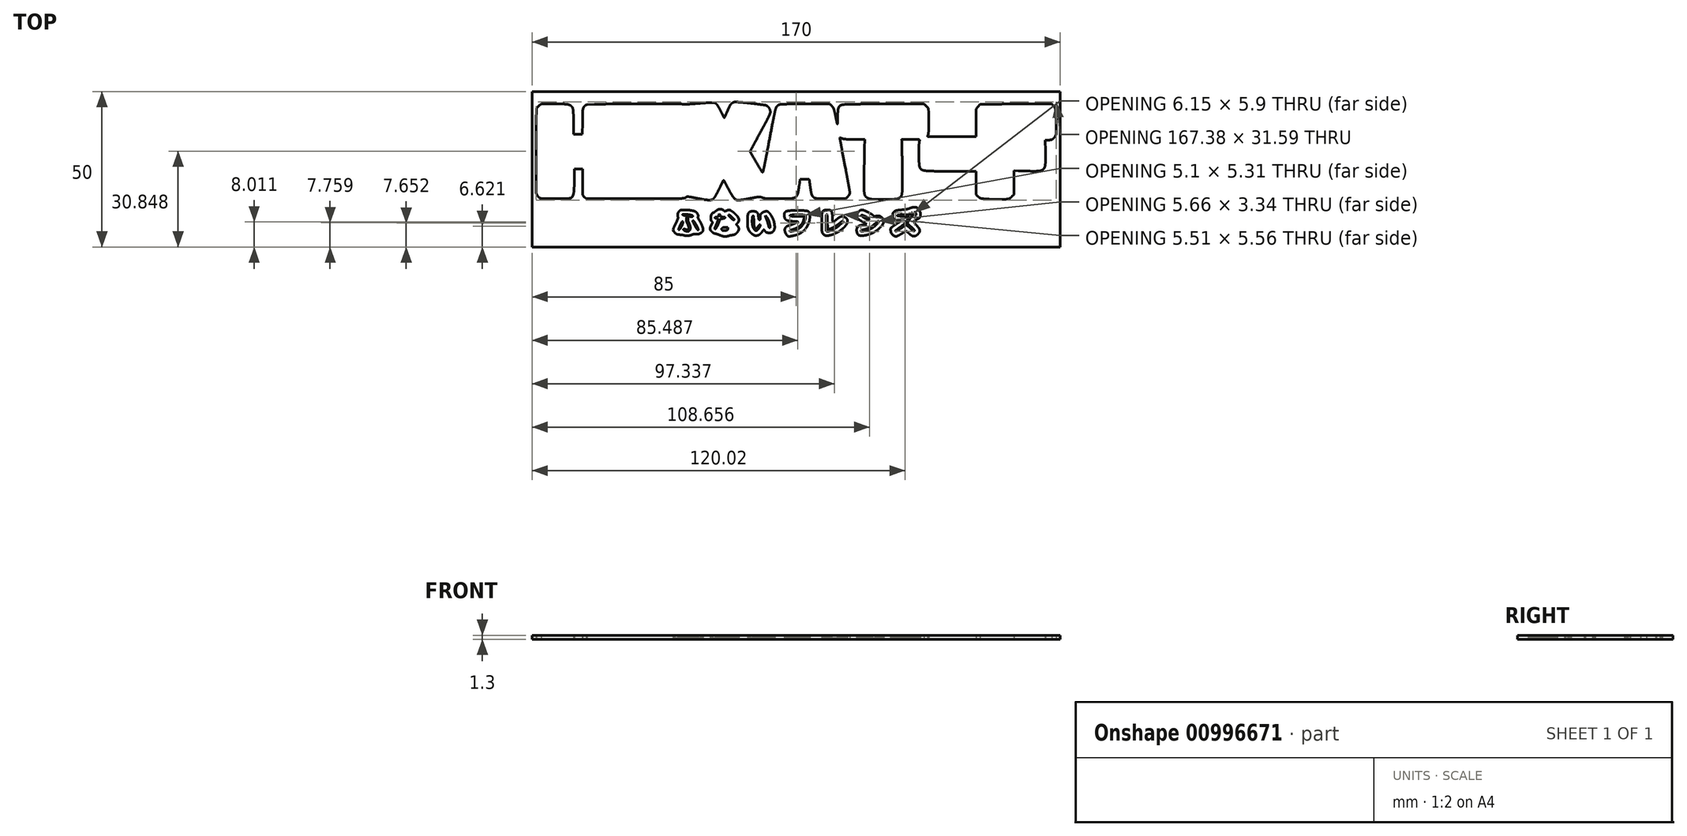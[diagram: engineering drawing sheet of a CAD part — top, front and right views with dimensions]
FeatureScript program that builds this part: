
annotation { "Feature Type Name" : "Feature", "Feature Type Description" : "" }
export const myFeature = defineFeature(function(context is Context, id is Id, definition is map)
    precondition{}
    {
        {
            var Q0;
            Q0=qCreatedBy(makeId("Top.planeOp"),FACE);
            var sketch = newSketch(context, id + "F0", { "sketchPlane" : qUnion([Q0])});
            skArc(sketch, "E0", {"start": v(-16.39, 21.41) * mm, "mid": v(-15.05, 21.27) * mm, "end": v(-13.72, 21.12) * mm});
            skArc(sketch, "E1", {"start": v(-13.72, 21.12) * mm, "mid": v(-12.67, 21) * mm, "end": v(-11.61, 20.86) * mm});
            skArc(sketch, "E2", {"start": v(-11.61, 20.86) * mm, "mid": v(-10.8, 20.74) * mm, "end": v(-9.97, 20.62) * mm});
            skArc(sketch, "E3", {"start": v(-9.97, 20.62) * mm, "mid": v(-9.73, 20.56) * mm, "end": v(-9.5, 20.47) * mm});
            skArc(sketch, "E4", {"start": v(-9.5, 20.47) * mm, "mid": v(-9.28, 20.34) * mm, "end": v(-9.1, 20.17) * mm});
            skArc(sketch, "E5", {"start": v(-9.1, 20.17) * mm, "mid": v(-8.9, 19.95) * mm, "end": v(-8.73, 19.7) * mm});
            skArc(sketch, "E6", {"start": v(-8.73, 19.7) * mm, "mid": v(-8.58, 19.45) * mm, "end": v(-8.45, 19.17) * mm});
            skArc(sketch, "E7", {"start": v(-8.45, 19.17) * mm, "mid": v(-8.37, 18.9) * mm, "end": v(-8.33, 18.63) * mm});
            skArc(sketch, "E8", {"start": v(-8.33, 18.63) * mm, "mid": v(-8.32, 18.52) * mm, "end": v(-8.32, 18.42) * mm});
            skArc(sketch, "E9", {"start": v(-8.32, 18.42) * mm, "mid": v(-8.32, 18.33) * mm, "end": v(-8.33, 18.24) * mm});
            skArc(sketch, "E10", {"start": v(-8.33, 18.24) * mm, "mid": v(-8.36, 18.14) * mm, "end": v(-8.38, 18.04) * mm});
            skArc(sketch, "E11", {"start": v(-8.38, 18.04) * mm, "mid": v(-8.43, 17.9) * mm, "end": v(-8.48, 17.77) * mm});
            skArc(sketch, "E12", {"start": v(-8.48, 17.77) * mm, "mid": v(-8.64, 17.4) * mm, "end": v(-8.8, 17.04) * mm});
            skArc(sketch, "E13", {"start": v(-8.8, 17.04) * mm, "mid": v(-9.11, 16.42) * mm, "end": v(-9.43, 15.8) * mm});
            skArc(sketch, "E14", {"start": v(-9.43, 15.8) * mm, "mid": v(-9.8, 15.06) * mm, "end": v(-10.2, 14.33) * mm});
            skArc(sketch, "E15", {"start": v(-10.2, 14.33) * mm, "mid": v(-10.61, 13.55) * mm, "end": v(-11.04, 12.77) * mm});
            skArc(sketch, "E16", {"start": v(-11.04, 12.77) * mm, "mid": v(-11.9, 11.22) * mm, "end": v(-12.74, 9.67) * mm});
            skArc(sketch, "E17", {"start": v(-12.74, 9.67) * mm, "mid": v(-13.3, 8.62) * mm, "end": v(-13.86, 7.57) * mm});
            skArc(sketch, "E18", {"start": v(-13.86, 7.57) * mm, "mid": v(-14.27, 6.8) * mm, "end": v(-14.67, 6.02) * mm});
            skArc(sketch, "E19", {"start": v(-14.67, 6.02) * mm, "mid": v(-14.73, 5.88) * mm, "end": v(-14.74, 5.72) * mm});
            skArc(sketch, "E20", {"start": v(-14.74, 5.72) * mm, "mid": v(-14.7, 5.46) * mm, "end": v(-14.6, 5.22) * mm});
            skArc(sketch, "E21", {"start": v(-14.6, 5.22) * mm, "mid": v(-13.73, 3.73) * mm, "end": v(-12.84, 2.24) * mm});
            skArc(sketch, "E22", {"start": v(-12.84, 2.24) * mm, "mid": v(-11.93, 0.71) * mm, "end": v(-11.02, -0.8) * mm});
            skArc(sketch, "E23", {"start": v(-11.02, -0.8) * mm, "mid": v(-10.9, -0.91) * mm, "end": v(-10.76, -0.95) * mm});
            skArc(sketch, "E24", {"start": v(-10.76, -0.95) * mm, "mid": v(-10.7, -0.93) * mm, "end": v(-10.66, -0.87) * mm});
            skArc(sketch, "E25", {"start": v(-10.66, -0.87) * mm, "mid": v(-10.44, 0.14) * mm, "end": v(-10.24, 1.15) * mm});
            skArc(sketch, "E26", {"start": v(-10.24, 1.15) * mm, "mid": v(-9.95, 2.55) * mm, "end": v(-9.68, 3.94) * mm});
            skArc(sketch, "E27", {"start": v(-9.68, 3.94) * mm, "mid": v(-9.23, 6.26) * mm, "end": v(-8.8, 8.58) * mm});
            skArc(sketch, "E28", {"start": v(-8.8, 8.58) * mm, "mid": v(-8.22, 11.62) * mm, "end": v(-7.63, 14.66) * mm});
            skArc(sketch, "E29", {"start": v(-7.63, 14.66) * mm, "mid": v(-7.35, 16.1) * mm, "end": v(-7.05, 17.54) * mm});
            skArc(sketch, "E30", {"start": v(-7.05, 17.54) * mm, "mid": v(-6.87, 18.38) * mm, "end": v(-6.66, 19.23) * mm});
            skArc(sketch, "E31", {"start": v(-6.66, 19.23) * mm, "mid": v(-6.54, 19.62) * mm, "end": v(-6.37, 20) * mm});
            skArc(sketch, "E32", {"start": v(-6.37, 20) * mm, "mid": v(-6.26, 20.16) * mm, "end": v(-6.14, 20.31) * mm});
            skArc(sketch, "E33", {"start": v(-6.14, 20.31) * mm, "mid": v(-6, 20.45) * mm, "end": v(-5.85, 20.57) * mm});
            skArc(sketch, "E34", {"start": v(-5.85, 20.57) * mm, "mid": v(-5.67, 20.68) * mm, "end": v(-5.49, 20.77) * mm});
            skArc(sketch, "E35", {"start": v(-5.49, 20.77) * mm, "mid": v(-5.28, 20.84) * mm, "end": v(-5.07, 20.9) * mm});
            skArc(sketch, "E36", {"start": v(-5.07, 20.9) * mm, "mid": v(-4.86, 20.93) * mm, "end": v(-4.64, 20.94) * mm});
            skArc(sketch, "E37", {"start": v(-4.64, 20.94) * mm, "mid": v(-3.87, 20.96) * mm, "end": v(-3.1, 20.97) * mm});
            skArc(sketch, "E38", {"start": v(-3.1, 20.97) * mm, "mid": v(-1.96, 20.98) * mm, "end": v(-0.81, 21) * mm});
            skArc(sketch, "E39", {"start": v(-0.81, 21) * mm, "mid": v(1.12, 21) * mm, "end": v(3.05, 21.01) * mm});
            skLineSegment(sketch, "E40", {"start": v(3.05, 21.01) * mm, "end": v(10.73, 21.04) * mm});
            skLineSegment(sketch, "E41", {"start": v(10.73, 21.04) * mm, "end": v(11.19, 20.64) * mm});
            skArc(sketch, "E42", {"start": v(11.19, 20.64) * mm, "mid": v(11.47, 20.36) * mm, "end": v(11.73, 20.06) * mm});
            skArc(sketch, "E43", {"start": v(11.73, 20.06) * mm, "mid": v(11.92, 19.77) * mm, "end": v(12.07, 19.45) * mm});
            skArc(sketch, "E44", {"start": v(12.07, 19.45) * mm, "mid": v(12.23, 19) * mm, "end": v(12.36, 18.52) * mm});
            skArc(sketch, "E45", {"start": v(12.36, 18.52) * mm, "mid": v(12.58, 17.5) * mm, "end": v(12.8, 16.48) * mm});
            skArc(sketch, "E46", {"start": v(12.8, 16.48) * mm, "mid": v(12.89, 16.08) * mm, "end": v(12.97, 15.67) * mm});
            skArc(sketch, "E47", {"start": v(12.97, 15.67) * mm, "mid": v(13.04, 15.35) * mm, "end": v(13.12, 15.03) * mm});
            skArc(sketch, "E48", {"start": v(13.12, 15.03) * mm, "mid": v(13.17, 14.8) * mm, "end": v(13.23, 14.55) * mm});
            skArc(sketch, "E49", {"start": v(13.23, 14.55) * mm, "mid": v(13.24, 14.54) * mm, "end": v(13.25, 14.55) * mm});
            skArc(sketch, "E50", {"start": v(13.25, 14.55) * mm, "mid": v(13.26, 14.63) * mm, "end": v(13.26, 14.7) * mm});
            skArc(sketch, "E51", {"start": v(13.26, 14.7) * mm, "mid": v(13.27, 15) * mm, "end": v(13.28, 15.29) * mm});
            skArc(sketch, "E52", {"start": v(13.28, 15.29) * mm, "mid": v(13.29, 15.63) * mm, "end": v(13.3, 15.98) * mm});
            skArc(sketch, "E53", {"start": v(13.3, 15.98) * mm, "mid": v(13.31, 16.37) * mm, "end": v(13.32, 16.76) * mm});
            skArc(sketch, "E54", {"start": v(13.32, 16.76) * mm, "mid": v(13.35, 17.49) * mm, "end": v(13.38, 18.21) * mm});
            skArc(sketch, "E55", {"start": v(13.38, 18.21) * mm, "mid": v(13.4, 18.6) * mm, "end": v(13.45, 19) * mm});
            skArc(sketch, "E56", {"start": v(13.45, 19) * mm, "mid": v(13.5, 19.26) * mm, "end": v(13.55, 19.52) * mm});
            skArc(sketch, "E57", {"start": v(13.55, 19.52) * mm, "mid": v(13.63, 19.75) * mm, "end": v(13.73, 19.98) * mm});
            skArc(sketch, "E58", {"start": v(13.73, 19.98) * mm, "mid": v(13.85, 20.18) * mm, "end": v(14, 20.35) * mm});
            skArc(sketch, "E59", {"start": v(14, 20.35) * mm, "mid": v(14.17, 20.5) * mm, "end": v(14.36, 20.6) * mm});
            skArc(sketch, "E60", {"start": v(14.36, 20.6) * mm, "mid": v(14.64, 20.7) * mm, "end": v(14.94, 20.76) * mm});
            skArc(sketch, "E61", {"start": v(14.94, 20.76) * mm, "mid": v(15.46, 20.83) * mm, "end": v(15.99, 20.9) * mm});
            skArc(sketch, "E62", {"start": v(15.99, 20.9) * mm, "mid": v(16.28, 20.93) * mm, "end": v(16.58, 20.94) * mm});
            skArc(sketch, "E63", {"start": v(16.58, 20.94) * mm, "mid": v(18.06, 20.95) * mm, "end": v(19.55, 20.96) * mm});
            skArc(sketch, "E64", {"start": v(19.55, 20.96) * mm, "mid": v(21.5, 20.98) * mm, "end": v(23.44, 20.99) * mm});
            skArc(sketch, "E65", {"start": v(23.44, 20.99) * mm, "mid": v(26.15, 21) * mm, "end": v(28.87, 21) * mm});
            skLineSegment(sketch, "E66", {"start": v(28.87, 21) * mm, "end": v(41.08, 21.04) * mm});
            skLineSegment(sketch, "E67", {"start": v(41.08, 21.04) * mm, "end": v(41.82, 20.37) * mm});
            skLineSegment(sketch, "E68", {"start": v(41.82, 20.37) * mm, "end": v(42.57, 19.7) * mm});
            skLineSegment(sketch, "E69", {"start": v(42.57, 19.7) * mm, "end": v(42.62, 18.14) * mm});
            skArc(sketch, "E70", {"start": v(42.62, 18.14) * mm, "mid": v(42.63, 17.76) * mm, "end": v(42.64, 17.37) * mm});
            skArc(sketch, "E71", {"start": v(42.64, 17.37) * mm, "mid": v(42.64, 16.84) * mm, "end": v(42.65, 16.3) * mm});
            skArc(sketch, "E72", {"start": v(42.65, 16.3) * mm, "mid": v(42.65, 15.72) * mm, "end": v(42.65, 15.14) * mm});
            skArc(sketch, "E73", {"start": v(42.65, 15.14) * mm, "mid": v(42.64, 14.6) * mm, "end": v(42.64, 14.06) * mm});
            skArc(sketch, "E74", {"start": v(42.64, 14.06) * mm, "mid": v(42.63, 13.3) * mm, "end": v(42.62, 12.54) * mm});
            skArc(sketch, "E75", {"start": v(42.62, 12.54) * mm, "mid": v(42.6, 12.2) * mm, "end": v(42.59, 11.86) * mm});
            skArc(sketch, "E76", {"start": v(42.59, 11.86) * mm, "mid": v(42.57, 11.65) * mm, "end": v(42.54, 11.44) * mm});
            skArc(sketch, "E77", {"start": v(42.54, 11.44) * mm, "mid": v(42.5, 11.26) * mm, "end": v(42.46, 11.09) * mm});
            skArc(sketch, "E78", {"start": v(42.46, 11.09) * mm, "mid": v(42.43, 11) * mm, "end": v(42.4, 10.91) * mm});
            skArc(sketch, "E79", {"start": v(42.4, 10.91) * mm, "mid": v(42.37, 10.83) * mm, "end": v(42.35, 10.75) * mm});
            skArc(sketch, "E80", {"start": v(42.35, 10.75) * mm, "mid": v(42.33, 10.69) * mm, "end": v(42.31, 10.62) * mm});
            skArc(sketch, "E81", {"start": v(42.31, 10.62) * mm, "mid": v(42.3, 10.6) * mm, "end": v(42.3, 10.58) * mm});
            skArc(sketch, "E82", {"start": v(42.3, 10.58) * mm, "mid": v(42.31, 10.57) * mm, "end": v(42.33, 10.56) * mm});
            skArc(sketch, "E83", {"start": v(42.33, 10.56) * mm, "mid": v(43.46, 10.55) * mm, "end": v(44.6, 10.54) * mm});
            skArc(sketch, "E84", {"start": v(44.6, 10.54) * mm, "mid": v(45.86, 10.54) * mm, "end": v(47.12, 10.53) * mm});
            skArc(sketch, "E85", {"start": v(47.12, 10.53) * mm, "mid": v(48.61, 10.53) * mm, "end": v(50.11, 10.53) * mm});
            skLineSegment(sketch, "E86", {"start": v(50.11, 10.53) * mm, "end": v(57.92, 10.53) * mm});
            skLineSegment(sketch, "E87", {"start": v(57.92, 10.53) * mm, "end": v(57.92, 14.98) * mm});
            skLineSegment(sketch, "E88", {"start": v(57.92, 14.98) * mm, "end": v(57.92, 19.43) * mm});
            skLineSegment(sketch, "E89", {"start": v(57.92, 19.43) * mm, "end": v(58.56, 20.15) * mm});
            skLineSegment(sketch, "E90", {"start": v(58.56, 20.15) * mm, "end": v(59.2, 20.88) * mm});
            skLineSegment(sketch, "E91", {"start": v(59.2, 20.88) * mm, "end": v(60.08, 20.92) * mm});
            skArc(sketch, "E92", {"start": v(60.08, 20.92) * mm, "mid": v(60.4, 20.93) * mm, "end": v(60.73, 20.93) * mm});
            skArc(sketch, "E93", {"start": v(60.73, 20.93) * mm, "mid": v(62.28, 20.95) * mm, "end": v(63.83, 20.96) * mm});
            skArc(sketch, "E94", {"start": v(63.83, 20.96) * mm, "mid": v(65.65, 20.97) * mm, "end": v(67.46, 20.98) * mm});
            skArc(sketch, "E95", {"start": v(67.46, 20.98) * mm, "mid": v(69.53, 21) * mm, "end": v(71.6, 21) * mm});
            skLineSegment(sketch, "E96", {"start": v(71.6, 21) * mm, "end": v(82.25, 21.05) * mm});
            skLineSegment(sketch, "E97", {"start": v(82.25, 21.05) * mm, "end": v(82.7, 20.57) * mm});
            skArc(sketch, "E98", {"start": v(82.7, 20.57) * mm, "mid": v(82.87, 20.36) * mm, "end": v(83.04, 20.15) * mm});
            skArc(sketch, "E99", {"start": v(83.04, 20.15) * mm, "mid": v(83.15, 19.98) * mm, "end": v(83.25, 19.8) * mm});
            skArc(sketch, "E100", {"start": v(83.25, 19.8) * mm, "mid": v(83.32, 19.62) * mm, "end": v(83.37, 19.42) * mm});
            skArc(sketch, "E101", {"start": v(83.37, 19.42) * mm, "mid": v(83.42, 19.16) * mm, "end": v(83.46, 18.9) * mm});
            skArc(sketch, "E102", {"start": v(83.46, 18.9) * mm, "mid": v(83.5, 18.42) * mm, "end": v(83.54, 17.94) * mm});
            skArc(sketch, "E103", {"start": v(83.54, 17.94) * mm, "mid": v(83.58, 17.18) * mm, "end": v(83.61, 16.43) * mm});
            skArc(sketch, "E104", {"start": v(83.61, 16.43) * mm, "mid": v(83.64, 15.59) * mm, "end": v(83.67, 14.75) * mm});
            skArc(sketch, "E105", {"start": v(83.67, 14.75) * mm, "mid": v(83.68, 13.95) * mm, "end": v(83.69, 13.14) * mm});
            skArc(sketch, "E106", {"start": v(83.69, 13.14) * mm, "mid": v(83.69, 12.54) * mm, "end": v(83.69, 11.93) * mm});
            skArc(sketch, "E107", {"start": v(83.69, 11.93) * mm, "mid": v(83.68, 11.7) * mm, "end": v(83.67, 11.46) * mm});
            skArc(sketch, "E108", {"start": v(83.67, 11.46) * mm, "mid": v(83.65, 11.32) * mm, "end": v(83.63, 11.18) * mm});
            skArc(sketch, "E109", {"start": v(83.63, 11.18) * mm, "mid": v(83.59, 11.05) * mm, "end": v(83.53, 10.93) * mm});
            skArc(sketch, "E110", {"start": v(83.53, 10.93) * mm, "mid": v(83.42, 10.72) * mm, "end": v(83.3, 10.52) * mm});
            skArc(sketch, "E111", {"start": v(83.3, 10.52) * mm, "mid": v(83.14, 10.32) * mm, "end": v(82.98, 10.13) * mm});
            skArc(sketch, "E112", {"start": v(82.98, 10.13) * mm, "mid": v(82.82, 9.96) * mm, "end": v(82.65, 9.8) * mm});
            skArc(sketch, "E113", {"start": v(82.65, 9.8) * mm, "mid": v(82.5, 9.69) * mm, "end": v(82.33, 9.6) * mm});
            skArc(sketch, "E114", {"start": v(82.33, 9.6) * mm, "mid": v(82.22, 9.54) * mm, "end": v(82.1, 9.49) * mm});
            skArc(sketch, "E115", {"start": v(82.1, 9.49) * mm, "mid": v(82, 9.46) * mm, "end": v(81.89, 9.44) * mm});
            skArc(sketch, "E116", {"start": v(81.89, 9.44) * mm, "mid": v(81.75, 9.42) * mm, "end": v(81.6, 9.41) * mm});
            skArc(sketch, "E117", {"start": v(81.6, 9.41) * mm, "mid": v(81.34, 9.41) * mm, "end": v(81.07, 9.4) * mm});
            skLineSegment(sketch, "E118", {"start": v(81.07, 9.4) * mm, "end": v(80.17, 9.4) * mm});
            skLineSegment(sketch, "E119", {"start": v(80.17, 9.4) * mm, "end": v(80.22, 5.86) * mm});
            skArc(sketch, "E120", {"start": v(80.22, 5.86) * mm, "mid": v(80.23, 4.63) * mm, "end": v(80.24, 3.4) * mm});
            skArc(sketch, "E121", {"start": v(80.24, 3.4) * mm, "mid": v(80.23, 2.75) * mm, "end": v(80.2, 2.1) * mm});
            skArc(sketch, "E122", {"start": v(80.2, 2.1) * mm, "mid": v(80.18, 1.68) * mm, "end": v(80.12, 1.26) * mm});
            skArc(sketch, "E123", {"start": v(80.12, 1.26) * mm, "mid": v(80.06, 0.94) * mm, "end": v(79.96, 0.62) * mm});
            skArc(sketch, "E124", {"start": v(79.96, 0.62) * mm, "mid": v(79.88, 0.45) * mm, "end": v(79.78, 0.29) * mm});
            skArc(sketch, "E125", {"start": v(79.78, 0.29) * mm, "mid": v(79.66, 0.13) * mm, "end": v(79.52, -0.02) * mm});
            skArc(sketch, "E126", {"start": v(79.52, -0.02) * mm, "mid": v(79.36, -0.14) * mm, "end": v(79.2, -0.26) * mm});
            skArc(sketch, "E127", {"start": v(79.2, -0.26) * mm, "mid": v(79.01, -0.35) * mm, "end": v(78.82, -0.42) * mm});
            skArc(sketch, "E128", {"start": v(78.82, -0.42) * mm, "mid": v(78.53, -0.5) * mm, "end": v(78.24, -0.54) * mm});
            skArc(sketch, "E129", {"start": v(78.24, -0.54) * mm, "mid": v(77.82, -0.59) * mm, "end": v(77.4, -0.61) * mm});
            skArc(sketch, "E130", {"start": v(77.4, -0.61) * mm, "mid": v(76.86, -0.63) * mm, "end": v(76.3, -0.63) * mm});
            skArc(sketch, "E131", {"start": v(76.3, -0.63) * mm, "mid": v(75.58, -0.62) * mm, "end": v(74.86, -0.6) * mm});
            skArc(sketch, "E132", {"start": v(74.86, -0.6) * mm, "mid": v(74.42, -0.59) * mm, "end": v(73.99, -0.57) * mm});
            skArc(sketch, "E133", {"start": v(73.99, -0.57) * mm, "mid": v(73.5, -0.56) * mm, "end": v(73.03, -0.54) * mm});
            skArc(sketch, "E134", {"start": v(73.03, -0.54) * mm, "mid": v(72.58, -0.53) * mm, "end": v(72.13, -0.51) * mm});
            skArc(sketch, "E135", {"start": v(72.13, -0.51) * mm, "mid": v(71.78, -0.5) * mm, "end": v(71.44, -0.49) * mm});
            skLineSegment(sketch, "E136", {"start": v(71.44, -0.49) * mm, "end": v(70.03, -0.44) * mm});
            skLineSegment(sketch, "E137", {"start": v(70.03, -0.44) * mm, "end": v(70.03, -4.29) * mm});
            skLineSegment(sketch, "E138", {"start": v(70.03, -4.29) * mm, "end": v(70.03, -8.13) * mm});
            skLineSegment(sketch, "E139", {"start": v(70.03, -8.13) * mm, "end": v(69.45, -8.74) * mm});
            skArc(sketch, "E140", {"start": v(69.45, -8.74) * mm, "mid": v(69.33, -8.86) * mm, "end": v(69.2, -8.98) * mm});
            skArc(sketch, "E141", {"start": v(69.2, -8.98) * mm, "mid": v(69.09, -9.1) * mm, "end": v(68.96, -9.2) * mm});
            skArc(sketch, "E142", {"start": v(68.96, -9.2) * mm, "mid": v(68.86, -9.29) * mm, "end": v(68.75, -9.37) * mm});
            skArc(sketch, "E143", {"start": v(68.75, -9.37) * mm, "mid": v(68.69, -9.42) * mm, "end": v(68.62, -9.45) * mm});
            skArc(sketch, "E144", {"start": v(68.62, -9.45) * mm, "mid": v(68.4, -9.52) * mm, "end": v(68.19, -9.57) * mm});
            skArc(sketch, "E145", {"start": v(68.19, -9.57) * mm, "mid": v(67.85, -9.61) * mm, "end": v(67.52, -9.64) * mm});
            skArc(sketch, "E146", {"start": v(67.52, -9.64) * mm, "mid": v(67.05, -9.67) * mm, "end": v(66.58, -9.69) * mm});
            skArc(sketch, "E147", {"start": v(66.58, -9.69) * mm, "mid": v(65.92, -9.7) * mm, "end": v(65.26, -9.7) * mm});
            skArc(sketch, "E148", {"start": v(65.26, -9.7) * mm, "mid": v(64.18, -9.7) * mm, "end": v(63.1, -9.67) * mm});
            skArc(sketch, "E149", {"start": v(63.1, -9.67) * mm, "mid": v(62.18, -9.64) * mm, "end": v(61.28, -9.58) * mm});
            skArc(sketch, "E150", {"start": v(61.28, -9.58) * mm, "mid": v(60.56, -9.53) * mm, "end": v(59.86, -9.45) * mm});
            skArc(sketch, "E151", {"start": v(59.86, -9.45) * mm, "mid": v(59.5, -9.39) * mm, "end": v(59.18, -9.27) * mm});
            skArc(sketch, "E152", {"start": v(59.18, -9.27) * mm, "mid": v(59.1, -9.23) * mm, "end": v(59.02, -9.19) * mm});
            skArc(sketch, "E153", {"start": v(59.02, -9.19) * mm, "mid": v(58.92, -9.11) * mm, "end": v(58.81, -9.04) * mm});
            skArc(sketch, "E154", {"start": v(58.81, -9.04) * mm, "mid": v(58.7, -8.95) * mm, "end": v(58.6, -8.86) * mm});
            skArc(sketch, "E155", {"start": v(58.6, -8.86) * mm, "mid": v(58.49, -8.76) * mm, "end": v(58.39, -8.67) * mm});
            skLineSegment(sketch, "E156", {"start": v(58.39, -8.67) * mm, "end": v(57.92, -8.2) * mm});
            skLineSegment(sketch, "E157", {"start": v(57.92, -8.2) * mm, "end": v(57.92, -4.44) * mm});
            skLineSegment(sketch, "E158", {"start": v(57.92, -4.44) * mm, "end": v(57.92, -0.67) * mm});
            skLineSegment(sketch, "E159", {"start": v(57.92, -0.67) * mm, "end": v(51.95, -0.67) * mm});
            skArc(sketch, "E160", {"start": v(51.95, -0.67) * mm, "mid": v(50.73, -0.67) * mm, "end": v(49.51, -0.66) * mm});
            skArc(sketch, "E161", {"start": v(49.51, -0.66) * mm, "mid": v(48.32, -0.66) * mm, "end": v(47.13, -0.65) * mm});
            skArc(sketch, "E162", {"start": v(47.13, -0.65) * mm, "mid": v(46.1, -0.64) * mm, "end": v(45.07, -0.63) * mm});
            skArc(sketch, "E163", {"start": v(45.07, -0.63) * mm, "mid": v(44.5, -0.62) * mm, "end": v(43.92, -0.6) * mm});
            skArc(sketch, "E164", {"start": v(43.92, -0.6) * mm, "mid": v(42.95, -0.57) * mm, "end": v(42, -0.51) * mm});
            skArc(sketch, "E165", {"start": v(42, -0.51) * mm, "mid": v(41.47, -0.46) * mm, "end": v(40.96, -0.37) * mm});
            skArc(sketch, "E166", {"start": v(40.96, -0.37) * mm, "mid": v(40.64, -0.26) * mm, "end": v(40.33, -0.11) * mm});
            skArc(sketch, "E167", {"start": v(40.33, -0.11) * mm, "mid": v(40.1, 0.07) * mm, "end": v(39.91, 0.3) * mm});
            skArc(sketch, "E168", {"start": v(39.91, 0.3) * mm, "mid": v(39.81, 0.5) * mm, "end": v(39.74, 0.7) * mm});
            skArc(sketch, "E169", {"start": v(39.74, 0.7) * mm, "mid": v(39.68, 0.92) * mm, "end": v(39.63, 1.16) * mm});
            skArc(sketch, "E170", {"start": v(39.63, 1.16) * mm, "mid": v(39.59, 1.52) * mm, "end": v(39.56, 1.89) * mm});
            skArc(sketch, "E171", {"start": v(39.56, 1.89) * mm, "mid": v(39.53, 2.57) * mm, "end": v(39.5, 3.25) * mm});
            skArc(sketch, "E172", {"start": v(39.5, 3.25) * mm, "mid": v(39.47, 4.22) * mm, "end": v(39.46, 5.19) * mm});
            skArc(sketch, "E173", {"start": v(39.46, 5.19) * mm, "mid": v(39.47, 6.13) * mm, "end": v(39.5, 7.07) * mm});
            skArc(sketch, "E174", {"start": v(39.5, 7.07) * mm, "mid": v(39.53, 7.89) * mm, "end": v(39.58, 8.7) * mm});
            skArc(sketch, "E175", {"start": v(39.58, 8.7) * mm, "mid": v(39.62, 8.97) * mm, "end": v(39.72, 9.21) * mm});
            skArc(sketch, "E176", {"start": v(39.72, 9.21) * mm, "mid": v(39.74, 9.25) * mm, "end": v(39.75, 9.29) * mm});
            skArc(sketch, "E177", {"start": v(39.75, 9.29) * mm, "mid": v(39.76, 9.32) * mm, "end": v(39.76, 9.35) * mm});
            skArc(sketch, "E178", {"start": v(39.76, 9.35) * mm, "mid": v(39.75, 9.38) * mm, "end": v(39.74, 9.4) * mm});
            skArc(sketch, "E179", {"start": v(39.74, 9.4) * mm, "mid": v(39.71, 9.44) * mm, "end": v(39.68, 9.47) * mm});
            skArc(sketch, "E180", {"start": v(39.68, 9.47) * mm, "mid": v(39.62, 9.52) * mm, "end": v(39.54, 9.54) * mm});
            skArc(sketch, "E181", {"start": v(39.54, 9.54) * mm, "mid": v(39.33, 9.56) * mm, "end": v(39.11, 9.57) * mm});
            skArc(sketch, "E182", {"start": v(39.11, 9.57) * mm, "mid": v(38.74, 9.58) * mm, "end": v(38.37, 9.6) * mm});
            skArc(sketch, "E183", {"start": v(38.37, 9.6) * mm, "mid": v(37.55, 9.6) * mm, "end": v(36.73, 9.6) * mm});
            skArc(sketch, "E184", {"start": v(36.73, 9.6) * mm, "mid": v(35.83, 9.61) * mm, "end": v(34.93, 9.62) * mm});
            skArc(sketch, "E185", {"start": v(34.93, 9.62) * mm, "mid": v(34.61, 9.62) * mm, "end": v(34.3, 9.6) * mm});
            skArc(sketch, "E186", {"start": v(34.3, 9.6) * mm, "mid": v(34.14, 9.6) * mm, "end": v(33.98, 9.58) * mm});
            skArc(sketch, "E187", {"start": v(33.98, 9.58) * mm, "mid": v(33.94, 9.55) * mm, "end": v(33.93, 9.5) * mm});
            skArc(sketch, "E188", {"start": v(33.93, 9.5) * mm, "mid": v(33.97, 9.35) * mm, "end": v(33.98, 9.2) * mm});
            skArc(sketch, "E189", {"start": v(33.98, 9.2) * mm, "mid": v(34.02, 7.57) * mm, "end": v(34.05, 5.93) * mm});
            skArc(sketch, "E190", {"start": v(34.05, 5.93) * mm, "mid": v(34.09, 4.16) * mm, "end": v(34.12, 2.39) * mm});
            skArc(sketch, "E191", {"start": v(34.12, 2.39) * mm, "mid": v(34.14, 0.5) * mm, "end": v(34.16, -1.4) * mm});
            skArc(sketch, "E192", {"start": v(34.16, -1.4) * mm, "mid": v(34.17, -3.38) * mm, "end": v(34.18, -5.36) * mm});
            skArc(sketch, "E193", {"start": v(34.18, -5.36) * mm, "mid": v(34.16, -6.27) * mm, "end": v(34.11, -7.2) * mm});
            skArc(sketch, "E194", {"start": v(34.11, -7.2) * mm, "mid": v(34.05, -7.73) * mm, "end": v(33.95, -8.25) * mm});
            skArc(sketch, "E195", {"start": v(33.95, -8.25) * mm, "mid": v(33.82, -8.6) * mm, "end": v(33.61, -8.9) * mm});
            skArc(sketch, "E196", {"start": v(33.61, -8.9) * mm, "mid": v(33.42, -9.09) * mm, "end": v(33.2, -9.24) * mm});
            skArc(sketch, "E197", {"start": v(33.2, -9.24) * mm, "mid": v(32.92, -9.37) * mm, "end": v(32.64, -9.47) * mm});
            skArc(sketch, "E198", {"start": v(32.64, -9.47) * mm, "mid": v(32.24, -9.55) * mm, "end": v(31.83, -9.6) * mm});
            skArc(sketch, "E199", {"start": v(31.83, -9.6) * mm, "mid": v(31.17, -9.67) * mm, "end": v(30.51, -9.7) * mm});
            skArc(sketch, "E200", {"start": v(30.51, -9.7) * mm, "mid": v(29.72, -9.74) * mm, "end": v(28.93, -9.76) * mm});
            skArc(sketch, "E201", {"start": v(28.93, -9.76) * mm, "mid": v(27.9, -9.76) * mm, "end": v(26.87, -9.75) * mm});
            skArc(sketch, "E202", {"start": v(26.87, -9.75) * mm, "mid": v(25.89, -9.73) * mm, "end": v(24.9, -9.7) * mm});
            skArc(sketch, "E203", {"start": v(24.9, -9.7) * mm, "mid": v(24.46, -9.67) * mm, "end": v(24.03, -9.6) * mm});
            skArc(sketch, "E204", {"start": v(24.03, -9.6) * mm, "mid": v(23.78, -9.55) * mm, "end": v(23.53, -9.48) * mm});
            skArc(sketch, "E205", {"start": v(23.53, -9.48) * mm, "mid": v(23.29, -9.4) * mm, "end": v(23.05, -9.29) * mm});
            skArc(sketch, "E206", {"start": v(23.05, -9.29) * mm, "mid": v(22.84, -9.18) * mm, "end": v(22.64, -9.06) * mm});
            skArc(sketch, "E207", {"start": v(22.64, -9.06) * mm, "mid": v(22.5, -8.95) * mm, "end": v(22.37, -8.83) * mm});
            skArc(sketch, "E208", {"start": v(22.37, -8.83) * mm, "mid": v(22.15, -8.51) * mm, "end": v(22.03, -8.15) * mm});
            skArc(sketch, "E209", {"start": v(22.03, -8.15) * mm, "mid": v(21.92, -7.58) * mm, "end": v(21.86, -7) * mm});
            skArc(sketch, "E210", {"start": v(21.86, -7) * mm, "mid": v(21.82, -6.02) * mm, "end": v(21.8, -5.03) * mm});
            skArc(sketch, "E211", {"start": v(21.8, -5.03) * mm, "mid": v(21.83, -3) * mm, "end": v(21.85, -0.95) * mm});
            skArc(sketch, "E212", {"start": v(21.85, -0.95) * mm, "mid": v(21.87, 0.08) * mm, "end": v(21.89, 1.12) * mm});
            skArc(sketch, "E213", {"start": v(21.89, 1.12) * mm, "mid": v(21.9, 2.22) * mm, "end": v(21.93, 3.32) * mm});
            skArc(sketch, "E214", {"start": v(21.93, 3.32) * mm, "mid": v(21.94, 4.33) * mm, "end": v(21.96, 5.34) * mm});
            skArc(sketch, "E215", {"start": v(21.96, 5.34) * mm, "mid": v(21.97, 6.05) * mm, "end": v(21.98, 6.77) * mm});
            skLineSegment(sketch, "E216", {"start": v(21.98, 6.77) * mm, "end": v(22.03, 9.62) * mm});
            skLineSegment(sketch, "E217", {"start": v(22.03, 9.62) * mm, "end": v(19.23, 9.62) * mm});
            skArc(sketch, "E218", {"start": v(19.23, 9.62) * mm, "mid": v(18.14, 9.62) * mm, "end": v(17.04, 9.63) * mm});
            skArc(sketch, "E219", {"start": v(17.04, 9.63) * mm, "mid": v(16.47, 9.65) * mm, "end": v(15.9, 9.69) * mm});
            skArc(sketch, "E220", {"start": v(15.9, 9.69) * mm, "mid": v(15.52, 9.73) * mm, "end": v(15.15, 9.79) * mm});
            skArc(sketch, "E221", {"start": v(15.15, 9.79) * mm, "mid": v(14.86, 9.87) * mm, "end": v(14.57, 9.98) * mm});
            skArc(sketch, "E222", {"start": v(14.57, 9.98) * mm, "mid": v(14.48, 10.02) * mm, "end": v(14.39, 10.06) * mm});
            skArc(sketch, "E223", {"start": v(14.39, 10.06) * mm, "mid": v(14.3, 10.1) * mm, "end": v(14.22, 10.12) * mm});
            skArc(sketch, "E224", {"start": v(14.22, 10.12) * mm, "mid": v(14.15, 10.14) * mm, "end": v(14.08, 10.16) * mm});
            skArc(sketch, "E225", {"start": v(14.08, 10.16) * mm, "mid": v(14.07, 10.17) * mm, "end": v(14.05, 10.16) * mm});
            skArc(sketch, "E226", {"start": v(14.05, 10.16) * mm, "mid": v(14.04, 10.14) * mm, "end": v(14.03, 10.11) * mm});
            skArc(sketch, "E227", {"start": v(14.03, 10.11) * mm, "mid": v(14.16, 9.43) * mm, "end": v(14.28, 8.74) * mm});
            skArc(sketch, "E228", {"start": v(14.28, 8.74) * mm, "mid": v(14.42, 7.98) * mm, "end": v(14.56, 7.21) * mm});
            skArc(sketch, "E229", {"start": v(14.56, 7.21) * mm, "mid": v(14.73, 6.3) * mm, "end": v(14.9, 5.4) * mm});
            skArc(sketch, "E230", {"start": v(14.9, 5.4) * mm, "mid": v(15.08, 4.43) * mm, "end": v(15.27, 3.45) * mm});
            skArc(sketch, "E231", {"start": v(15.27, 3.45) * mm, "mid": v(15.45, 2.47) * mm, "end": v(15.64, 1.5) * mm});
            skArc(sketch, "E232", {"start": v(15.64, 1.5) * mm, "mid": v(15.8, 0.63) * mm, "end": v(15.97, -0.23) * mm});
            skArc(sketch, "E233", {"start": v(15.97, -0.23) * mm, "mid": v(16.07, -0.77) * mm, "end": v(16.17, -1.3) * mm});
            skArc(sketch, "E234", {"start": v(16.17, -1.3) * mm, "mid": v(16.37, -2.39) * mm, "end": v(16.57, -3.47) * mm});
            skArc(sketch, "E235", {"start": v(16.57, -3.47) * mm, "mid": v(16.75, -4.46) * mm, "end": v(16.92, -5.44) * mm});
            skArc(sketch, "E236", {"start": v(16.92, -5.44) * mm, "mid": v(17.07, -6.3) * mm, "end": v(17.21, -7.15) * mm});
            skArc(sketch, "E237", {"start": v(17.21, -7.15) * mm, "mid": v(17.24, -7.35) * mm, "end": v(17.25, -7.56) * mm});
            skArc(sketch, "E238", {"start": v(17.25, -7.56) * mm, "mid": v(17.23, -7.72) * mm, "end": v(17.2, -7.87) * mm});
            skArc(sketch, "E239", {"start": v(17.2, -7.87) * mm, "mid": v(17.14, -8.04) * mm, "end": v(17.06, -8.2) * mm});
            skArc(sketch, "E240", {"start": v(17.06, -8.2) * mm, "mid": v(16.94, -8.4) * mm, "end": v(16.81, -8.57) * mm});
            skArc(sketch, "E241", {"start": v(16.81, -8.57) * mm, "mid": v(16.63, -8.78) * mm, "end": v(16.45, -8.98) * mm});
            skLineSegment(sketch, "E242", {"start": v(16.45, -8.98) * mm, "end": v(15.96, -9.5) * mm});
            skLineSegment(sketch, "E243", {"start": v(15.96, -9.5) * mm, "end": v(11.3, -9.47) * mm});
            skArc(sketch, "E244", {"start": v(11.3, -9.47) * mm, "mid": v(10.04, -9.46) * mm, "end": v(8.77, -9.45) * mm});
            skArc(sketch, "E245", {"start": v(8.77, -9.45) * mm, "mid": v(8.1, -9.44) * mm, "end": v(7.44, -9.43) * mm});
            skArc(sketch, "E246", {"start": v(7.44, -9.43) * mm, "mid": v(7.03, -9.42) * mm, "end": v(6.62, -9.4) * mm});
            skArc(sketch, "E247", {"start": v(6.62, -9.4) * mm, "mid": v(6.43, -9.38) * mm, "end": v(6.25, -9.34) * mm});
            skArc(sketch, "E248", {"start": v(6.25, -9.34) * mm, "mid": v(5.88, -9.2) * mm, "end": v(5.55, -9) * mm});
            skArc(sketch, "E249", {"start": v(5.55, -9) * mm, "mid": v(5.3, -8.74) * mm, "end": v(5.11, -8.44) * mm});
            skArc(sketch, "E250", {"start": v(5.11, -8.44) * mm, "mid": v(4.93, -7.94) * mm, "end": v(4.8, -7.42) * mm});
            skArc(sketch, "E251", {"start": v(4.8, -7.42) * mm, "mid": v(4.63, -6.34) * mm, "end": v(4.47, -5.26) * mm});
            skArc(sketch, "E252", {"start": v(4.47, -5.26) * mm, "mid": v(4.42, -4.9) * mm, "end": v(4.37, -4.55) * mm});
            skArc(sketch, "E253", {"start": v(4.37, -4.55) * mm, "mid": v(4.33, -4.24) * mm, "end": v(4.28, -3.93) * mm});
            skArc(sketch, "E254", {"start": v(4.28, -3.93) * mm, "mid": v(4.24, -3.67) * mm, "end": v(4.2, -3.4) * mm});
            skArc(sketch, "E255", {"start": v(4.2, -3.4) * mm, "mid": v(4.2, -3.36) * mm, "end": v(4.18, -3.31) * mm});
            skArc(sketch, "E256", {"start": v(4.18, -3.31) * mm, "mid": v(4.16, -3.27) * mm, "end": v(4.11, -3.24) * mm});
            skArc(sketch, "E257", {"start": v(4.11, -3.24) * mm, "mid": v(4.02, -3.22) * mm, "end": v(3.93, -3.21) * mm});
            skArc(sketch, "E258", {"start": v(3.93, -3.21) * mm, "mid": v(3.75, -3.2) * mm, "end": v(3.57, -3.2) * mm});
            skArc(sketch, "E259", {"start": v(3.57, -3.2) * mm, "mid": v(3.13, -3.2) * mm, "end": v(2.7, -3.2) * mm});
            skLineSegment(sketch, "E260", {"start": v(2.7, -3.2) * mm, "end": v(1.25, -3.23) * mm});
            skLineSegment(sketch, "E261", {"start": v(1.25, -3.23) * mm, "end": v(0.96, -5.19) * mm});
            skArc(sketch, "E262", {"start": v(0.96, -5.19) * mm, "mid": v(0.85, -5.94) * mm, "end": v(0.74, -6.7) * mm});
            skArc(sketch, "E263", {"start": v(0.74, -6.7) * mm, "mid": v(0.68, -7.06) * mm, "end": v(0.6, -7.42) * mm});
            skArc(sketch, "E264", {"start": v(0.6, -7.42) * mm, "mid": v(0.56, -7.66) * mm, "end": v(0.5, -7.88) * mm});
            skArc(sketch, "E265", {"start": v(0.5, -7.88) * mm, "mid": v(0.43, -8.08) * mm, "end": v(0.35, -8.27) * mm});
            skArc(sketch, "E266", {"start": v(0.35, -8.27) * mm, "mid": v(0.22, -8.51) * mm, "end": v(0.06, -8.74) * mm});
            skArc(sketch, "E267", {"start": v(0.06, -8.74) * mm, "mid": v(-0.11, -8.91) * mm, "end": v(-0.31, -9.06) * mm});
            skArc(sketch, "E268", {"start": v(-0.31, -9.06) * mm, "mid": v(-0.56, -9.19) * mm, "end": v(-0.82, -9.28) * mm});
            skArc(sketch, "E269", {"start": v(-0.82, -9.28) * mm, "mid": v(-1.16, -9.36) * mm, "end": v(-1.51, -9.42) * mm});
            skArc(sketch, "E270", {"start": v(-1.51, -9.42) * mm, "mid": v(-1.95, -9.46) * mm, "end": v(-2.4, -9.48) * mm});
            skArc(sketch, "E271", {"start": v(-2.4, -9.48) * mm, "mid": v(-3.99, -9.48) * mm, "end": v(-5.58, -9.49) * mm});
            skArc(sketch, "E272", {"start": v(-5.58, -9.49) * mm, "mid": v(-7.15, -9.48) * mm, "end": v(-8.73, -9.48) * mm});
            skArc(sketch, "E273", {"start": v(-8.73, -9.48) * mm, "mid": v(-9.25, -9.46) * mm, "end": v(-9.76, -9.42) * mm});
            skArc(sketch, "E274", {"start": v(-9.76, -9.42) * mm, "mid": v(-9.92, -9.4) * mm, "end": v(-10.08, -9.38) * mm});
            skArc(sketch, "E275", {"start": v(-10.08, -9.38) * mm, "mid": v(-10.23, -9.35) * mm, "end": v(-10.37, -9.32) * mm});
            skArc(sketch, "E276", {"start": v(-10.37, -9.32) * mm, "mid": v(-10.5, -9.28) * mm, "end": v(-10.64, -9.24) * mm});
            skArc(sketch, "E277", {"start": v(-10.64, -9.24) * mm, "mid": v(-10.76, -9.2) * mm, "end": v(-10.88, -9.15) * mm});
            skArc(sketch, "E278", {"start": v(-10.88, -9.15) * mm, "mid": v(-10.98, -9.1) * mm, "end": v(-11.08, -9.07) * mm});
            skArc(sketch, "E279", {"start": v(-11.08, -9.07) * mm, "mid": v(-11.18, -9.03) * mm, "end": v(-11.27, -9) * mm});
            skArc(sketch, "E280", {"start": v(-11.27, -9) * mm, "mid": v(-11.36, -8.96) * mm, "end": v(-11.45, -8.93) * mm});
            skArc(sketch, "E281", {"start": v(-11.45, -8.93) * mm, "mid": v(-11.5, -8.91) * mm, "end": v(-11.56, -8.9) * mm});
            skArc(sketch, "E282", {"start": v(-11.56, -8.9) * mm, "mid": v(-11.72, -8.88) * mm, "end": v(-11.88, -8.89) * mm});
            skArc(sketch, "E283", {"start": v(-11.88, -8.89) * mm, "mid": v(-12.24, -8.93) * mm, "end": v(-12.6, -8.98) * mm});
            skArc(sketch, "E284", {"start": v(-12.6, -8.98) * mm, "mid": v(-13.1, -9.06) * mm, "end": v(-13.6, -9.14) * mm});
            skArc(sketch, "E285", {"start": v(-13.6, -9.14) * mm, "mid": v(-14.31, -9.27) * mm, "end": v(-15.02, -9.41) * mm});
            skArc(sketch, "E286", {"start": v(-15.02, -9.41) * mm, "mid": v(-15.9, -9.58) * mm, "end": v(-16.78, -9.74) * mm});
            skArc(sketch, "E287", {"start": v(-16.78, -9.74) * mm, "mid": v(-17.32, -9.83) * mm, "end": v(-17.86, -9.9) * mm});
            skArc(sketch, "E288", {"start": v(-17.86, -9.9) * mm, "mid": v(-18.23, -9.93) * mm, "end": v(-18.6, -9.95) * mm});
            skArc(sketch, "E289", {"start": v(-18.6, -9.95) * mm, "mid": v(-18.9, -9.93) * mm, "end": v(-19.18, -9.89) * mm});
            skArc(sketch, "E290", {"start": v(-19.18, -9.89) * mm, "mid": v(-19.47, -9.78) * mm, "end": v(-19.72, -9.58) * mm});
            skArc(sketch, "E291", {"start": v(-19.72, -9.58) * mm, "mid": v(-20.05, -9.2) * mm, "end": v(-20.36, -8.79) * mm});
            skArc(sketch, "E292", {"start": v(-20.36, -8.79) * mm, "mid": v(-20.8, -8.12) * mm, "end": v(-21.2, -7.42) * mm});
            skArc(sketch, "E293", {"start": v(-21.2, -7.42) * mm, "mid": v(-21.86, -6.23) * mm, "end": v(-22.5, -5.03) * mm});
            skArc(sketch, "E294", {"start": v(-22.5, -5.03) * mm, "mid": v(-22.66, -4.74) * mm, "end": v(-22.82, -4.46) * mm});
            skArc(sketch, "E295", {"start": v(-22.82, -4.46) * mm, "mid": v(-22.95, -4.21) * mm, "end": v(-23.08, -3.97) * mm});
            skArc(sketch, "E296", {"start": v(-23.08, -3.97) * mm, "mid": v(-23.2, -3.75) * mm, "end": v(-23.32, -3.54) * mm});
            skArc(sketch, "E297", {"start": v(-23.32, -3.54) * mm, "mid": v(-23.33, -3.52) * mm, "end": v(-23.35, -3.5) * mm});
            skArc(sketch, "E298", {"start": v(-23.35, -3.5) * mm, "mid": v(-23.37, -3.5) * mm, "end": v(-23.38, -3.52) * mm});
            skArc(sketch, "E299", {"start": v(-23.38, -3.52) * mm, "mid": v(-23.53, -3.8) * mm, "end": v(-23.67, -4.07) * mm});
            skArc(sketch, "E300", {"start": v(-23.67, -4.07) * mm, "mid": v(-23.83, -4.39) * mm, "end": v(-24, -4.7) * mm});
            skArc(sketch, "E301", {"start": v(-24, -4.7) * mm, "mid": v(-24.18, -5.09) * mm, "end": v(-24.37, -5.47) * mm});
            skArc(sketch, "E302", {"start": v(-24.37, -5.47) * mm, "mid": v(-24.9, -6.56) * mm, "end": v(-25.46, -7.65) * mm});
            skArc(sketch, "E303", {"start": v(-25.46, -7.65) * mm, "mid": v(-25.79, -8.26) * mm, "end": v(-26.14, -8.85) * mm});
            skArc(sketch, "E304", {"start": v(-26.14, -8.85) * mm, "mid": v(-26.4, -9.2) * mm, "end": v(-26.68, -9.53) * mm});
            skArc(sketch, "E305", {"start": v(-26.68, -9.53) * mm, "mid": v(-26.9, -9.72) * mm, "end": v(-27.17, -9.83) * mm});
            skArc(sketch, "E306", {"start": v(-27.17, -9.83) * mm, "mid": v(-27.36, -9.87) * mm, "end": v(-27.55, -9.9) * mm});
            skArc(sketch, "E307", {"start": v(-27.55, -9.9) * mm, "mid": v(-27.83, -9.9) * mm, "end": v(-28.12, -9.9) * mm});
            skArc(sketch, "E308", {"start": v(-28.12, -9.9) * mm, "mid": v(-28.44, -9.9) * mm, "end": v(-28.76, -9.88) * mm});
            skArc(sketch, "E309", {"start": v(-28.76, -9.88) * mm, "mid": v(-29.08, -9.85) * mm, "end": v(-29.4, -9.8) * mm});
            skArc(sketch, "E310", {"start": v(-29.4, -9.8) * mm, "mid": v(-29.6, -9.77) * mm, "end": v(-29.8, -9.74) * mm});
            skArc(sketch, "E311", {"start": v(-29.8, -9.74) * mm, "mid": v(-30.16, -9.67) * mm, "end": v(-30.53, -9.6) * mm});
            skArc(sketch, "E312", {"start": v(-30.53, -9.6) * mm, "mid": v(-30.95, -9.52) * mm, "end": v(-31.37, -9.44) * mm});
            skArc(sketch, "E313", {"start": v(-31.37, -9.44) * mm, "mid": v(-31.8, -9.36) * mm, "end": v(-32.24, -9.27) * mm});
            skArc(sketch, "E314", {"start": v(-32.24, -9.27) * mm, "mid": v(-32.67, -9.19) * mm, "end": v(-33.1, -9.1) * mm});
            skArc(sketch, "E315", {"start": v(-33.1, -9.1) * mm, "mid": v(-33.49, -9.04) * mm, "end": v(-33.88, -8.97) * mm});
            skArc(sketch, "E316", {"start": v(-33.88, -8.97) * mm, "mid": v(-34.2, -8.91) * mm, "end": v(-34.54, -8.86) * mm});
            skArc(sketch, "E317", {"start": v(-34.54, -8.86) * mm, "mid": v(-34.67, -8.84) * mm, "end": v(-34.8, -8.84) * mm});
            skArc(sketch, "E318", {"start": v(-34.8, -8.84) * mm, "mid": v(-34.92, -8.84) * mm, "end": v(-35.04, -8.84) * mm});
            skArc(sketch, "E319", {"start": v(-35.04, -8.84) * mm, "mid": v(-35.12, -8.85) * mm, "end": v(-35.2, -8.86) * mm});
            skArc(sketch, "E320", {"start": v(-35.2, -8.86) * mm, "mid": v(-35.26, -8.88) * mm, "end": v(-35.32, -8.91) * mm});
            skArc(sketch, "E321", {"start": v(-35.32, -8.91) * mm, "mid": v(-35.39, -8.96) * mm, "end": v(-35.45, -9.02) * mm});
            skArc(sketch, "E322", {"start": v(-35.45, -9.02) * mm, "mid": v(-35.58, -9.11) * mm, "end": v(-35.72, -9.19) * mm});
            skArc(sketch, "E323", {"start": v(-35.72, -9.19) * mm, "mid": v(-35.88, -9.25) * mm, "end": v(-36.05, -9.3) * mm});
            skArc(sketch, "E324", {"start": v(-36.05, -9.3) * mm, "mid": v(-36.3, -9.34) * mm, "end": v(-36.54, -9.36) * mm});
            skArc(sketch, "E325", {"start": v(-36.54, -9.36) * mm, "mid": v(-36.96, -9.4) * mm, "end": v(-37.38, -9.42) * mm});
            skArc(sketch, "E326", {"start": v(-37.38, -9.42) * mm, "mid": v(-37.8, -9.44) * mm, "end": v(-38.21, -9.45) * mm});
            skArc(sketch, "E327", {"start": v(-38.21, -9.45) * mm, "mid": v(-40.33, -9.46) * mm, "end": v(-42.45, -9.47) * mm});
            skArc(sketch, "E328", {"start": v(-42.45, -9.47) * mm, "mid": v(-44.93, -9.48) * mm, "end": v(-47.4, -9.48) * mm});
            skArc(sketch, "E329", {"start": v(-47.4, -9.48) * mm, "mid": v(-50.24, -9.49) * mm, "end": v(-53.07, -9.49) * mm});
            skLineSegment(sketch, "E330", {"start": v(-53.07, -9.49) * mm, "end": v(-67.63, -9.5) * mm});
            skLineSegment(sketch, "E331", {"start": v(-67.63, -9.5) * mm, "end": v(-68.2, -8.91) * mm});
            skLineSegment(sketch, "E332", {"start": v(-68.2, -8.91) * mm, "end": v(-68.78, -8.34) * mm});
            skLineSegment(sketch, "E333", {"start": v(-68.78, -8.34) * mm, "end": v(-68.78, -4.15) * mm});
            skLineSegment(sketch, "E334", {"start": v(-68.78, -4.15) * mm, "end": v(-68.78, 0.03) * mm});
            skLineSegment(sketch, "E335", {"start": v(-68.78, 0.03) * mm, "end": v(-70.07, 0.03) * mm});
            skLineSegment(sketch, "E336", {"start": v(-70.07, 0.03) * mm, "end": v(-71.35, 0.03) * mm});
            skLineSegment(sketch, "E337", {"start": v(-71.35, 0.03) * mm, "end": v(-71.4, -3.14) * mm});
            skArc(sketch, "E338", {"start": v(-71.4, -3.14) * mm, "mid": v(-71.42, -4.4) * mm, "end": v(-71.45, -5.67) * mm});
            skArc(sketch, "E339", {"start": v(-71.45, -5.67) * mm, "mid": v(-71.48, -6.35) * mm, "end": v(-71.53, -7.04) * mm});
            skArc(sketch, "E340", {"start": v(-71.53, -7.04) * mm, "mid": v(-71.59, -7.48) * mm, "end": v(-71.67, -7.92) * mm});
            skArc(sketch, "E341", {"start": v(-71.67, -7.92) * mm, "mid": v(-71.77, -8.26) * mm, "end": v(-71.9, -8.58) * mm});
            skArc(sketch, "E342", {"start": v(-71.9, -8.58) * mm, "mid": v(-71.97, -8.7) * mm, "end": v(-72.05, -8.83) * mm});
            skArc(sketch, "E343", {"start": v(-72.05, -8.83) * mm, "mid": v(-72.12, -8.93) * mm, "end": v(-72.2, -9.03) * mm});
            skArc(sketch, "E344", {"start": v(-72.2, -9.03) * mm, "mid": v(-72.3, -9.1) * mm, "end": v(-72.39, -9.17) * mm});
            skArc(sketch, "E345", {"start": v(-72.39, -9.17) * mm, "mid": v(-72.48, -9.23) * mm, "end": v(-72.59, -9.28) * mm});
            skArc(sketch, "E346", {"start": v(-72.59, -9.28) * mm, "mid": v(-72.83, -9.35) * mm, "end": v(-73.09, -9.38) * mm});
            skArc(sketch, "E347", {"start": v(-73.09, -9.38) * mm, "mid": v(-73.7, -9.42) * mm, "end": v(-74.33, -9.45) * mm});
            skArc(sketch, "E348", {"start": v(-74.33, -9.45) * mm, "mid": v(-75.18, -9.47) * mm, "end": v(-76.04, -9.48) * mm});
            skArc(sketch, "E349", {"start": v(-76.04, -9.48) * mm, "mid": v(-77.24, -9.48) * mm, "end": v(-78.44, -9.48) * mm});
            skArc(sketch, "E350", {"start": v(-78.44, -9.48) * mm, "mid": v(-79.62, -9.47) * mm, "end": v(-80.79, -9.46) * mm});
            skArc(sketch, "E351", {"start": v(-80.79, -9.46) * mm, "mid": v(-81.22, -9.45) * mm, "end": v(-81.66, -9.44) * mm});
            skArc(sketch, "E352", {"start": v(-81.66, -9.44) * mm, "mid": v(-81.9, -9.42) * mm, "end": v(-82.13, -9.4) * mm});
            skArc(sketch, "E353", {"start": v(-82.13, -9.4) * mm, "mid": v(-82.29, -9.36) * mm, "end": v(-82.43, -9.31) * mm});
            skArc(sketch, "E354", {"start": v(-82.43, -9.31) * mm, "mid": v(-82.58, -9.23) * mm, "end": v(-82.72, -9.13) * mm});
            skArc(sketch, "E355", {"start": v(-82.72, -9.13) * mm, "mid": v(-82.86, -9.02) * mm, "end": v(-82.98, -8.89) * mm});
            skArc(sketch, "E356", {"start": v(-82.98, -8.89) * mm, "mid": v(-83.11, -8.73) * mm, "end": v(-83.22, -8.56) * mm});
            skArc(sketch, "E357", {"start": v(-83.22, -8.56) * mm, "mid": v(-83.34, -8.37) * mm, "end": v(-83.44, -8.16) * mm});
            skLineSegment(sketch, "E358", {"start": v(-83.44, -8.16) * mm, "end": v(-83.66, -7.7) * mm});
            skLineSegment(sketch, "E359", {"start": v(-83.66, -7.7) * mm, "end": v(-83.68, 1.7) * mm});
            skArc(sketch, "E360", {"start": v(-83.68, 1.7) * mm, "mid": v(-83.69, 3.67) * mm, "end": v(-83.69, 5.63) * mm});
            skArc(sketch, "E361", {"start": v(-83.69, 5.63) * mm, "mid": v(-83.69, 7.62) * mm, "end": v(-83.68, 9.62) * mm});
            skArc(sketch, "E362", {"start": v(-83.68, 9.62) * mm, "mid": v(-83.68, 11.38) * mm, "end": v(-83.67, 13.15) * mm});
            skArc(sketch, "E363", {"start": v(-83.67, 13.15) * mm, "mid": v(-83.67, 14.28) * mm, "end": v(-83.66, 15.41) * mm});
            skLineSegment(sketch, "E364", {"start": v(-83.66, 15.41) * mm, "end": v(-83.6, 19.7) * mm});
            skLineSegment(sketch, "E365", {"start": v(-83.6, 19.7) * mm, "end": v(-82.86, 20.37) * mm});
            skLineSegment(sketch, "E366", {"start": v(-82.86, 20.37) * mm, "end": v(-82.12, 21.04) * mm});
            skLineSegment(sketch, "E367", {"start": v(-82.12, 21.04) * mm, "end": v(-78.02, 21.01) * mm});
            skArc(sketch, "E368", {"start": v(-78.02, 21.01) * mm, "mid": v(-76.72, 21) * mm, "end": v(-75.42, 21) * mm});
            skArc(sketch, "E369", {"start": v(-75.42, 21) * mm, "mid": v(-74.92, 20.98) * mm, "end": v(-74.42, 20.97) * mm});
            skArc(sketch, "E370", {"start": v(-74.42, 20.97) * mm, "mid": v(-74.13, 20.95) * mm, "end": v(-73.83, 20.92) * mm});
            skArc(sketch, "E371", {"start": v(-73.83, 20.92) * mm, "mid": v(-73.6, 20.88) * mm, "end": v(-73.37, 20.83) * mm});
            skArc(sketch, "E372", {"start": v(-73.37, 20.83) * mm, "mid": v(-73.06, 20.73) * mm, "end": v(-72.75, 20.6) * mm});
            skArc(sketch, "E373", {"start": v(-72.75, 20.6) * mm, "mid": v(-72.53, 20.47) * mm, "end": v(-72.33, 20.3) * mm});
            skArc(sketch, "E374", {"start": v(-72.33, 20.3) * mm, "mid": v(-72.17, 20.11) * mm, "end": v(-72.04, 19.9) * mm});
            skArc(sketch, "E375", {"start": v(-72.04, 19.9) * mm, "mid": v(-71.92, 19.59) * mm, "end": v(-71.82, 19.28) * mm});
            skArc(sketch, "E376", {"start": v(-71.82, 19.28) * mm, "mid": v(-71.78, 19.08) * mm, "end": v(-71.76, 18.89) * mm});
            skArc(sketch, "E377", {"start": v(-71.76, 18.89) * mm, "mid": v(-71.73, 18.56) * mm, "end": v(-71.72, 18.24) * mm});
            skArc(sketch, "E378", {"start": v(-71.72, 18.24) * mm, "mid": v(-71.7, 17.7) * mm, "end": v(-71.7, 17.17) * mm});
            skArc(sketch, "E379", {"start": v(-71.7, 17.17) * mm, "mid": v(-71.68, 16.1) * mm, "end": v(-71.67, 15.03) * mm});
            skLineSegment(sketch, "E380", {"start": v(-71.67, 15.03) * mm, "end": v(-71.64, 11.23) * mm});
            skLineSegment(sketch, "E381", {"start": v(-71.64, 11.23) * mm, "end": v(-70.23, 11.25) * mm});
            skLineSegment(sketch, "E382", {"start": v(-70.23, 11.25) * mm, "end": v(-68.82, 11.26) * mm});
            skLineSegment(sketch, "E383", {"start": v(-68.82, 11.26) * mm, "end": v(-68.78, 15.04) * mm});
            skArc(sketch, "E384", {"start": v(-68.78, 15.04) * mm, "mid": v(-68.77, 16.08) * mm, "end": v(-68.75, 17.1) * mm});
            skArc(sketch, "E385", {"start": v(-68.75, 17.1) * mm, "mid": v(-68.74, 17.66) * mm, "end": v(-68.72, 18.21) * mm});
            skArc(sketch, "E386", {"start": v(-68.72, 18.21) * mm, "mid": v(-68.7, 18.56) * mm, "end": v(-68.68, 18.9) * mm});
            skArc(sketch, "E387", {"start": v(-68.68, 18.9) * mm, "mid": v(-68.66, 19.1) * mm, "end": v(-68.62, 19.31) * mm});
            skArc(sketch, "E388", {"start": v(-68.62, 19.31) * mm, "mid": v(-68.56, 19.55) * mm, "end": v(-68.48, 19.78) * mm});
            skArc(sketch, "E389", {"start": v(-68.48, 19.78) * mm, "mid": v(-68.4, 19.97) * mm, "end": v(-68.3, 20.14) * mm});
            skArc(sketch, "E390", {"start": v(-68.3, 20.14) * mm, "mid": v(-68.18, 20.29) * mm, "end": v(-68.05, 20.42) * mm});
            skArc(sketch, "E391", {"start": v(-68.05, 20.42) * mm, "mid": v(-67.9, 20.53) * mm, "end": v(-67.73, 20.62) * mm});
            skLineSegment(sketch, "E392", {"start": v(-67.73, 20.62) * mm, "end": v(-67.35, 20.82) * mm});
            skLineSegment(sketch, "E393", {"start": v(-67.35, 20.82) * mm, "end": v(-64.86, 20.89) * mm});
            skArc(sketch, "E394", {"start": v(-64.86, 20.89) * mm, "mid": v(-61.49, 20.97) * mm, "end": v(-58.1, 21.01) * mm});
            skArc(sketch, "E395", {"start": v(-58.1, 21.01) * mm, "mid": v(-53.33, 21.05) * mm, "end": v(-48.56, 21.07) * mm});
            skArc(sketch, "E396", {"start": v(-48.56, 21.07) * mm, "mid": v(-43.64, 21.08) * mm, "end": v(-38.73, 21.08) * mm});
            skArc(sketch, "E397", {"start": v(-38.73, 21.08) * mm, "mid": v(-37.67, 21.04) * mm, "end": v(-36.62, 20.95) * mm});
            skArc(sketch, "E398", {"start": v(-36.62, 20.95) * mm, "mid": v(-36.28, 20.92) * mm, "end": v(-35.94, 20.91) * mm});
            skArc(sketch, "E399", {"start": v(-35.94, 20.91) * mm, "mid": v(-35.42, 20.92) * mm, "end": v(-34.9, 20.94) * mm});
            skArc(sketch, "E400", {"start": v(-34.9, 20.94) * mm, "mid": v(-34.14, 20.98) * mm, "end": v(-33.4, 21.03) * mm});
            skArc(sketch, "E401", {"start": v(-33.4, 21.03) * mm, "mid": v(-32.26, 21.12) * mm, "end": v(-31.12, 21.2) * mm});
            skArc(sketch, "E402", {"start": v(-31.12, 21.2) * mm, "mid": v(-30.2, 21.28) * mm, "end": v(-29.28, 21.35) * mm});
            skArc(sketch, "E403", {"start": v(-29.28, 21.35) * mm, "mid": v(-28.55, 21.39) * mm, "end": v(-27.82, 21.42) * mm});
            skArc(sketch, "E404", {"start": v(-27.82, 21.42) * mm, "mid": v(-27.27, 21.44) * mm, "end": v(-26.7, 21.45) * mm});
            skArc(sketch, "E405", {"start": v(-26.7, 21.45) * mm, "mid": v(-26.48, 21.43) * mm, "end": v(-26.25, 21.39) * mm});
            skArc(sketch, "E406", {"start": v(-26.25, 21.39) * mm, "mid": v(-26.01, 21.29) * mm, "end": v(-25.81, 21.13) * mm});
            skArc(sketch, "E407", {"start": v(-25.81, 21.13) * mm, "mid": v(-25.57, 20.87) * mm, "end": v(-25.35, 20.58) * mm});
            skArc(sketch, "E408", {"start": v(-25.35, 20.58) * mm, "mid": v(-25.05, 20.11) * mm, "end": v(-24.77, 19.63) * mm});
            skArc(sketch, "E409", {"start": v(-24.77, 19.63) * mm, "mid": v(-24.33, 18.8) * mm, "end": v(-23.9, 17.98) * mm});
            skArc(sketch, "E410", {"start": v(-23.9, 17.98) * mm, "mid": v(-23.77, 17.7) * mm, "end": v(-23.62, 17.43) * mm});
            skArc(sketch, "E411", {"start": v(-23.62, 17.43) * mm, "mid": v(-23.5, 17.2) * mm, "end": v(-23.38, 16.97) * mm});
            skArc(sketch, "E412", {"start": v(-23.38, 16.97) * mm, "mid": v(-23.27, 16.77) * mm, "end": v(-23.16, 16.57) * mm});
            skArc(sketch, "E413", {"start": v(-23.16, 16.57) * mm, "mid": v(-23.15, 16.55) * mm, "end": v(-23.14, 16.55) * mm});
            skArc(sketch, "E414", {"start": v(-23.14, 16.55) * mm, "mid": v(-23.12, 16.55) * mm, "end": v(-23.11, 16.57) * mm});
            skArc(sketch, "E415", {"start": v(-23.11, 16.57) * mm, "mid": v(-23, 16.79) * mm, "end": v(-22.9, 17) * mm});
            skArc(sketch, "E416", {"start": v(-22.9, 17) * mm, "mid": v(-22.8, 17.26) * mm, "end": v(-22.68, 17.5) * mm});
            skArc(sketch, "E417", {"start": v(-22.68, 17.5) * mm, "mid": v(-22.54, 17.8) * mm, "end": v(-22.41, 18.1) * mm});
            skArc(sketch, "E418", {"start": v(-22.41, 18.1) * mm, "mid": v(-22.27, 18.42) * mm, "end": v(-22.13, 18.74) * mm});
            skArc(sketch, "E419", {"start": v(-22.13, 18.74) * mm, "mid": v(-22, 19.05) * mm, "end": v(-21.86, 19.35) * mm});
            skArc(sketch, "E420", {"start": v(-21.86, 19.35) * mm, "mid": v(-21.74, 19.62) * mm, "end": v(-21.63, 19.88) * mm});
            skArc(sketch, "E421", {"start": v(-21.63, 19.88) * mm, "mid": v(-21.56, 20.02) * mm, "end": v(-21.5, 20.17) * mm});
            skArc(sketch, "E422", {"start": v(-21.5, 20.17) * mm, "mid": v(-21.36, 20.43) * mm, "end": v(-21.2, 20.67) * mm});
            skArc(sketch, "E423", {"start": v(-21.2, 20.67) * mm, "mid": v(-21.04, 20.9) * mm, "end": v(-20.84, 21.1) * mm});
            skArc(sketch, "E424", {"start": v(-20.84, 21.1) * mm, "mid": v(-20.64, 21.26) * mm, "end": v(-20.42, 21.4) * mm});
            skArc(sketch, "E425", {"start": v(-20.42, 21.4) * mm, "mid": v(-20.2, 21.52) * mm, "end": v(-19.96, 21.6) * mm});
            skArc(sketch, "E426", {"start": v(-19.96, 21.6) * mm, "mid": v(-19.78, 21.63) * mm, "end": v(-19.6, 21.64) * mm});
            skArc(sketch, "E427", {"start": v(-19.6, 21.64) * mm, "mid": v(-19.2, 21.63) * mm, "end": v(-18.8, 21.61) * mm});
            skArc(sketch, "E428", {"start": v(-18.8, 21.61) * mm, "mid": v(-18.27, 21.58) * mm, "end": v(-17.74, 21.54) * mm});
            skArc(sketch, "E429", {"start": v(-17.74, 21.54) * mm, "mid": v(-17.06, 21.48) * mm, "end": v(-16.39, 21.41) * mm});
            skArc(sketch, "E430", {"start": v(38.81, -12.33) * mm, "mid": v(38.94, -12.43) * mm, "end": v(39.06, -12.55) * mm});
            skArc(sketch, "E431", {"start": v(39.06, -12.55) * mm, "mid": v(39.2, -12.72) * mm, "end": v(39.34, -12.89) * mm});
            skArc(sketch, "E432", {"start": v(39.34, -12.89) * mm, "mid": v(39.48, -13.07) * mm, "end": v(39.6, -13.26) * mm});
            skArc(sketch, "E433", {"start": v(39.6, -13.26) * mm, "mid": v(39.71, -13.44) * mm, "end": v(39.8, -13.62) * mm});
            skArc(sketch, "E434", {"start": v(39.8, -13.62) * mm, "mid": v(39.87, -13.75) * mm, "end": v(39.92, -13.88) * mm});
            skArc(sketch, "E435", {"start": v(39.92, -13.88) * mm, "mid": v(39.96, -13.98) * mm, "end": v(39.99, -14.08) * mm});
            skArc(sketch, "E436", {"start": v(39.99, -14.08) * mm, "mid": v(40, -14.18) * mm, "end": v(40.02, -14.29) * mm});
            skArc(sketch, "E437", {"start": v(40.02, -14.29) * mm, "mid": v(40.03, -14.43) * mm, "end": v(40.03, -14.56) * mm});
            skArc(sketch, "E438", {"start": v(40.03, -14.56) * mm, "mid": v(40.01, -14.85) * mm, "end": v(39.96, -15.13) * mm});
            skArc(sketch, "E439", {"start": v(39.96, -15.13) * mm, "mid": v(39.87, -15.35) * mm, "end": v(39.75, -15.55) * mm});
            skArc(sketch, "E440", {"start": v(39.75, -15.55) * mm, "mid": v(39.57, -15.74) * mm, "end": v(39.36, -15.88) * mm});
            skArc(sketch, "E441", {"start": v(39.36, -15.88) * mm, "mid": v(39.07, -16.02) * mm, "end": v(38.77, -16.14) * mm});
            skArc(sketch, "E442", {"start": v(38.77, -16.14) * mm, "mid": v(38.53, -16.23) * mm, "end": v(38.3, -16.34) * mm});
            skArc(sketch, "E443", {"start": v(38.3, -16.34) * mm, "mid": v(38.16, -16.44) * mm, "end": v(38.05, -16.58) * mm});
            skArc(sketch, "E444", {"start": v(38.05, -16.58) * mm, "mid": v(37.99, -16.71) * mm, "end": v(37.98, -16.86) * mm});
            skArc(sketch, "E445", {"start": v(37.98, -16.86) * mm, "mid": v(38, -17.05) * mm, "end": v(38.07, -17.22) * mm});
            skArc(sketch, "E446", {"start": v(38.07, -17.22) * mm, "mid": v(38.1, -17.28) * mm, "end": v(38.14, -17.34) * mm});
            skArc(sketch, "E447", {"start": v(38.14, -17.34) * mm, "mid": v(38.22, -17.45) * mm, "end": v(38.3, -17.55) * mm});
            skArc(sketch, "E448", {"start": v(38.3, -17.55) * mm, "mid": v(38.4, -17.67) * mm, "end": v(38.5, -17.8) * mm});
            skArc(sketch, "E449", {"start": v(38.5, -17.8) * mm, "mid": v(38.6, -17.92) * mm, "end": v(38.71, -18.04) * mm});
            skArc(sketch, "E450", {"start": v(38.71, -18.04) * mm, "mid": v(38.95, -18.31) * mm, "end": v(39.19, -18.6) * mm});
            skArc(sketch, "E451", {"start": v(39.19, -18.6) * mm, "mid": v(39.36, -18.82) * mm, "end": v(39.52, -19.05) * mm});
            skArc(sketch, "E452", {"start": v(39.52, -19.05) * mm, "mid": v(39.63, -19.23) * mm, "end": v(39.72, -19.43) * mm});
            skArc(sketch, "E453", {"start": v(39.72, -19.43) * mm, "mid": v(39.77, -19.56) * mm, "end": v(39.78, -19.7) * mm});
            skArc(sketch, "E454", {"start": v(39.78, -19.7) * mm, "mid": v(39.74, -20.03) * mm, "end": v(39.62, -20.33) * mm});
            skArc(sketch, "E455", {"start": v(39.62, -20.33) * mm, "mid": v(39.4, -20.65) * mm, "end": v(39.14, -20.94) * mm});
            skArc(sketch, "E456", {"start": v(39.14, -20.94) * mm, "mid": v(38.83, -21.2) * mm, "end": v(38.48, -21.4) * mm});
            skArc(sketch, "E457", {"start": v(38.48, -21.4) * mm, "mid": v(38.16, -21.52) * mm, "end": v(37.82, -21.56) * mm});
            skArc(sketch, "E458", {"start": v(37.82, -21.56) * mm, "mid": v(37.72, -21.56) * mm, "end": v(37.62, -21.55) * mm});
            skArc(sketch, "E459", {"start": v(37.62, -21.55) * mm, "mid": v(37.54, -21.53) * mm, "end": v(37.46, -21.5) * mm});
            skArc(sketch, "E460", {"start": v(37.46, -21.5) * mm, "mid": v(37.36, -21.46) * mm, "end": v(37.27, -21.4) * mm});
            skArc(sketch, "E461", {"start": v(37.27, -21.4) * mm, "mid": v(37.13, -21.31) * mm, "end": v(36.98, -21.22) * mm});
            skArc(sketch, "E462", {"start": v(36.98, -21.22) * mm, "mid": v(36.86, -21.13) * mm, "end": v(36.75, -21.05) * mm});
            skArc(sketch, "E463", {"start": v(36.75, -21.05) * mm, "mid": v(36.6, -20.93) * mm, "end": v(36.45, -20.81) * mm});
            skArc(sketch, "E464", {"start": v(36.45, -20.81) * mm, "mid": v(36.3, -20.69) * mm, "end": v(36.16, -20.56) * mm});
            skArc(sketch, "E465", {"start": v(36.16, -20.56) * mm, "mid": v(36.03, -20.45) * mm, "end": v(35.9, -20.33) * mm});
            skLineSegment(sketch, "E466", {"start": v(35.9, -20.33) * mm, "end": v(35.33, -19.78) * mm});
            skLineSegment(sketch, "E467", {"start": v(35.33, -19.78) * mm, "end": v(34.95, -20.07) * mm});
            skArc(sketch, "E468", {"start": v(34.95, -20.07) * mm, "mid": v(34.56, -20.35) * mm, "end": v(34.16, -20.61) * mm});
            skArc(sketch, "E469", {"start": v(34.16, -20.61) * mm, "mid": v(33.73, -20.87) * mm, "end": v(33.3, -21.12) * mm});
            skArc(sketch, "E470", {"start": v(33.3, -21.12) * mm, "mid": v(32.9, -21.32) * mm, "end": v(32.5, -21.5) * mm});
            skArc(sketch, "E471", {"start": v(32.5, -21.5) * mm, "mid": v(32.3, -21.58) * mm, "end": v(32.09, -21.6) * mm});
            skArc(sketch, "E472", {"start": v(32.09, -21.6) * mm, "mid": v(31.85, -21.58) * mm, "end": v(31.62, -21.5) * mm});
            skArc(sketch, "E473", {"start": v(31.62, -21.5) * mm, "mid": v(31.38, -21.37) * mm, "end": v(31.16, -21.2) * mm});
            skArc(sketch, "E474", {"start": v(31.16, -21.2) * mm, "mid": v(30.95, -21) * mm, "end": v(30.76, -20.78) * mm});
            skArc(sketch, "E475", {"start": v(30.76, -20.78) * mm, "mid": v(30.62, -20.53) * mm, "end": v(30.51, -20.27) * mm});
            skArc(sketch, "E476", {"start": v(30.51, -20.27) * mm, "mid": v(30.46, -20.1) * mm, "end": v(30.42, -19.92) * mm});
            skArc(sketch, "E477", {"start": v(30.42, -19.92) * mm, "mid": v(30.4, -19.74) * mm, "end": v(30.39, -19.55) * mm});
            skArc(sketch, "E478", {"start": v(30.39, -19.55) * mm, "mid": v(30.39, -19.38) * mm, "end": v(30.4, -19.21) * mm});
            skArc(sketch, "E479", {"start": v(30.4, -19.21) * mm, "mid": v(30.42, -19.1) * mm, "end": v(30.47, -18.98) * mm});
            skArc(sketch, "E480", {"start": v(30.47, -18.98) * mm, "mid": v(30.55, -18.86) * mm, "end": v(30.65, -18.76) * mm});
            skArc(sketch, "E481", {"start": v(30.65, -18.76) * mm, "mid": v(30.88, -18.58) * mm, "end": v(31.1, -18.4) * mm});
            skArc(sketch, "E482", {"start": v(31.1, -18.4) * mm, "mid": v(31.42, -18.17) * mm, "end": v(31.75, -17.94) * mm});
            skArc(sketch, "E483", {"start": v(31.75, -17.94) * mm, "mid": v(32.2, -17.65) * mm, "end": v(32.64, -17.36) * mm});
            skLineSegment(sketch, "E484", {"start": v(32.64, -17.36) * mm, "end": v(33.72, -16.67) * mm});
            skLineSegment(sketch, "E485", {"start": v(33.72, -16.67) * mm, "end": v(33.2, -16.61) * mm});
            skArc(sketch, "E486", {"start": v(33.2, -16.61) * mm, "mid": v(32.8, -16.56) * mm, "end": v(32.4, -16.5) * mm});
            skArc(sketch, "E487", {"start": v(32.4, -16.5) * mm, "mid": v(32.12, -16.43) * mm, "end": v(31.87, -16.32) * mm});
            skArc(sketch, "E488", {"start": v(31.87, -16.32) * mm, "mid": v(31.68, -16.2) * mm, "end": v(31.5, -16.06) * mm});
            skArc(sketch, "E489", {"start": v(31.5, -16.06) * mm, "mid": v(31.36, -15.88) * mm, "end": v(31.24, -15.68) * mm});
            skArc(sketch, "E490", {"start": v(31.24, -15.68) * mm, "mid": v(31.2, -15.59) * mm, "end": v(31.16, -15.49) * mm});
            skArc(sketch, "E491", {"start": v(31.16, -15.49) * mm, "mid": v(31.14, -15.4) * mm, "end": v(31.11, -15.3) * mm});
            skArc(sketch, "E492", {"start": v(31.11, -15.3) * mm, "mid": v(31.1, -15.2) * mm, "end": v(31.09, -15.1) * mm});
            skArc(sketch, "E493", {"start": v(31.09, -15.1) * mm, "mid": v(31.08, -14.95) * mm, "end": v(31.08, -14.82) * mm});
            skArc(sketch, "E494", {"start": v(31.08, -14.82) * mm, "mid": v(31.09, -14.53) * mm, "end": v(31.13, -14.25) * mm});
            skArc(sketch, "E495", {"start": v(31.13, -14.25) * mm, "mid": v(31.2, -14.03) * mm, "end": v(31.32, -13.83) * mm});
            skArc(sketch, "E496", {"start": v(31.32, -13.83) * mm, "mid": v(31.47, -13.66) * mm, "end": v(31.66, -13.53) * mm});
            skArc(sketch, "E497", {"start": v(31.66, -13.53) * mm, "mid": v(31.9, -13.4) * mm, "end": v(32.17, -13.3) * mm});
            skArc(sketch, "E498", {"start": v(32.17, -13.3) * mm, "mid": v(32.32, -13.27) * mm, "end": v(32.47, -13.24) * mm});
            skArc(sketch, "E499", {"start": v(32.47, -13.24) * mm, "mid": v(32.67, -13.2) * mm, "end": v(32.88, -13.18) * mm});
            skArc(sketch, "E500", {"start": v(32.88, -13.18) * mm, "mid": v(33.2, -13.14) * mm, "end": v(33.53, -13.1) * mm});
            skArc(sketch, "E501", {"start": v(33.53, -13.1) * mm, "mid": v(34.12, -13.05) * mm, "end": v(34.71, -13) * mm});
            skArc(sketch, "E502", {"start": v(34.71, -13) * mm, "mid": v(35, -12.96) * mm, "end": v(35.28, -12.92) * mm});
            skArc(sketch, "E503", {"start": v(35.28, -12.92) * mm, "mid": v(35.5, -12.89) * mm, "end": v(35.73, -12.84) * mm});
            skArc(sketch, "E504", {"start": v(35.73, -12.84) * mm, "mid": v(35.94, -12.78) * mm, "end": v(36.15, -12.72) * mm});
            skArc(sketch, "E505", {"start": v(36.15, -12.72) * mm, "mid": v(36.39, -12.63) * mm, "end": v(36.63, -12.54) * mm});
            skArc(sketch, "E506", {"start": v(36.63, -12.54) * mm, "mid": v(36.95, -12.41) * mm, "end": v(37.29, -12.3) * mm});
            skArc(sketch, "E507", {"start": v(37.29, -12.3) * mm, "mid": v(37.6, -12.24) * mm, "end": v(37.93, -12.2) * mm});
            skArc(sketch, "E508", {"start": v(37.93, -12.2) * mm, "mid": v(38.2, -12.18) * mm, "end": v(38.47, -12.2) * mm});
            skArc(sketch, "E509", {"start": v(38.47, -12.2) * mm, "mid": v(38.65, -12.24) * mm, "end": v(38.81, -12.33) * mm});
            skArc(sketch, "E510", {"start": v(-23.74, -12.98) * mm, "mid": v(-23.68, -13.01) * mm, "end": v(-23.62, -13.05) * mm});
            skArc(sketch, "E511", {"start": v(-23.62, -13.05) * mm, "mid": v(-23.56, -13.09) * mm, "end": v(-23.5, -13.13) * mm});
            skArc(sketch, "E512", {"start": v(-23.5, -13.13) * mm, "mid": v(-23.43, -13.17) * mm, "end": v(-23.38, -13.22) * mm});
            skArc(sketch, "E513", {"start": v(-23.38, -13.22) * mm, "mid": v(-23.33, -13.26) * mm, "end": v(-23.3, -13.3) * mm});
            skArc(sketch, "E514", {"start": v(-23.3, -13.3) * mm, "mid": v(-23.2, -13.37) * mm, "end": v(-23.11, -13.43) * mm});
            skArc(sketch, "E515", {"start": v(-23.11, -13.43) * mm, "mid": v(-23.01, -13.46) * mm, "end": v(-22.9, -13.47) * mm});
            skArc(sketch, "E516", {"start": v(-22.9, -13.47) * mm, "mid": v(-22.78, -13.46) * mm, "end": v(-22.65, -13.42) * mm});
            skArc(sketch, "E517", {"start": v(-22.65, -13.42) * mm, "mid": v(-22.48, -13.35) * mm, "end": v(-22.3, -13.27) * mm});
            skArc(sketch, "E518", {"start": v(-22.3, -13.27) * mm, "mid": v(-22.22, -13.23) * mm, "end": v(-22.13, -13.2) * mm});
            skArc(sketch, "E519", {"start": v(-22.13, -13.2) * mm, "mid": v(-22.05, -13.16) * mm, "end": v(-21.96, -13.12) * mm});
            skArc(sketch, "E520", {"start": v(-21.96, -13.12) * mm, "mid": v(-21.88, -13.1) * mm, "end": v(-21.8, -13.07) * mm});
            skArc(sketch, "E521", {"start": v(-21.8, -13.07) * mm, "mid": v(-21.76, -13.06) * mm, "end": v(-21.7, -13.06) * mm});
            skArc(sketch, "E522", {"start": v(-21.7, -13.06) * mm, "mid": v(-21.44, -13.1) * mm, "end": v(-21.2, -13.2) * mm});
            skArc(sketch, "E523", {"start": v(-21.2, -13.2) * mm, "mid": v(-20.77, -13.48) * mm, "end": v(-20.36, -13.77) * mm});
            skArc(sketch, "E524", {"start": v(-20.36, -13.77) * mm, "mid": v(-19.93, -14.12) * mm, "end": v(-19.52, -14.48) * mm});
            skArc(sketch, "E525", {"start": v(-19.52, -14.48) * mm, "mid": v(-19.2, -14.82) * mm, "end": v(-18.9, -15.19) * mm});
            skArc(sketch, "E526", {"start": v(-18.9, -15.19) * mm, "mid": v(-18.83, -15.28) * mm, "end": v(-18.77, -15.37) * mm});
            skArc(sketch, "E527", {"start": v(-18.77, -15.37) * mm, "mid": v(-18.71, -15.48) * mm, "end": v(-18.65, -15.59) * mm});
            skArc(sketch, "E528", {"start": v(-18.65, -15.59) * mm, "mid": v(-18.6, -15.7) * mm, "end": v(-18.55, -15.8) * mm});
            skArc(sketch, "E529", {"start": v(-18.55, -15.8) * mm, "mid": v(-18.51, -15.88) * mm, "end": v(-18.49, -15.97) * mm});
            skArc(sketch, "E530", {"start": v(-18.49, -15.97) * mm, "mid": v(-18.44, -16.15) * mm, "end": v(-18.42, -16.33) * mm});
            skArc(sketch, "E531", {"start": v(-18.42, -16.33) * mm, "mid": v(-18.43, -16.49) * mm, "end": v(-18.46, -16.64) * mm});
            skArc(sketch, "E532", {"start": v(-18.46, -16.64) * mm, "mid": v(-18.52, -16.8) * mm, "end": v(-18.6, -16.95) * mm});
            skArc(sketch, "E533", {"start": v(-18.6, -16.95) * mm, "mid": v(-18.73, -17.13) * mm, "end": v(-18.88, -17.3) * mm});
            skArc(sketch, "E534", {"start": v(-18.88, -17.3) * mm, "mid": v(-18.95, -17.37) * mm, "end": v(-19.01, -17.45) * mm});
            skArc(sketch, "E535", {"start": v(-19.01, -17.45) * mm, "mid": v(-19.07, -17.52) * mm, "end": v(-19.12, -17.59) * mm});
            skArc(sketch, "E536", {"start": v(-19.12, -17.59) * mm, "mid": v(-19.17, -17.65) * mm, "end": v(-19.21, -17.7) * mm});
            skArc(sketch, "E537", {"start": v(-19.21, -17.7) * mm, "mid": v(-19.22, -17.73) * mm, "end": v(-19.22, -17.75) * mm});
            skArc(sketch, "E538", {"start": v(-19.22, -17.75) * mm, "mid": v(-19.22, -17.77) * mm, "end": v(-19.21, -17.79) * mm});
            skArc(sketch, "E539", {"start": v(-19.21, -17.79) * mm, "mid": v(-19.18, -17.84) * mm, "end": v(-19.14, -17.89) * mm});
            skArc(sketch, "E540", {"start": v(-19.14, -17.89) * mm, "mid": v(-19.1, -17.95) * mm, "end": v(-19.05, -18) * mm});
            skArc(sketch, "E541", {"start": v(-19.05, -18) * mm, "mid": v(-19, -18.07) * mm, "end": v(-18.94, -18.14) * mm});
            skArc(sketch, "E542", {"start": v(-18.94, -18.14) * mm, "mid": v(-18.73, -18.42) * mm, "end": v(-18.56, -18.73) * mm});
            skArc(sketch, "E543", {"start": v(-18.56, -18.73) * mm, "mid": v(-18.47, -19) * mm, "end": v(-18.46, -19.28) * mm});
            skArc(sketch, "E544", {"start": v(-18.46, -19.28) * mm, "mid": v(-18.51, -19.57) * mm, "end": v(-18.64, -19.84) * mm});
            skArc(sketch, "E545", {"start": v(-18.64, -19.84) * mm, "mid": v(-18.86, -20.17) * mm, "end": v(-19.1, -20.47) * mm});
            skArc(sketch, "E546", {"start": v(-19.1, -20.47) * mm, "mid": v(-19.27, -20.63) * mm, "end": v(-19.45, -20.78) * mm});
            skArc(sketch, "E547", {"start": v(-19.45, -20.78) * mm, "mid": v(-19.6, -20.9) * mm, "end": v(-19.77, -20.99) * mm});
            skArc(sketch, "E548", {"start": v(-19.77, -20.99) * mm, "mid": v(-19.94, -21.06) * mm, "end": v(-20.12, -21.11) * mm});
            skArc(sketch, "E549", {"start": v(-20.12, -21.11) * mm, "mid": v(-20.36, -21.16) * mm, "end": v(-20.59, -21.19) * mm});
            skArc(sketch, "E550", {"start": v(-20.59, -21.19) * mm, "mid": v(-20.72, -21.2) * mm, "end": v(-20.84, -21.22) * mm});
            skArc(sketch, "E551", {"start": v(-20.84, -21.22) * mm, "mid": v(-20.98, -21.25) * mm, "end": v(-21.13, -21.28) * mm});
            skArc(sketch, "E552", {"start": v(-21.13, -21.28) * mm, "mid": v(-21.27, -21.31) * mm, "end": v(-21.41, -21.35) * mm});
            skArc(sketch, "E553", {"start": v(-21.41, -21.35) * mm, "mid": v(-21.53, -21.38) * mm, "end": v(-21.64, -21.42) * mm});
            skArc(sketch, "E554", {"start": v(-21.64, -21.42) * mm, "mid": v(-22, -21.53) * mm, "end": v(-22.39, -21.6) * mm});
            skArc(sketch, "E555", {"start": v(-22.39, -21.6) * mm, "mid": v(-22.73, -21.64) * mm, "end": v(-23.07, -21.63) * mm});
            skArc(sketch, "E556", {"start": v(-23.07, -21.63) * mm, "mid": v(-23.44, -21.58) * mm, "end": v(-23.8, -21.49) * mm});
            skArc(sketch, "E557", {"start": v(-23.8, -21.49) * mm, "mid": v(-24.25, -21.33) * mm, "end": v(-24.7, -21.16) * mm});
            skArc(sketch, "E558", {"start": v(-24.7, -21.16) * mm, "mid": v(-24.86, -21.09) * mm, "end": v(-25.02, -21.03) * mm});
            skArc(sketch, "E559", {"start": v(-25.02, -21.03) * mm, "mid": v(-25.2, -20.97) * mm, "end": v(-25.37, -20.9) * mm});
            skArc(sketch, "E560", {"start": v(-25.37, -20.9) * mm, "mid": v(-25.53, -20.86) * mm, "end": v(-25.7, -20.8) * mm});
            skArc(sketch, "E561", {"start": v(-25.7, -20.8) * mm, "mid": v(-25.8, -20.78) * mm, "end": v(-25.92, -20.76) * mm});
            skArc(sketch, "E562", {"start": v(-25.92, -20.76) * mm, "mid": v(-26.03, -20.74) * mm, "end": v(-26.13, -20.71) * mm});
            skArc(sketch, "E563", {"start": v(-26.13, -20.71) * mm, "mid": v(-26.24, -20.68) * mm, "end": v(-26.34, -20.65) * mm});
            skArc(sketch, "E564", {"start": v(-26.34, -20.65) * mm, "mid": v(-26.44, -20.62) * mm, "end": v(-26.54, -20.58) * mm});
            skArc(sketch, "E565", {"start": v(-26.54, -20.58) * mm, "mid": v(-26.61, -20.55) * mm, "end": v(-26.68, -20.51) * mm});
            skArc(sketch, "E566", {"start": v(-26.68, -20.51) * mm, "mid": v(-26.84, -20.42) * mm, "end": v(-26.98, -20.3) * mm});
            skArc(sketch, "E567", {"start": v(-26.98, -20.3) * mm, "mid": v(-27.13, -20.17) * mm, "end": v(-27.26, -20.02) * mm});
            skArc(sketch, "E568", {"start": v(-27.26, -20.02) * mm, "mid": v(-27.39, -19.87) * mm, "end": v(-27.5, -19.7) * mm});
            skArc(sketch, "E569", {"start": v(-27.5, -19.7) * mm, "mid": v(-27.59, -19.56) * mm, "end": v(-27.66, -19.4) * mm});
            skArc(sketch, "E570", {"start": v(-27.66, -19.4) * mm, "mid": v(-27.7, -19.3) * mm, "end": v(-27.73, -19.2) * mm});
            skArc(sketch, "E571", {"start": v(-27.73, -19.2) * mm, "mid": v(-27.74, -19.13) * mm, "end": v(-27.75, -19.06) * mm});
            skArc(sketch, "E572", {"start": v(-27.75, -19.06) * mm, "mid": v(-27.74, -19) * mm, "end": v(-27.73, -18.92) * mm});
            skArc(sketch, "E573", {"start": v(-27.73, -18.92) * mm, "mid": v(-27.68, -18.78) * mm, "end": v(-27.64, -18.64) * mm});
            skArc(sketch, "E574", {"start": v(-27.64, -18.64) * mm, "mid": v(-27.6, -18.54) * mm, "end": v(-27.57, -18.44) * mm});
            skArc(sketch, "E575", {"start": v(-27.57, -18.44) * mm, "mid": v(-27.52, -18.32) * mm, "end": v(-27.46, -18.2) * mm});
            skArc(sketch, "E576", {"start": v(-27.46, -18.2) * mm, "mid": v(-27.41, -18.08) * mm, "end": v(-27.36, -17.97) * mm});
            skArc(sketch, "E577", {"start": v(-27.36, -17.97) * mm, "mid": v(-27.3, -17.87) * mm, "end": v(-27.25, -17.78) * mm});
            skArc(sketch, "E578", {"start": v(-27.25, -17.78) * mm, "mid": v(-27.14, -17.58) * mm, "end": v(-27.03, -17.37) * mm});
            skArc(sketch, "E579", {"start": v(-27.03, -17.37) * mm, "mid": v(-26.99, -17.28) * mm, "end": v(-26.97, -17.17) * mm});
            skArc(sketch, "E580", {"start": v(-26.97, -17.17) * mm, "mid": v(-26.97, -17.1) * mm, "end": v(-27, -17.02) * mm});
            skArc(sketch, "E581", {"start": v(-27, -17.02) * mm, "mid": v(-27.06, -16.92) * mm, "end": v(-27.13, -16.82) * mm});
            skArc(sketch, "E582", {"start": v(-27.13, -16.82) * mm, "mid": v(-27.22, -16.7) * mm, "end": v(-27.31, -16.58) * mm});
            skArc(sketch, "E583", {"start": v(-27.31, -16.58) * mm, "mid": v(-27.37, -16.47) * mm, "end": v(-27.42, -16.35) * mm});
            skArc(sketch, "E584", {"start": v(-27.42, -16.35) * mm, "mid": v(-27.45, -16.22) * mm, "end": v(-27.47, -16.08) * mm});
            skArc(sketch, "E585", {"start": v(-27.47, -16.08) * mm, "mid": v(-27.48, -15.88) * mm, "end": v(-27.48, -15.68) * mm});
            skArc(sketch, "E586", {"start": v(-27.48, -15.68) * mm, "mid": v(-27.47, -15.38) * mm, "end": v(-27.43, -15.07) * mm});
            skArc(sketch, "E587", {"start": v(-27.43, -15.07) * mm, "mid": v(-27.36, -14.8) * mm, "end": v(-27.25, -14.55) * mm});
            skArc(sketch, "E588", {"start": v(-27.25, -14.55) * mm, "mid": v(-27.14, -14.35) * mm, "end": v(-26.99, -14.17) * mm});
            skArc(sketch, "E589", {"start": v(-26.99, -14.17) * mm, "mid": v(-26.83, -14.05) * mm, "end": v(-26.65, -13.97) * mm});
            skArc(sketch, "E590", {"start": v(-26.65, -13.97) * mm, "mid": v(-26.59, -13.95) * mm, "end": v(-26.52, -13.92) * mm});
            skArc(sketch, "E591", {"start": v(-26.52, -13.92) * mm, "mid": v(-26.43, -13.87) * mm, "end": v(-26.34, -13.81) * mm});
            skArc(sketch, "E592", {"start": v(-26.34, -13.81) * mm, "mid": v(-26.24, -13.74) * mm, "end": v(-26.14, -13.67) * mm});
            skArc(sketch, "E593", {"start": v(-26.14, -13.67) * mm, "mid": v(-26.04, -13.6) * mm, "end": v(-25.95, -13.52) * mm});
            skArc(sketch, "E594", {"start": v(-25.95, -13.52) * mm, "mid": v(-25.86, -13.44) * mm, "end": v(-25.76, -13.36) * mm});
            skArc(sketch, "E595", {"start": v(-25.76, -13.36) * mm, "mid": v(-25.66, -13.29) * mm, "end": v(-25.55, -13.21) * mm});
            skArc(sketch, "E596", {"start": v(-25.55, -13.21) * mm, "mid": v(-25.46, -13.14) * mm, "end": v(-25.36, -13.08) * mm});
            skArc(sketch, "E597", {"start": v(-25.36, -13.08) * mm, "mid": v(-25.3, -13.04) * mm, "end": v(-25.22, -13) * mm});
            skArc(sketch, "E598", {"start": v(-25.22, -13) * mm, "mid": v(-25.06, -12.93) * mm, "end": v(-24.9, -12.9) * mm});
            skArc(sketch, "E599", {"start": v(-24.9, -12.9) * mm, "mid": v(-24.69, -12.86) * mm, "end": v(-24.48, -12.85) * mm});
            skArc(sketch, "E600", {"start": v(-24.48, -12.85) * mm, "mid": v(-24.27, -12.86) * mm, "end": v(-24.07, -12.88) * mm});
            skArc(sketch, "E601", {"start": v(-24.07, -12.88) * mm, "mid": v(-23.9, -12.92) * mm, "end": v(-23.74, -12.98) * mm});
            skArc(sketch, "E602", {"start": v(-33.89, -13.23) * mm, "mid": v(-33.43, -13.32) * mm, "end": v(-32.97, -13.43) * mm});
            skArc(sketch, "E603", {"start": v(-32.97, -13.43) * mm, "mid": v(-32.68, -13.53) * mm, "end": v(-32.4, -13.66) * mm});
            skArc(sketch, "E604", {"start": v(-32.4, -13.66) * mm, "mid": v(-32.2, -13.8) * mm, "end": v(-32.02, -13.97) * mm});
            skArc(sketch, "E605", {"start": v(-32.02, -13.97) * mm, "mid": v(-31.85, -14.19) * mm, "end": v(-31.72, -14.43) * mm});
            skArc(sketch, "E606", {"start": v(-31.72, -14.43) * mm, "mid": v(-31.66, -14.54) * mm, "end": v(-31.61, -14.66) * mm});
            skArc(sketch, "E607", {"start": v(-31.61, -14.66) * mm, "mid": v(-31.59, -14.74) * mm, "end": v(-31.57, -14.82) * mm});
            skArc(sketch, "E608", {"start": v(-31.57, -14.82) * mm, "mid": v(-31.56, -14.9) * mm, "end": v(-31.56, -14.99) * mm});
            skArc(sketch, "E609", {"start": v(-31.56, -14.99) * mm, "mid": v(-31.56, -15.1) * mm, "end": v(-31.57, -15.23) * mm});
            skArc(sketch, "E610", {"start": v(-31.57, -15.23) * mm, "mid": v(-31.59, -15.4) * mm, "end": v(-31.58, -15.55) * mm});
            skArc(sketch, "E611", {"start": v(-31.58, -15.55) * mm, "mid": v(-31.56, -15.68) * mm, "end": v(-31.53, -15.8) * mm});
            skArc(sketch, "E612", {"start": v(-31.53, -15.8) * mm, "mid": v(-31.45, -15.97) * mm, "end": v(-31.37, -16.13) * mm});
            skArc(sketch, "E613", {"start": v(-31.37, -16.13) * mm, "mid": v(-31.17, -16.46) * mm, "end": v(-30.96, -16.8) * mm});
            skArc(sketch, "E614", {"start": v(-30.96, -16.8) * mm, "mid": v(-30.74, -17.18) * mm, "end": v(-30.53, -17.57) * mm});
            skArc(sketch, "E615", {"start": v(-30.53, -17.57) * mm, "mid": v(-30.35, -17.99) * mm, "end": v(-30.2, -18.41) * mm});
            skArc(sketch, "E616", {"start": v(-30.2, -18.41) * mm, "mid": v(-30.07, -18.8) * mm, "end": v(-29.98, -19.18) * mm});
            skArc(sketch, "E617", {"start": v(-29.98, -19.18) * mm, "mid": v(-29.95, -19.43) * mm, "end": v(-29.97, -19.68) * mm});
            skArc(sketch, "E618", {"start": v(-29.97, -19.68) * mm, "mid": v(-30, -19.82) * mm, "end": v(-30.06, -19.94) * mm});
            skArc(sketch, "E619", {"start": v(-30.06, -19.94) * mm, "mid": v(-30.15, -20.07) * mm, "end": v(-30.26, -20.2) * mm});
            skArc(sketch, "E620", {"start": v(-30.26, -20.2) * mm, "mid": v(-30.4, -20.32) * mm, "end": v(-30.54, -20.43) * mm});
            skArc(sketch, "E621", {"start": v(-30.54, -20.43) * mm, "mid": v(-30.72, -20.54) * mm, "end": v(-30.9, -20.64) * mm});
            skArc(sketch, "E622", {"start": v(-30.9, -20.64) * mm, "mid": v(-31.05, -20.7) * mm, "end": v(-31.2, -20.77) * mm});
            skArc(sketch, "E623", {"start": v(-31.2, -20.77) * mm, "mid": v(-31.31, -20.8) * mm, "end": v(-31.42, -20.83) * mm});
            skArc(sketch, "E624", {"start": v(-31.42, -20.83) * mm, "mid": v(-31.56, -20.85) * mm, "end": v(-31.7, -20.86) * mm});
            skArc(sketch, "E625", {"start": v(-31.7, -20.86) * mm, "mid": v(-31.96, -20.87) * mm, "end": v(-32.23, -20.88) * mm});
            skArc(sketch, "E626", {"start": v(-32.23, -20.88) * mm, "mid": v(-32.48, -20.88) * mm, "end": v(-32.73, -20.89) * mm});
            skArc(sketch, "E627", {"start": v(-32.73, -20.89) * mm, "mid": v(-32.87, -20.9) * mm, "end": v(-33.02, -20.91) * mm});
            skArc(sketch, "E628", {"start": v(-33.02, -20.91) * mm, "mid": v(-33.13, -20.94) * mm, "end": v(-33.24, -20.97) * mm});
            skArc(sketch, "E629", {"start": v(-33.24, -20.97) * mm, "mid": v(-33.37, -21.02) * mm, "end": v(-33.5, -21.07) * mm});
            skArc(sketch, "E630", {"start": v(-33.5, -21.07) * mm, "mid": v(-33.6, -21.1) * mm, "end": v(-33.68, -21.14) * mm});
            skArc(sketch, "E631", {"start": v(-33.68, -21.14) * mm, "mid": v(-33.8, -21.18) * mm, "end": v(-33.9, -21.22) * mm});
            skArc(sketch, "E632", {"start": v(-33.9, -21.22) * mm, "mid": v(-34, -21.25) * mm, "end": v(-34.1, -21.28) * mm});
            skArc(sketch, "E633", {"start": v(-34.1, -21.28) * mm, "mid": v(-34.2, -21.3) * mm, "end": v(-34.28, -21.32) * mm});
            skArc(sketch, "E634", {"start": v(-34.28, -21.32) * mm, "mid": v(-34.5, -21.36) * mm, "end": v(-34.73, -21.38) * mm});
            skArc(sketch, "E635", {"start": v(-34.73, -21.38) * mm, "mid": v(-34.98, -21.39) * mm, "end": v(-35.24, -21.39) * mm});
            skArc(sketch, "E636", {"start": v(-35.24, -21.39) * mm, "mid": v(-35.48, -21.38) * mm, "end": v(-35.71, -21.36) * mm});
            skArc(sketch, "E637", {"start": v(-35.71, -21.36) * mm, "mid": v(-35.86, -21.33) * mm, "end": v(-36, -21.28) * mm});
            skArc(sketch, "E638", {"start": v(-36, -21.28) * mm, "mid": v(-36.08, -21.26) * mm, "end": v(-36.16, -21.24) * mm});
            skArc(sketch, "E639", {"start": v(-36.16, -21.24) * mm, "mid": v(-36.32, -21.2) * mm, "end": v(-36.48, -21.18) * mm});
            skArc(sketch, "E640", {"start": v(-36.48, -21.18) * mm, "mid": v(-36.66, -21.15) * mm, "end": v(-36.85, -21.13) * mm});
            skArc(sketch, "E641", {"start": v(-36.85, -21.13) * mm, "mid": v(-37.05, -21.1) * mm, "end": v(-37.25, -21.08) * mm});
            skArc(sketch, "E642", {"start": v(-37.25, -21.08) * mm, "mid": v(-37.45, -21.06) * mm, "end": v(-37.64, -21.04) * mm});
            skArc(sketch, "E643", {"start": v(-37.64, -21.04) * mm, "mid": v(-37.83, -21.01) * mm, "end": v(-38.02, -20.98) * mm});
            skArc(sketch, "E644", {"start": v(-38.02, -20.98) * mm, "mid": v(-38.17, -20.96) * mm, "end": v(-38.33, -20.93) * mm});
            skArc(sketch, "E645", {"start": v(-38.33, -20.93) * mm, "mid": v(-38.41, -20.9) * mm, "end": v(-38.49, -20.88) * mm});
            skArc(sketch, "E646", {"start": v(-38.49, -20.88) * mm, "mid": v(-38.62, -20.81) * mm, "end": v(-38.74, -20.73) * mm});
            skArc(sketch, "E647", {"start": v(-38.74, -20.73) * mm, "mid": v(-38.88, -20.61) * mm, "end": v(-39.01, -20.49) * mm});
            skArc(sketch, "E648", {"start": v(-39.01, -20.49) * mm, "mid": v(-39.15, -20.34) * mm, "end": v(-39.27, -20.18) * mm});
            skArc(sketch, "E649", {"start": v(-39.27, -20.18) * mm, "mid": v(-39.38, -20.02) * mm, "end": v(-39.48, -19.85) * mm});
            skLineSegment(sketch, "E650", {"start": v(-39.48, -19.85) * mm, "end": v(-39.68, -19.49) * mm});
            skLineSegment(sketch, "E651", {"start": v(-39.68, -19.49) * mm, "end": v(-39.56, -19.16) * mm});
            skArc(sketch, "E652", {"start": v(-39.56, -19.16) * mm, "mid": v(-39.52, -19.07) * mm, "end": v(-39.47, -18.97) * mm});
            skArc(sketch, "E653", {"start": v(-39.47, -18.97) * mm, "mid": v(-39.39, -18.78) * mm, "end": v(-39.3, -18.58) * mm});
            skArc(sketch, "E654", {"start": v(-39.3, -18.58) * mm, "mid": v(-39.19, -18.35) * mm, "end": v(-39.08, -18.13) * mm});
            skArc(sketch, "E655", {"start": v(-39.08, -18.13) * mm, "mid": v(-38.96, -17.89) * mm, "end": v(-38.85, -17.65) * mm});
            skArc(sketch, "E656", {"start": v(-38.85, -17.65) * mm, "mid": v(-38.73, -17.4) * mm, "end": v(-38.61, -17.16) * mm});
            skArc(sketch, "E657", {"start": v(-38.61, -17.16) * mm, "mid": v(-38.5, -16.92) * mm, "end": v(-38.4, -16.67) * mm});
            skArc(sketch, "E658", {"start": v(-38.4, -16.67) * mm, "mid": v(-38.3, -16.46) * mm, "end": v(-38.21, -16.25) * mm});
            skArc(sketch, "E659", {"start": v(-38.21, -16.25) * mm, "mid": v(-38.16, -16.13) * mm, "end": v(-38.12, -16) * mm});
            skArc(sketch, "E660", {"start": v(-38.12, -16) * mm, "mid": v(-38.08, -15.87) * mm, "end": v(-38.04, -15.73) * mm});
            skArc(sketch, "E661", {"start": v(-38.04, -15.73) * mm, "mid": v(-38.03, -15.65) * mm, "end": v(-38.02, -15.57) * mm});
            skArc(sketch, "E662", {"start": v(-38.02, -15.57) * mm, "mid": v(-38.02, -15.5) * mm, "end": v(-38.03, -15.43) * mm});
            skArc(sketch, "E663", {"start": v(-38.03, -15.43) * mm, "mid": v(-38.06, -15.32) * mm, "end": v(-38.1, -15.21) * mm});
            skArc(sketch, "E664", {"start": v(-38.1, -15.21) * mm, "mid": v(-38.16, -14.91) * mm, "end": v(-38.16, -14.6) * mm});
            skArc(sketch, "E665", {"start": v(-38.16, -14.6) * mm, "mid": v(-38.09, -14.28) * mm, "end": v(-37.97, -13.97) * mm});
            skArc(sketch, "E666", {"start": v(-37.97, -13.97) * mm, "mid": v(-37.8, -13.68) * mm, "end": v(-37.58, -13.43) * mm});
            skArc(sketch, "E667", {"start": v(-37.58, -13.43) * mm, "mid": v(-37.35, -13.25) * mm, "end": v(-37.08, -13.12) * mm});
            skArc(sketch, "E668", {"start": v(-37.08, -13.12) * mm, "mid": v(-36.9, -13.08) * mm, "end": v(-36.73, -13.07) * mm});
            skArc(sketch, "E669", {"start": v(-36.73, -13.07) * mm, "mid": v(-36.19, -13.08) * mm, "end": v(-35.65, -13.1) * mm});
            skArc(sketch, "E670", {"start": v(-35.65, -13.1) * mm, "mid": v(-35.1, -13.12) * mm, "end": v(-34.57, -13.15) * mm});
            skArc(sketch, "E671", {"start": v(-34.57, -13.15) * mm, "mid": v(-34.23, -13.18) * mm, "end": v(-33.89, -13.23) * mm});
            skArc(sketch, "E672", {"start": v(11.01, -13.24) * mm, "mid": v(11.17, -13.35) * mm, "end": v(11.3, -13.49) * mm});
            skArc(sketch, "E673", {"start": v(11.3, -13.49) * mm, "mid": v(11.4, -13.65) * mm, "end": v(11.48, -13.82) * mm});
            skArc(sketch, "E674", {"start": v(11.48, -13.82) * mm, "mid": v(11.54, -14.09) * mm, "end": v(11.58, -14.35) * mm});
            skArc(sketch, "E675", {"start": v(11.58, -14.35) * mm, "mid": v(11.62, -14.81) * mm, "end": v(11.65, -15.28) * mm});
            skArc(sketch, "E676", {"start": v(11.65, -15.28) * mm, "mid": v(11.67, -15.73) * mm, "end": v(11.7, -16.2) * mm});
            skArc(sketch, "E677", {"start": v(11.7, -16.2) * mm, "mid": v(11.72, -16.42) * mm, "end": v(11.74, -16.66) * mm});
            skArc(sketch, "E678", {"start": v(11.74, -16.66) * mm, "mid": v(11.77, -16.79) * mm, "end": v(11.8, -16.92) * mm});
            skArc(sketch, "E679", {"start": v(11.8, -16.92) * mm, "mid": v(11.82, -16.96) * mm, "end": v(11.87, -16.98) * mm});
            skArc(sketch, "E680", {"start": v(11.87, -16.98) * mm, "mid": v(11.92, -16.97) * mm, "end": v(11.97, -16.95) * mm});
            skArc(sketch, "E681", {"start": v(11.97, -16.95) * mm, "mid": v(12.08, -16.87) * mm, "end": v(12.2, -16.8) * mm});
            skArc(sketch, "E682", {"start": v(12.2, -16.8) * mm, "mid": v(12.36, -16.67) * mm, "end": v(12.52, -16.54) * mm});
            skArc(sketch, "E683", {"start": v(12.52, -16.54) * mm, "mid": v(12.78, -16.33) * mm, "end": v(13.04, -16.12) * mm});
            skArc(sketch, "E684", {"start": v(13.04, -16.12) * mm, "mid": v(13.41, -15.82) * mm, "end": v(13.8, -15.54) * mm});
            skArc(sketch, "E685", {"start": v(13.8, -15.54) * mm, "mid": v(14.1, -15.38) * mm, "end": v(14.4, -15.25) * mm});
            skArc(sketch, "E686", {"start": v(14.4, -15.25) * mm, "mid": v(14.66, -15.2) * mm, "end": v(14.93, -15.19) * mm});
            skArc(sketch, "E687", {"start": v(14.93, -15.19) * mm, "mid": v(15.2, -15.23) * mm, "end": v(15.46, -15.33) * mm});
            skArc(sketch, "E688", {"start": v(15.46, -15.33) * mm, "mid": v(15.7, -15.45) * mm, "end": v(15.94, -15.6) * mm});
            skArc(sketch, "E689", {"start": v(15.94, -15.6) * mm, "mid": v(16.12, -15.76) * mm, "end": v(16.28, -15.94) * mm});
            skArc(sketch, "E690", {"start": v(16.28, -15.94) * mm, "mid": v(16.4, -16.12) * mm, "end": v(16.48, -16.33) * mm});
            skArc(sketch, "E691", {"start": v(16.48, -16.33) * mm, "mid": v(16.53, -16.55) * mm, "end": v(16.55, -16.77) * mm});
            skArc(sketch, "E692", {"start": v(16.55, -16.77) * mm, "mid": v(16.54, -16.93) * mm, "end": v(16.5, -17.1) * mm});
            skArc(sketch, "E693", {"start": v(16.5, -17.1) * mm, "mid": v(16.46, -17.25) * mm, "end": v(16.4, -17.4) * mm});
            skArc(sketch, "E694", {"start": v(16.4, -17.4) * mm, "mid": v(16.3, -17.59) * mm, "end": v(16.2, -17.75) * mm});
            skArc(sketch, "E695", {"start": v(16.2, -17.75) * mm, "mid": v(16.03, -17.98) * mm, "end": v(15.86, -18.2) * mm});
            skArc(sketch, "E696", {"start": v(15.86, -18.2) * mm, "mid": v(15.37, -18.74) * mm, "end": v(14.83, -19.24) * mm});
            skArc(sketch, "E697", {"start": v(14.83, -19.24) * mm, "mid": v(14.19, -19.72) * mm, "end": v(13.52, -20.16) * mm});
            skArc(sketch, "E698", {"start": v(13.52, -20.16) * mm, "mid": v(12.81, -20.55) * mm, "end": v(12.08, -20.88) * mm});
            skArc(sketch, "E699", {"start": v(12.08, -20.88) * mm, "mid": v(11.39, -21.12) * mm, "end": v(10.68, -21.3) * mm});
            skArc(sketch, "E700", {"start": v(10.68, -21.3) * mm, "mid": v(10.34, -21.35) * mm, "end": v(10, -21.39) * mm});
            skArc(sketch, "E701", {"start": v(10, -21.39) * mm, "mid": v(9.75, -21.4) * mm, "end": v(9.5, -21.36) * mm});
            skArc(sketch, "E702", {"start": v(9.5, -21.36) * mm, "mid": v(9.3, -21.3) * mm, "end": v(9.12, -21.21) * mm});
            skArc(sketch, "E703", {"start": v(9.12, -21.21) * mm, "mid": v(8.93, -21.08) * mm, "end": v(8.76, -20.93) * mm});
            skArc(sketch, "E704", {"start": v(8.76, -20.93) * mm, "mid": v(8.6, -20.73) * mm, "end": v(8.46, -20.52) * mm});
            skArc(sketch, "E705", {"start": v(8.46, -20.52) * mm, "mid": v(8.37, -20.32) * mm, "end": v(8.31, -20.1) * mm});
            skArc(sketch, "E706", {"start": v(8.31, -20.1) * mm, "mid": v(8.27, -19.77) * mm, "end": v(8.25, -19.44) * mm});
            skArc(sketch, "E707", {"start": v(8.25, -19.44) * mm, "mid": v(8.24, -18.5) * mm, "end": v(8.23, -17.58) * mm});
            skArc(sketch, "E708", {"start": v(8.23, -17.58) * mm, "mid": v(8.23, -16.18) * mm, "end": v(8.25, -14.77) * mm});
            skArc(sketch, "E709", {"start": v(8.25, -14.77) * mm, "mid": v(8.3, -14.23) * mm, "end": v(8.46, -13.7) * mm});
            skArc(sketch, "E710", {"start": v(8.46, -13.7) * mm, "mid": v(8.66, -13.4) * mm, "end": v(8.98, -13.22) * mm});
            skArc(sketch, "E711", {"start": v(8.98, -13.22) * mm, "mid": v(9.48, -13.1) * mm, "end": v(10, -13.08) * mm});
            skArc(sketch, "E712", {"start": v(10, -13.08) * mm, "mid": v(10.2, -13.08) * mm, "end": v(10.4, -13.1) * mm});
            skArc(sketch, "E713", {"start": v(10.4, -13.1) * mm, "mid": v(10.54, -13.1) * mm, "end": v(10.67, -13.12) * mm});
            skArc(sketch, "E714", {"start": v(10.67, -13.12) * mm, "mid": v(10.76, -13.14) * mm, "end": v(10.85, -13.17) * mm});
            skArc(sketch, "E715", {"start": v(10.85, -13.17) * mm, "mid": v(10.93, -13.2) * mm, "end": v(11.01, -13.24) * mm});
            skArc(sketch, "E716", {"start": v(21.68, -13.2) * mm, "mid": v(22.1, -13.36) * mm, "end": v(22.52, -13.53) * mm});
            skArc(sketch, "E717", {"start": v(22.52, -13.53) * mm, "mid": v(22.99, -13.76) * mm, "end": v(23.45, -14) * mm});
            skArc(sketch, "E718", {"start": v(23.45, -14) * mm, "mid": v(23.88, -14.25) * mm, "end": v(24.3, -14.5) * mm});
            skArc(sketch, "E719", {"start": v(24.3, -14.5) * mm, "mid": v(24.54, -14.67) * mm, "end": v(24.77, -14.88) * mm});
            skArc(sketch, "E720", {"start": v(24.77, -14.88) * mm, "mid": v(24.87, -14.98) * mm, "end": v(24.98, -15.07) * mm});
            skArc(sketch, "E721", {"start": v(24.98, -15.07) * mm, "mid": v(25.07, -15.12) * mm, "end": v(25.17, -15.14) * mm});
            skArc(sketch, "E722", {"start": v(25.17, -15.14) * mm, "mid": v(25.28, -15.15) * mm, "end": v(25.4, -15.14) * mm});
            skArc(sketch, "E723", {"start": v(25.4, -15.14) * mm, "mid": v(25.6, -15.1) * mm, "end": v(25.8, -15.05) * mm});
            skArc(sketch, "E724", {"start": v(25.8, -15.05) * mm, "mid": v(25.96, -15.02) * mm, "end": v(26.13, -15) * mm});
            skArc(sketch, "E725", {"start": v(26.13, -15) * mm, "mid": v(26.3, -15) * mm, "end": v(26.46, -15) * mm});
            skArc(sketch, "E726", {"start": v(26.46, -15) * mm, "mid": v(26.62, -15.02) * mm, "end": v(26.78, -15.06) * mm});
            skArc(sketch, "E727", {"start": v(26.78, -15.06) * mm, "mid": v(26.93, -15.1) * mm, "end": v(27.07, -15.17) * mm});
            skArc(sketch, "E728", {"start": v(27.07, -15.17) * mm, "mid": v(27.2, -15.25) * mm, "end": v(27.33, -15.34) * mm});
            skArc(sketch, "E729", {"start": v(27.33, -15.34) * mm, "mid": v(27.47, -15.45) * mm, "end": v(27.6, -15.57) * mm});
            skArc(sketch, "E730", {"start": v(27.6, -15.57) * mm, "mid": v(27.71, -15.7) * mm, "end": v(27.82, -15.83) * mm});
            skArc(sketch, "E731", {"start": v(27.82, -15.83) * mm, "mid": v(27.9, -15.95) * mm, "end": v(27.98, -16.08) * mm});
            skArc(sketch, "E732", {"start": v(27.98, -16.08) * mm, "mid": v(28.1, -16.37) * mm, "end": v(28.15, -16.67) * mm});
            skArc(sketch, "E733", {"start": v(28.15, -16.67) * mm, "mid": v(28.14, -16.97) * mm, "end": v(28.08, -17.25) * mm});
            skArc(sketch, "E734", {"start": v(28.08, -17.25) * mm, "mid": v(27.93, -17.58) * mm, "end": v(27.73, -17.89) * mm});
            skArc(sketch, "E735", {"start": v(27.73, -17.89) * mm, "mid": v(27.41, -18.28) * mm, "end": v(27.07, -18.66) * mm});
            skArc(sketch, "E736", {"start": v(27.07, -18.66) * mm, "mid": v(26.6, -19.12) * mm, "end": v(26.1, -19.55) * mm});
            skArc(sketch, "E737", {"start": v(26.1, -19.55) * mm, "mid": v(25.62, -19.91) * mm, "end": v(25.1, -20.24) * mm});
            skArc(sketch, "E738", {"start": v(25.1, -20.24) * mm, "mid": v(24.57, -20.52) * mm, "end": v(24.01, -20.76) * mm});
            skArc(sketch, "E739", {"start": v(24.01, -20.76) * mm, "mid": v(23.4, -20.97) * mm, "end": v(22.77, -21.14) * mm});
            skArc(sketch, "E740", {"start": v(22.77, -21.14) * mm, "mid": v(22.32, -21.24) * mm, "end": v(21.87, -21.32) * mm});
            skArc(sketch, "E741", {"start": v(21.87, -21.32) * mm, "mid": v(21.48, -21.36) * mm, "end": v(21.1, -21.38) * mm});
            skArc(sketch, "E742", {"start": v(21.1, -21.38) * mm, "mid": v(20.77, -21.37) * mm, "end": v(20.46, -21.33) * mm});
            skArc(sketch, "E743", {"start": v(20.46, -21.33) * mm, "mid": v(20.24, -21.26) * mm, "end": v(20.03, -21.16) * mm});
            skArc(sketch, "E744", {"start": v(20.03, -21.16) * mm, "mid": v(19.9, -21.05) * mm, "end": v(19.8, -20.93) * mm});
            skArc(sketch, "E745", {"start": v(19.8, -20.93) * mm, "mid": v(19.7, -20.76) * mm, "end": v(19.63, -20.58) * mm});
            skArc(sketch, "E746", {"start": v(19.63, -20.58) * mm, "mid": v(19.56, -20.36) * mm, "end": v(19.5, -20.15) * mm});
            skArc(sketch, "E747", {"start": v(19.5, -20.15) * mm, "mid": v(19.48, -19.91) * mm, "end": v(19.46, -19.68) * mm});
            skArc(sketch, "E748", {"start": v(19.46, -19.68) * mm, "mid": v(19.47, -19.48) * mm, "end": v(19.48, -19.28) * mm});
            skArc(sketch, "E749", {"start": v(19.48, -19.28) * mm, "mid": v(19.5, -19.12) * mm, "end": v(19.54, -18.96) * mm});
            skArc(sketch, "E750", {"start": v(19.54, -18.96) * mm, "mid": v(19.6, -18.83) * mm, "end": v(19.65, -18.7) * mm});
            skArc(sketch, "E751", {"start": v(19.65, -18.7) * mm, "mid": v(19.73, -18.6) * mm, "end": v(19.82, -18.5) * mm});
            skArc(sketch, "E752", {"start": v(19.82, -18.5) * mm, "mid": v(19.94, -18.4) * mm, "end": v(20.07, -18.32) * mm});
            skArc(sketch, "E753", {"start": v(20.07, -18.32) * mm, "mid": v(20.23, -18.24) * mm, "end": v(20.4, -18.17) * mm});
            skArc(sketch, "E754", {"start": v(20.4, -18.17) * mm, "mid": v(20.63, -18.1) * mm, "end": v(20.87, -18.03) * mm});
            skArc(sketch, "E755", {"start": v(20.87, -18.03) * mm, "mid": v(21.26, -17.94) * mm, "end": v(21.65, -17.86) * mm});
            skLineSegment(sketch, "E756", {"start": v(21.65, -17.86) * mm, "end": v(22.73, -17.64) * mm});
            skLineSegment(sketch, "E757", {"start": v(22.73, -17.64) * mm, "end": v(21.76, -17.13) * mm});
            skArc(sketch, "E758", {"start": v(21.76, -17.13) * mm, "mid": v(21.18, -16.81) * mm, "end": v(20.6, -16.48) * mm});
            skArc(sketch, "E759", {"start": v(20.6, -16.48) * mm, "mid": v(20.25, -16.24) * mm, "end": v(19.92, -15.97) * mm});
            skArc(sketch, "E760", {"start": v(19.92, -15.97) * mm, "mid": v(19.71, -15.75) * mm, "end": v(19.54, -15.5) * mm});
            skArc(sketch, "E761", {"start": v(19.54, -15.5) * mm, "mid": v(19.45, -15.25) * mm, "end": v(19.42, -14.99) * mm});
            skArc(sketch, "E762", {"start": v(19.42, -14.99) * mm, "mid": v(19.45, -14.7) * mm, "end": v(19.56, -14.43) * mm});
            skArc(sketch, "E763", {"start": v(19.56, -14.43) * mm, "mid": v(19.77, -14.09) * mm, "end": v(20.02, -13.77) * mm});
            skArc(sketch, "E764", {"start": v(20.02, -13.77) * mm, "mid": v(20.29, -13.48) * mm, "end": v(20.58, -13.23) * mm});
            skArc(sketch, "E765", {"start": v(20.58, -13.23) * mm, "mid": v(20.8, -13.1) * mm, "end": v(21.06, -13.06) * mm});
            skArc(sketch, "E766", {"start": v(21.06, -13.06) * mm, "mid": v(21.12, -13.06) * mm, "end": v(21.17, -13.07) * mm});
            skArc(sketch, "E767", {"start": v(21.17, -13.07) * mm, "mid": v(21.25, -13.08) * mm, "end": v(21.34, -13.1) * mm});
            skArc(sketch, "E768", {"start": v(21.34, -13.1) * mm, "mid": v(21.43, -13.12) * mm, "end": v(21.51, -13.15) * mm});
            skArc(sketch, "E769", {"start": v(21.51, -13.15) * mm, "mid": v(21.6, -13.17) * mm, "end": v(21.68, -13.2) * mm});
            skArc(sketch, "E770", {"start": v(2.9, -13.34) * mm, "mid": v(3.16, -13.38) * mm, "end": v(3.42, -13.43) * mm});
            skArc(sketch, "E771", {"start": v(3.42, -13.43) * mm, "mid": v(3.63, -13.48) * mm, "end": v(3.83, -13.55) * mm});
            skArc(sketch, "E772", {"start": v(3.83, -13.55) * mm, "mid": v(3.98, -13.63) * mm, "end": v(4.12, -13.72) * mm});
            skArc(sketch, "E773", {"start": v(4.12, -13.72) * mm, "mid": v(4.22, -13.82) * mm, "end": v(4.3, -13.94) * mm});
            skArc(sketch, "E774", {"start": v(4.3, -13.94) * mm, "mid": v(4.36, -14.1) * mm, "end": v(4.39, -14.3) * mm});
            skArc(sketch, "E775", {"start": v(4.39, -14.3) * mm, "mid": v(4.4, -14.67) * mm, "end": v(4.4, -15.04) * mm});
            skArc(sketch, "E776", {"start": v(4.4, -15.04) * mm, "mid": v(4.4, -15.44) * mm, "end": v(4.37, -15.83) * mm});
            skArc(sketch, "E777", {"start": v(4.37, -15.83) * mm, "mid": v(4.33, -16.15) * mm, "end": v(4.27, -16.46) * mm});
            skArc(sketch, "E778", {"start": v(4.27, -16.46) * mm, "mid": v(4.15, -16.9) * mm, "end": v(4, -17.35) * mm});
            skArc(sketch, "E779", {"start": v(4, -17.35) * mm, "mid": v(3.84, -17.76) * mm, "end": v(3.65, -18.16) * mm});
            skArc(sketch, "E780", {"start": v(3.65, -18.16) * mm, "mid": v(3.44, -18.53) * mm, "end": v(3.2, -18.89) * mm});
            skArc(sketch, "E781", {"start": v(3.2, -18.89) * mm, "mid": v(2.95, -19.23) * mm, "end": v(2.67, -19.55) * mm});
            skArc(sketch, "E782", {"start": v(2.67, -19.55) * mm, "mid": v(2.28, -19.92) * mm, "end": v(1.86, -20.26) * mm});
            skArc(sketch, "E783", {"start": v(1.86, -20.26) * mm, "mid": v(1.43, -20.54) * mm, "end": v(0.97, -20.79) * mm});
            skArc(sketch, "E784", {"start": v(0.97, -20.79) * mm, "mid": v(0.43, -21.01) * mm, "end": v(-0.13, -21.2) * mm});
            skArc(sketch, "E785", {"start": v(-0.13, -21.2) * mm, "mid": v(-0.84, -21.38) * mm, "end": v(-1.56, -21.53) * mm});
            skArc(sketch, "E786", {"start": v(-1.56, -21.53) * mm, "mid": v(-1.8, -21.57) * mm, "end": v(-2.02, -21.61) * mm});
            skArc(sketch, "E787", {"start": v(-2.02, -21.61) * mm, "mid": v(-2.14, -21.63) * mm, "end": v(-2.25, -21.64) * mm});
            skArc(sketch, "E788", {"start": v(-2.25, -21.64) * mm, "mid": v(-2.33, -21.64) * mm, "end": v(-2.4, -21.63) * mm});
            skArc(sketch, "E789", {"start": v(-2.4, -21.63) * mm, "mid": v(-2.48, -21.6) * mm, "end": v(-2.55, -21.58) * mm});
            skArc(sketch, "E790", {"start": v(-2.55, -21.58) * mm, "mid": v(-2.82, -21.4) * mm, "end": v(-3.05, -21.17) * mm});
            skArc(sketch, "E791", {"start": v(-3.05, -21.17) * mm, "mid": v(-3.26, -20.86) * mm, "end": v(-3.44, -20.53) * mm});
            skArc(sketch, "E792", {"start": v(-3.44, -20.53) * mm, "mid": v(-3.57, -20.17) * mm, "end": v(-3.65, -19.8) * mm});
            skArc(sketch, "E793", {"start": v(-3.65, -19.8) * mm, "mid": v(-3.67, -19.48) * mm, "end": v(-3.62, -19.16) * mm});
            skArc(sketch, "E794", {"start": v(-3.62, -19.16) * mm, "mid": v(-3.57, -19.03) * mm, "end": v(-3.51, -18.9) * mm});
            skArc(sketch, "E795", {"start": v(-3.51, -18.9) * mm, "mid": v(-3.43, -18.77) * mm, "end": v(-3.34, -18.65) * mm});
            skArc(sketch, "E796", {"start": v(-3.34, -18.65) * mm, "mid": v(-3.23, -18.53) * mm, "end": v(-3.11, -18.43) * mm});
            skArc(sketch, "E797", {"start": v(-3.11, -18.43) * mm, "mid": v(-3, -18.34) * mm, "end": v(-2.87, -18.27) * mm});
            skArc(sketch, "E798", {"start": v(-2.87, -18.27) * mm, "mid": v(-2.8, -18.24) * mm, "end": v(-2.73, -18.22) * mm});
            skArc(sketch, "E799", {"start": v(-2.73, -18.22) * mm, "mid": v(-2.6, -18.18) * mm, "end": v(-2.5, -18.14) * mm});
            skArc(sketch, "E800", {"start": v(-2.5, -18.14) * mm, "mid": v(-2.36, -18.1) * mm, "end": v(-2.22, -18.06) * mm});
            skArc(sketch, "E801", {"start": v(-2.22, -18.06) * mm, "mid": v(-2.09, -18.02) * mm, "end": v(-1.95, -17.99) * mm});
            skArc(sketch, "E802", {"start": v(-1.95, -17.99) * mm, "mid": v(-1.66, -17.9) * mm, "end": v(-1.37, -17.8) * mm});
            skArc(sketch, "E803", {"start": v(-1.37, -17.8) * mm, "mid": v(-0.93, -17.63) * mm, "end": v(-0.49, -17.44) * mm});
            skArc(sketch, "E804", {"start": v(-0.49, -17.44) * mm, "mid": v(-0.02, -17.23) * mm, "end": v(0.44, -17.02) * mm});
            skArc(sketch, "E805", {"start": v(0.44, -17.02) * mm, "mid": v(0.5, -16.98) * mm, "end": v(0.52, -16.91) * mm});
            skArc(sketch, "E806", {"start": v(0.52, -16.91) * mm, "mid": v(0.51, -16.9) * mm, "end": v(0.5, -16.9) * mm});
            skArc(sketch, "E807", {"start": v(0.5, -16.9) * mm, "mid": v(0.32, -16.87) * mm, "end": v(0.15, -16.86) * mm});
            skArc(sketch, "E808", {"start": v(0.15, -16.86) * mm, "mid": v(-0.05, -16.84) * mm, "end": v(-0.25, -16.82) * mm});
            skArc(sketch, "E809", {"start": v(-0.25, -16.82) * mm, "mid": v(-0.49, -16.8) * mm, "end": v(-0.73, -16.78) * mm});
            skArc(sketch, "E810", {"start": v(-0.73, -16.78) * mm, "mid": v(-1.55, -16.71) * mm, "end": v(-2.37, -16.62) * mm});
            skArc(sketch, "E811", {"start": v(-2.37, -16.62) * mm, "mid": v(-2.8, -16.52) * mm, "end": v(-3.2, -16.34) * mm});
            skArc(sketch, "E812", {"start": v(-3.2, -16.34) * mm, "mid": v(-3.46, -16.14) * mm, "end": v(-3.63, -15.86) * mm});
            skArc(sketch, "E813", {"start": v(-3.63, -15.86) * mm, "mid": v(-3.75, -15.46) * mm, "end": v(-3.81, -15.06) * mm});
            skArc(sketch, "E814", {"start": v(-3.81, -15.06) * mm, "mid": v(-3.81, -14.66) * mm, "end": v(-3.78, -14.26) * mm});
            skArc(sketch, "E815", {"start": v(-3.78, -14.26) * mm, "mid": v(-3.7, -14) * mm, "end": v(-3.55, -13.78) * mm});
            skArc(sketch, "E816", {"start": v(-3.55, -13.78) * mm, "mid": v(-3.33, -13.6) * mm, "end": v(-3.07, -13.5) * mm});
            skArc(sketch, "E817", {"start": v(-3.07, -13.5) * mm, "mid": v(-2.65, -13.4) * mm, "end": v(-2.21, -13.34) * mm});
            skArc(sketch, "E818", {"start": v(-2.21, -13.34) * mm, "mid": v(-1.79, -13.3) * mm, "end": v(-1.35, -13.3) * mm});
            skArc(sketch, "E819", {"start": v(-1.35, -13.3) * mm, "mid": v(-0.5, -13.29) * mm, "end": v(0.36, -13.28) * mm});
            skArc(sketch, "E820", {"start": v(0.36, -13.28) * mm, "mid": v(1.22, -13.29) * mm, "end": v(2.07, -13.3) * mm});
            skArc(sketch, "E821", {"start": v(2.07, -13.3) * mm, "mid": v(2.48, -13.3) * mm, "end": v(2.9, -13.34) * mm});
            skArc(sketch, "E822", {"start": v(-12.85, -13.72) * mm, "mid": v(-12.7, -13.81) * mm, "end": v(-12.55, -13.93) * mm});
            skArc(sketch, "E823", {"start": v(-12.55, -13.93) * mm, "mid": v(-12.44, -14.06) * mm, "end": v(-12.35, -14.2) * mm});
            skArc(sketch, "E824", {"start": v(-12.35, -14.2) * mm, "mid": v(-12.28, -14.4) * mm, "end": v(-12.23, -14.62) * mm});
            skArc(sketch, "E825", {"start": v(-12.23, -14.62) * mm, "mid": v(-12.18, -14.93) * mm, "end": v(-12.15, -15.24) * mm});
            skArc(sketch, "E826", {"start": v(-12.15, -15.24) * mm, "mid": v(-12.12, -15.52) * mm, "end": v(-12.1, -15.8) * mm});
            skArc(sketch, "E827", {"start": v(-12.1, -15.8) * mm, "mid": v(-12.07, -15.94) * mm, "end": v(-12.03, -16.08) * mm});
            skArc(sketch, "E828", {"start": v(-12.03, -16.08) * mm, "mid": v(-11.98, -16.16) * mm, "end": v(-11.92, -16.23) * mm});
            skArc(sketch, "E829", {"start": v(-11.92, -16.23) * mm, "mid": v(-11.85, -16.27) * mm, "end": v(-11.77, -16.28) * mm});
            skArc(sketch, "E830", {"start": v(-11.77, -16.28) * mm, "mid": v(-11.7, -16.27) * mm, "end": v(-11.64, -16.24) * mm});
            skArc(sketch, "E831", {"start": v(-11.64, -16.24) * mm, "mid": v(-11.6, -16.2) * mm, "end": v(-11.57, -16.13) * mm});
            skArc(sketch, "E832", {"start": v(-11.57, -16.13) * mm, "mid": v(-11.55, -16.02) * mm, "end": v(-11.55, -15.91) * mm});
            skArc(sketch, "E833", {"start": v(-11.55, -15.91) * mm, "mid": v(-11.56, -15.68) * mm, "end": v(-11.57, -15.45) * mm});
            skArc(sketch, "E834", {"start": v(-11.57, -15.45) * mm, "mid": v(-11.58, -15.22) * mm, "end": v(-11.58, -14.98) * mm});
            skArc(sketch, "E835", {"start": v(-11.58, -14.98) * mm, "mid": v(-11.56, -14.82) * mm, "end": v(-11.52, -14.68) * mm});
            skArc(sketch, "E836", {"start": v(-11.52, -14.68) * mm, "mid": v(-11.46, -14.54) * mm, "end": v(-11.37, -14.42) * mm});
            skArc(sketch, "E837", {"start": v(-11.37, -14.42) * mm, "mid": v(-11.22, -14.27) * mm, "end": v(-11.06, -14.12) * mm});
            skArc(sketch, "E838", {"start": v(-11.06, -14.12) * mm, "mid": v(-10.9, -14) * mm, "end": v(-10.74, -13.88) * mm});
            skArc(sketch, "E839", {"start": v(-10.74, -13.88) * mm, "mid": v(-10.56, -13.79) * mm, "end": v(-10.37, -13.7) * mm});
            skArc(sketch, "E840", {"start": v(-10.37, -13.7) * mm, "mid": v(-10.18, -13.64) * mm, "end": v(-9.98, -13.59) * mm});
            skArc(sketch, "E841", {"start": v(-9.98, -13.59) * mm, "mid": v(-9.79, -13.56) * mm, "end": v(-9.6, -13.55) * mm});
            skArc(sketch, "E842", {"start": v(-9.6, -13.55) * mm, "mid": v(-9.48, -13.55) * mm, "end": v(-9.36, -13.56) * mm});
            skArc(sketch, "E843", {"start": v(-9.36, -13.56) * mm, "mid": v(-9.29, -13.57) * mm, "end": v(-9.22, -13.6) * mm});
            skArc(sketch, "E844", {"start": v(-9.22, -13.6) * mm, "mid": v(-9.14, -13.64) * mm, "end": v(-9.08, -13.68) * mm});
            skArc(sketch, "E845", {"start": v(-9.08, -13.68) * mm, "mid": v(-8.97, -13.78) * mm, "end": v(-8.87, -13.87) * mm});
            skArc(sketch, "E846", {"start": v(-8.87, -13.87) * mm, "mid": v(-8.6, -14.14) * mm, "end": v(-8.37, -14.44) * mm});
            skArc(sketch, "E847", {"start": v(-8.37, -14.44) * mm, "mid": v(-8.1, -14.83) * mm, "end": v(-7.85, -15.24) * mm});
            skArc(sketch, "E848", {"start": v(-7.85, -15.24) * mm, "mid": v(-7.62, -15.66) * mm, "end": v(-7.41, -16.1) * mm});
            skArc(sketch, "E849", {"start": v(-7.41, -16.1) * mm, "mid": v(-7.27, -16.46) * mm, "end": v(-7.15, -16.84) * mm});
            skArc(sketch, "E850", {"start": v(-7.15, -16.84) * mm, "mid": v(-7.13, -16.95) * mm, "end": v(-7.1, -17.06) * mm});
            skArc(sketch, "E851", {"start": v(-7.1, -17.06) * mm, "mid": v(-7.08, -17.22) * mm, "end": v(-7.05, -17.37) * mm});
            skArc(sketch, "E852", {"start": v(-7.05, -17.37) * mm, "mid": v(-7.02, -17.53) * mm, "end": v(-7, -17.7) * mm});
            skArc(sketch, "E853", {"start": v(-7, -17.7) * mm, "mid": v(-6.98, -17.85) * mm, "end": v(-6.96, -18) * mm});
            skArc(sketch, "E854", {"start": v(-6.96, -18) * mm, "mid": v(-6.94, -18.2) * mm, "end": v(-6.92, -18.4) * mm});
            skArc(sketch, "E855", {"start": v(-6.92, -18.4) * mm, "mid": v(-6.91, -18.54) * mm, "end": v(-6.91, -18.67) * mm});
            skArc(sketch, "E856", {"start": v(-6.91, -18.67) * mm, "mid": v(-6.92, -18.79) * mm, "end": v(-6.94, -18.9) * mm});
            skArc(sketch, "E857", {"start": v(-6.94, -18.9) * mm, "mid": v(-6.97, -19.05) * mm, "end": v(-7, -19.2) * mm});
            skArc(sketch, "E858", {"start": v(-7, -19.2) * mm, "mid": v(-7.05, -19.38) * mm, "end": v(-7.12, -19.56) * mm});
            skArc(sketch, "E859", {"start": v(-7.12, -19.56) * mm, "mid": v(-7.2, -19.72) * mm, "end": v(-7.28, -19.86) * mm});
            skArc(sketch, "E860", {"start": v(-7.28, -19.86) * mm, "mid": v(-7.38, -20) * mm, "end": v(-7.5, -20.11) * mm});
            skArc(sketch, "E861", {"start": v(-7.5, -20.11) * mm, "mid": v(-7.62, -20.22) * mm, "end": v(-7.75, -20.3) * mm});
            skArc(sketch, "E862", {"start": v(-7.75, -20.3) * mm, "mid": v(-7.83, -20.35) * mm, "end": v(-7.9, -20.38) * mm});
            skArc(sketch, "E863", {"start": v(-7.9, -20.38) * mm, "mid": v(-8, -20.4) * mm, "end": v(-8.08, -20.42) * mm});
            skArc(sketch, "E864", {"start": v(-8.08, -20.42) * mm, "mid": v(-8.2, -20.43) * mm, "end": v(-8.31, -20.44) * mm});
            skArc(sketch, "E865", {"start": v(-8.31, -20.44) * mm, "mid": v(-8.5, -20.44) * mm, "end": v(-8.69, -20.45) * mm});
            skArc(sketch, "E866", {"start": v(-8.69, -20.45) * mm, "mid": v(-8.97, -20.44) * mm, "end": v(-9.24, -20.42) * mm});
            skArc(sketch, "E867", {"start": v(-9.24, -20.42) * mm, "mid": v(-9.42, -20.4) * mm, "end": v(-9.58, -20.33) * mm});
            skArc(sketch, "E868", {"start": v(-9.58, -20.33) * mm, "mid": v(-9.72, -20.25) * mm, "end": v(-9.84, -20.15) * mm});
            skArc(sketch, "E869", {"start": v(-9.84, -20.15) * mm, "mid": v(-9.98, -19.99) * mm, "end": v(-10.1, -19.81) * mm});
            skArc(sketch, "E870", {"start": v(-10.1, -19.81) * mm, "mid": v(-10.15, -19.74) * mm, "end": v(-10.2, -19.67) * mm});
            skArc(sketch, "E871", {"start": v(-10.2, -19.67) * mm, "mid": v(-10.25, -19.6) * mm, "end": v(-10.3, -19.55) * mm});
            skArc(sketch, "E872", {"start": v(-10.3, -19.55) * mm, "mid": v(-10.35, -19.5) * mm, "end": v(-10.4, -19.46) * mm});
            skArc(sketch, "E873", {"start": v(-10.4, -19.46) * mm, "mid": v(-10.41, -19.45) * mm, "end": v(-10.43, -19.45) * mm});
            skArc(sketch, "E874", {"start": v(-10.43, -19.45) * mm, "mid": v(-10.46, -19.46) * mm, "end": v(-10.48, -19.48) * mm});
            skArc(sketch, "E875", {"start": v(-10.48, -19.48) * mm, "mid": v(-10.53, -19.55) * mm, "end": v(-10.58, -19.61) * mm});
            skArc(sketch, "E876", {"start": v(-10.58, -19.61) * mm, "mid": v(-10.65, -19.7) * mm, "end": v(-10.7, -19.77) * mm});
            skArc(sketch, "E877", {"start": v(-10.7, -19.77) * mm, "mid": v(-10.77, -19.87) * mm, "end": v(-10.84, -19.96) * mm});
            skArc(sketch, "E878", {"start": v(-10.84, -19.96) * mm, "mid": v(-11, -20.2) * mm, "end": v(-11.19, -20.42) * mm});
            skArc(sketch, "E879", {"start": v(-11.19, -20.42) * mm, "mid": v(-11.35, -20.61) * mm, "end": v(-11.53, -20.79) * mm});
            skArc(sketch, "E880", {"start": v(-11.53, -20.79) * mm, "mid": v(-11.7, -20.93) * mm, "end": v(-11.89, -21.06) * mm});
            skArc(sketch, "E881", {"start": v(-11.89, -21.06) * mm, "mid": v(-12.06, -21.16) * mm, "end": v(-12.25, -21.24) * mm});
            skArc(sketch, "E882", {"start": v(-12.25, -21.24) * mm, "mid": v(-12.53, -21.33) * mm, "end": v(-12.83, -21.37) * mm});
            skArc(sketch, "E883", {"start": v(-12.83, -21.37) * mm, "mid": v(-13.1, -21.37) * mm, "end": v(-13.35, -21.31) * mm});
            skArc(sketch, "E884", {"start": v(-13.35, -21.31) * mm, "mid": v(-13.63, -21.2) * mm, "end": v(-13.9, -21.04) * mm});
            skArc(sketch, "E885", {"start": v(-13.9, -21.04) * mm, "mid": v(-14.21, -20.8) * mm, "end": v(-14.51, -20.53) * mm});
            skArc(sketch, "E886", {"start": v(-14.51, -20.53) * mm, "mid": v(-14.72, -20.32) * mm, "end": v(-14.92, -20.09) * mm});
            skArc(sketch, "E887", {"start": v(-14.92, -20.09) * mm, "mid": v(-15.08, -19.86) * mm, "end": v(-15.23, -19.63) * mm});
            skArc(sketch, "E888", {"start": v(-15.23, -19.63) * mm, "mid": v(-15.35, -19.38) * mm, "end": v(-15.45, -19.13) * mm});
            skArc(sketch, "E889", {"start": v(-15.45, -19.13) * mm, "mid": v(-15.53, -18.86) * mm, "end": v(-15.58, -18.6) * mm});
            skArc(sketch, "E890", {"start": v(-15.58, -18.6) * mm, "mid": v(-15.63, -18.2) * mm, "end": v(-15.65, -17.81) * mm});
            skArc(sketch, "E891", {"start": v(-15.65, -17.81) * mm, "mid": v(-15.65, -17.1) * mm, "end": v(-15.64, -16.4) * mm});
            skArc(sketch, "E892", {"start": v(-15.64, -16.4) * mm, "mid": v(-15.62, -15.7) * mm, "end": v(-15.6, -14.98) * mm});
            skArc(sketch, "E893", {"start": v(-15.6, -14.98) * mm, "mid": v(-15.56, -14.7) * mm, "end": v(-15.49, -14.41) * mm});
            skArc(sketch, "E894", {"start": v(-15.49, -14.41) * mm, "mid": v(-15.43, -14.26) * mm, "end": v(-15.35, -14.11) * mm});
            skArc(sketch, "E895", {"start": v(-15.35, -14.11) * mm, "mid": v(-15.26, -13.98) * mm, "end": v(-15.15, -13.86) * mm});
            skArc(sketch, "E896", {"start": v(-15.15, -13.86) * mm, "mid": v(-15.03, -13.76) * mm, "end": v(-14.9, -13.68) * mm});
            skArc(sketch, "E897", {"start": v(-14.9, -13.68) * mm, "mid": v(-14.76, -13.62) * mm, "end": v(-14.62, -13.58) * mm});
            skArc(sketch, "E898", {"start": v(-14.62, -13.58) * mm, "mid": v(-14.57, -13.58) * mm, "end": v(-14.52, -13.57) * mm});
            skArc(sketch, "E899", {"start": v(-14.52, -13.57) * mm, "mid": v(-14.46, -13.56) * mm, "end": v(-14.4, -13.55) * mm});
            skArc(sketch, "E900", {"start": v(-14.4, -13.55) * mm, "mid": v(-14.36, -13.54) * mm, "end": v(-14.31, -13.53) * mm});
            skArc(sketch, "E901", {"start": v(-14.31, -13.53) * mm, "mid": v(-14.28, -13.52) * mm, "end": v(-14.25, -13.52) * mm});
            skArc(sketch, "E902", {"start": v(-14.25, -13.52) * mm, "mid": v(-14.12, -13.5) * mm, "end": v(-13.99, -13.5) * mm});
            skArc(sketch, "E903", {"start": v(-13.99, -13.5) * mm, "mid": v(-13.78, -13.5) * mm, "end": v(-13.56, -13.53) * mm});
            skArc(sketch, "E904", {"start": v(-13.56, -13.53) * mm, "mid": v(-13.35, -13.57) * mm, "end": v(-13.14, -13.61) * mm});
            skArc(sketch, "E905", {"start": v(-13.14, -13.61) * mm, "mid": v(-13, -13.66) * mm, "end": v(-12.85, -13.72) * mm});
            skArc(sketch, "E906", {"start": v(-19.13, 19.85) * mm, "mid": v(-19.44, 19.7) * mm, "end": v(-19.73, 19.51) * mm});
            skArc(sketch, "E907", {"start": v(-19.73, 19.51) * mm, "mid": v(-20, 19.25) * mm, "end": v(-20.22, 18.96) * mm});
            skArc(sketch, "E908", {"start": v(-20.22, 18.96) * mm, "mid": v(-20.51, 18.47) * mm, "end": v(-20.77, 17.96) * mm});
            skArc(sketch, "E909", {"start": v(-20.77, 17.96) * mm, "mid": v(-21.26, 16.9) * mm, "end": v(-21.74, 15.85) * mm});
            skArc(sketch, "E910", {"start": v(-21.74, 15.85) * mm, "mid": v(-21.88, 15.54) * mm, "end": v(-22.02, 15.23) * mm});
            skArc(sketch, "E911", {"start": v(-22.02, 15.23) * mm, "mid": v(-22.15, 14.95) * mm, "end": v(-22.28, 14.67) * mm});
            skArc(sketch, "E912", {"start": v(-22.28, 14.67) * mm, "mid": v(-22.4, 14.44) * mm, "end": v(-22.52, 14.2) * mm});
            skArc(sketch, "E913", {"start": v(-22.52, 14.2) * mm, "mid": v(-22.56, 14.12) * mm, "end": v(-22.62, 14.05) * mm});
            skArc(sketch, "E914", {"start": v(-22.62, 14.05) * mm, "mid": v(-22.77, 13.93) * mm, "end": v(-22.96, 13.88) * mm});
            skArc(sketch, "E915", {"start": v(-22.96, 13.88) * mm, "mid": v(-23.15, 13.91) * mm, "end": v(-23.3, 14.03) * mm});
            skArc(sketch, "E916", {"start": v(-23.3, 14.03) * mm, "mid": v(-23.56, 14.33) * mm, "end": v(-23.78, 14.66) * mm});
            skArc(sketch, "E917", {"start": v(-23.78, 14.66) * mm, "mid": v(-24.2, 15.4) * mm, "end": v(-24.62, 16.17) * mm});
            skArc(sketch, "E918", {"start": v(-24.62, 16.17) * mm, "mid": v(-24.9, 16.69) * mm, "end": v(-25.19, 17.2) * mm});
            skArc(sketch, "E919", {"start": v(-25.19, 17.2) * mm, "mid": v(-25.44, 17.64) * mm, "end": v(-25.7, 18.07) * mm});
            skArc(sketch, "E920", {"start": v(-25.7, 18.07) * mm, "mid": v(-25.93, 18.41) * mm, "end": v(-26.16, 18.75) * mm});
            skArc(sketch, "E921", {"start": v(-26.16, 18.75) * mm, "mid": v(-26.32, 18.96) * mm, "end": v(-26.5, 19.16) * mm});
            skArc(sketch, "E922", {"start": v(-26.5, 19.16) * mm, "mid": v(-26.82, 19.43) * mm, "end": v(-27.19, 19.63) * mm});
            skArc(sketch, "E923", {"start": v(-27.19, 19.63) * mm, "mid": v(-27.64, 19.77) * mm, "end": v(-28.12, 19.85) * mm});
            skArc(sketch, "E924", {"start": v(-28.12, 19.85) * mm, "mid": v(-28.84, 19.88) * mm, "end": v(-29.56, 19.85) * mm});
            skArc(sketch, "E925", {"start": v(-29.56, 19.85) * mm, "mid": v(-30.85, 19.75) * mm, "end": v(-32.14, 19.62) * mm});
            skArc(sketch, "E926", {"start": v(-32.14, 19.62) * mm, "mid": v(-32.95, 19.53) * mm, "end": v(-33.76, 19.43) * mm});
            skArc(sketch, "E927", {"start": v(-33.76, 19.43) * mm, "mid": v(-34.22, 19.35) * mm, "end": v(-34.67, 19.24) * mm});
            skArc(sketch, "E928", {"start": v(-34.67, 19.24) * mm, "mid": v(-35, 19.12) * mm, "end": v(-35.3, 18.97) * mm});
            skArc(sketch, "E929", {"start": v(-35.3, 18.97) * mm, "mid": v(-35.6, 18.77) * mm, "end": v(-35.89, 18.54) * mm});
            skArc(sketch, "E930", {"start": v(-35.89, 18.54) * mm, "mid": v(-35.98, 18.45) * mm, "end": v(-36.08, 18.37) * mm});
            skArc(sketch, "E931", {"start": v(-36.08, 18.37) * mm, "mid": v(-36.16, 18.3) * mm, "end": v(-36.25, 18.22) * mm});
            skArc(sketch, "E932", {"start": v(-36.25, 18.22) * mm, "mid": v(-36.33, 18.16) * mm, "end": v(-36.4, 18.1) * mm});
            skArc(sketch, "E933", {"start": v(-36.4, 18.1) * mm, "mid": v(-36.42, 18.1) * mm, "end": v(-36.45, 18.09) * mm});
            skArc(sketch, "E934", {"start": v(-36.45, 18.09) * mm, "mid": v(-36.47, 18.1) * mm, "end": v(-36.49, 18.1) * mm});
            skArc(sketch, "E935", {"start": v(-36.49, 18.1) * mm, "mid": v(-36.56, 18.16) * mm, "end": v(-36.62, 18.23) * mm});
            skArc(sketch, "E936", {"start": v(-36.62, 18.23) * mm, "mid": v(-36.7, 18.3) * mm, "end": v(-36.78, 18.37) * mm});
            skArc(sketch, "E937", {"start": v(-36.78, 18.37) * mm, "mid": v(-36.87, 18.46) * mm, "end": v(-36.95, 18.55) * mm});
            skArc(sketch, "E938", {"start": v(-36.95, 18.55) * mm, "mid": v(-37.19, 18.8) * mm, "end": v(-37.43, 19.02) * mm});
            skArc(sketch, "E939", {"start": v(-37.43, 19.02) * mm, "mid": v(-37.6, 19.16) * mm, "end": v(-37.77, 19.27) * mm});
            skArc(sketch, "E940", {"start": v(-37.77, 19.27) * mm, "mid": v(-37.95, 19.36) * mm, "end": v(-38.14, 19.42) * mm});
            skArc(sketch, "E941", {"start": v(-38.14, 19.42) * mm, "mid": v(-38.39, 19.46) * mm, "end": v(-38.64, 19.5) * mm});
            skArc(sketch, "E942", {"start": v(-38.64, 19.5) * mm, "mid": v(-39.34, 19.55) * mm, "end": v(-40.04, 19.57) * mm});
            skArc(sketch, "E943", {"start": v(-40.04, 19.57) * mm, "mid": v(-42.4, 19.6) * mm, "end": v(-44.74, 19.6) * mm});
            skArc(sketch, "E944", {"start": v(-44.74, 19.6) * mm, "mid": v(-47.04, 19.61) * mm, "end": v(-49.34, 19.6) * mm});
            skArc(sketch, "E945", {"start": v(-49.34, 19.6) * mm, "mid": v(-50.71, 19.6) * mm, "end": v(-52.09, 19.56) * mm});
            skArc(sketch, "E946", {"start": v(-52.09, 19.56) * mm, "mid": v(-53.71, 19.5) * mm, "end": v(-55.34, 19.47) * mm});
            skArc(sketch, "E947", {"start": v(-55.34, 19.47) * mm, "mid": v(-56.5, 19.44) * mm, "end": v(-57.67, 19.43) * mm});
            skArc(sketch, "E948", {"start": v(-57.67, 19.43) * mm, "mid": v(-58.57, 19.43) * mm, "end": v(-59.46, 19.45) * mm});
            skArc(sketch, "E949", {"start": v(-59.46, 19.45) * mm, "mid": v(-60.2, 19.48) * mm, "end": v(-60.93, 19.52) * mm});
            skArc(sketch, "E950", {"start": v(-60.93, 19.52) * mm, "mid": v(-61.94, 19.59) * mm, "end": v(-62.96, 19.61) * mm});
            skArc(sketch, "E951", {"start": v(-62.96, 19.61) * mm, "mid": v(-63.78, 19.59) * mm, "end": v(-64.6, 19.51) * mm});
            skArc(sketch, "E952", {"start": v(-64.6, 19.51) * mm, "mid": v(-65.23, 19.4) * mm, "end": v(-65.84, 19.25) * mm});
            skArc(sketch, "E953", {"start": v(-65.84, 19.25) * mm, "mid": v(-66.26, 19.07) * mm, "end": v(-66.63, 18.8) * mm});
            skArc(sketch, "E954", {"start": v(-66.63, 18.8) * mm, "mid": v(-66.8, 18.63) * mm, "end": v(-66.93, 18.43) * mm});
            skArc(sketch, "E955", {"start": v(-66.93, 18.43) * mm, "mid": v(-67.02, 18.22) * mm, "end": v(-67.07, 18) * mm});
            skArc(sketch, "E956", {"start": v(-67.07, 18) * mm, "mid": v(-67.12, 17.62) * mm, "end": v(-67.14, 17.24) * mm});
            skArc(sketch, "E957", {"start": v(-67.14, 17.24) * mm, "mid": v(-67.16, 16.08) * mm, "end": v(-67.18, 14.92) * mm});
            skArc(sketch, "E958", {"start": v(-67.18, 14.92) * mm, "mid": v(-67.2, 14.3) * mm, "end": v(-67.2, 13.67) * mm});
            skArc(sketch, "E959", {"start": v(-67.2, 13.67) * mm, "mid": v(-67.22, 13.11) * mm, "end": v(-67.24, 12.56) * mm});
            skArc(sketch, "E960", {"start": v(-67.24, 12.56) * mm, "mid": v(-67.26, 12.1) * mm, "end": v(-67.28, 11.64) * mm});
            skArc(sketch, "E961", {"start": v(-67.28, 11.64) * mm, "mid": v(-67.29, 11.48) * mm, "end": v(-67.31, 11.32) * mm});
            skArc(sketch, "E962", {"start": v(-67.31, 11.32) * mm, "mid": v(-67.35, 11.11) * mm, "end": v(-67.4, 10.9) * mm});
            skArc(sketch, "E963", {"start": v(-67.4, 10.9) * mm, "mid": v(-67.47, 10.74) * mm, "end": v(-67.55, 10.58) * mm});
            skArc(sketch, "E964", {"start": v(-67.55, 10.58) * mm, "mid": v(-67.63, 10.45) * mm, "end": v(-67.73, 10.33) * mm});
            skArc(sketch, "E965", {"start": v(-67.73, 10.33) * mm, "mid": v(-67.84, 10.24) * mm, "end": v(-67.95, 10.17) * mm});
            skArc(sketch, "E966", {"start": v(-67.95, 10.17) * mm, "mid": v(-68.14, 10.09) * mm, "end": v(-68.34, 10.04) * mm});
            skArc(sketch, "E967", {"start": v(-68.34, 10.04) * mm, "mid": v(-68.67, 9.99) * mm, "end": v(-69, 9.95) * mm});
            skArc(sketch, "E968", {"start": v(-69, 9.95) * mm, "mid": v(-69.43, 9.93) * mm, "end": v(-69.86, 9.91) * mm});
            skArc(sketch, "E969", {"start": v(-69.86, 9.91) * mm, "mid": v(-70.4, 9.9) * mm, "end": v(-70.95, 9.91) * mm});
            skArc(sketch, "E970", {"start": v(-70.95, 9.91) * mm, "mid": v(-71.45, 9.92) * mm, "end": v(-71.95, 9.94) * mm});
            skArc(sketch, "E971", {"start": v(-71.95, 9.94) * mm, "mid": v(-72.17, 9.96) * mm, "end": v(-72.4, 10) * mm});
            skArc(sketch, "E972", {"start": v(-72.4, 10) * mm, "mid": v(-72.52, 10.03) * mm, "end": v(-72.63, 10.1) * mm});
            skArc(sketch, "E973", {"start": v(-72.63, 10.1) * mm, "mid": v(-72.72, 10.18) * mm, "end": v(-72.77, 10.28) * mm});
            skArc(sketch, "E974", {"start": v(-72.77, 10.28) * mm, "mid": v(-72.83, 10.46) * mm, "end": v(-72.86, 10.64) * mm});
            skArc(sketch, "E975", {"start": v(-72.86, 10.64) * mm, "mid": v(-72.9, 11.03) * mm, "end": v(-72.93, 11.42) * mm});
            skArc(sketch, "E976", {"start": v(-72.93, 11.42) * mm, "mid": v(-72.97, 11.97) * mm, "end": v(-73, 12.52) * mm});
            skArc(sketch, "E977", {"start": v(-73, 12.52) * mm, "mid": v(-73.03, 13.27) * mm, "end": v(-73.05, 14.03) * mm});
            skArc(sketch, "E978", {"start": v(-73.05, 14.03) * mm, "mid": v(-73.1, 15.2) * mm, "end": v(-73.15, 16.38) * mm});
            skArc(sketch, "E979", {"start": v(-73.15, 16.38) * mm, "mid": v(-73.2, 17) * mm, "end": v(-73.29, 17.62) * mm});
            skArc(sketch, "E980", {"start": v(-73.29, 17.62) * mm, "mid": v(-73.38, 18) * mm, "end": v(-73.5, 18.38) * mm});
            skArc(sketch, "E981", {"start": v(-73.5, 18.38) * mm, "mid": v(-73.66, 18.66) * mm, "end": v(-73.86, 18.9) * mm});
            skArc(sketch, "E982", {"start": v(-73.86, 18.9) * mm, "mid": v(-74.02, 19.04) * mm, "end": v(-74.2, 19.16) * mm});
            skArc(sketch, "E983", {"start": v(-74.2, 19.16) * mm, "mid": v(-74.39, 19.25) * mm, "end": v(-74.59, 19.32) * mm});
            skArc(sketch, "E984", {"start": v(-74.59, 19.32) * mm, "mid": v(-74.86, 19.38) * mm, "end": v(-75.13, 19.42) * mm});
            skArc(sketch, "E985", {"start": v(-75.13, 19.42) * mm, "mid": v(-75.58, 19.47) * mm, "end": v(-76.02, 19.5) * mm});
            skArc(sketch, "E986", {"start": v(-76.02, 19.5) * mm, "mid": v(-76.33, 19.53) * mm, "end": v(-76.64, 19.54) * mm});
            skArc(sketch, "E987", {"start": v(-76.64, 19.54) * mm, "mid": v(-76.95, 19.55) * mm, "end": v(-77.26, 19.55) * mm});
            skArc(sketch, "E988", {"start": v(-77.26, 19.55) * mm, "mid": v(-77.6, 19.55) * mm, "end": v(-77.96, 19.54) * mm});
            skArc(sketch, "E989", {"start": v(-77.96, 19.54) * mm, "mid": v(-78.39, 19.52) * mm, "end": v(-78.82, 19.5) * mm});
            skArc(sketch, "E990", {"start": v(-78.82, 19.5) * mm, "mid": v(-79.57, 19.46) * mm, "end": v(-80.32, 19.4) * mm});
            skArc(sketch, "E991", {"start": v(-80.32, 19.4) * mm, "mid": v(-80.7, 19.35) * mm, "end": v(-81.07, 19.25) * mm});
            skArc(sketch, "E992", {"start": v(-81.07, 19.25) * mm, "mid": v(-81.3, 19.14) * mm, "end": v(-81.5, 18.97) * mm});
            skArc(sketch, "E993", {"start": v(-81.5, 18.97) * mm, "mid": v(-81.66, 18.76) * mm, "end": v(-81.77, 18.52) * mm});
            skArc(sketch, "E994", {"start": v(-81.77, 18.52) * mm, "mid": v(-81.88, 18.08) * mm, "end": v(-81.94, 17.63) * mm});
            skArc(sketch, "E995", {"start": v(-81.94, 17.63) * mm, "mid": v(-81.99, 16.86) * mm, "end": v(-82.01, 16.08) * mm});
            skArc(sketch, "E996", {"start": v(-82.01, 16.08) * mm, "mid": v(-82.03, 14.64) * mm, "end": v(-82.04, 13.2) * mm});
            skArc(sketch, "E997", {"start": v(-82.04, 13.2) * mm, "mid": v(-82.05, 9.1) * mm, "end": v(-82.05, 5.01) * mm});
            skLineSegment(sketch, "E998", {"start": v(-82.05, 5.01) * mm, "end": v(-82.04, -6.9) * mm});
            skLineSegment(sketch, "E999", {"start": v(-82.04, -6.9) * mm, "end": v(-81.63, -7.32) * mm});
            skArc(sketch, "E1000", {"start": v(-81.63, -7.32) * mm, "mid": v(-81.4, -7.54) * mm, "end": v(-81.13, -7.73) * mm});
            skArc(sketch, "E1001", {"start": v(-81.13, -7.73) * mm, "mid": v(-80.9, -7.84) * mm, "end": v(-80.66, -7.9) * mm});
            skArc(sketch, "E1002", {"start": v(-80.66, -7.9) * mm, "mid": v(-80.29, -7.96) * mm, "end": v(-79.9, -7.98) * mm});
            skArc(sketch, "E1003", {"start": v(-79.9, -7.98) * mm, "mid": v(-78.77, -7.98) * mm, "end": v(-77.64, -7.99) * mm});
            skArc(sketch, "E1004", {"start": v(-77.64, -7.99) * mm, "mid": v(-76.8, -7.98) * mm, "end": v(-75.95, -7.98) * mm});
            skArc(sketch, "E1005", {"start": v(-75.95, -7.98) * mm, "mid": v(-75.54, -7.98) * mm, "end": v(-75.13, -7.97) * mm});
            skArc(sketch, "E1006", {"start": v(-75.13, -7.97) * mm, "mid": v(-74.88, -7.95) * mm, "end": v(-74.64, -7.93) * mm});
            skArc(sketch, "E1007", {"start": v(-74.64, -7.93) * mm, "mid": v(-74.47, -7.9) * mm, "end": v(-74.3, -7.86) * mm});
            skArc(sketch, "E1008", {"start": v(-74.3, -7.86) * mm, "mid": v(-74.13, -7.8) * mm, "end": v(-73.97, -7.71) * mm});
            skArc(sketch, "E1009", {"start": v(-73.97, -7.71) * mm, "mid": v(-73.81, -7.6) * mm, "end": v(-73.68, -7.48) * mm});
            skArc(sketch, "E1010", {"start": v(-73.68, -7.48) * mm, "mid": v(-73.56, -7.34) * mm, "end": v(-73.46, -7.18) * mm});
            skArc(sketch, "E1011", {"start": v(-73.46, -7.18) * mm, "mid": v(-73.37, -7) * mm, "end": v(-73.3, -6.82) * mm});
            skArc(sketch, "E1012", {"start": v(-73.3, -6.82) * mm, "mid": v(-73.25, -6.6) * mm, "end": v(-73.21, -6.37) * mm});
            skArc(sketch, "E1013", {"start": v(-73.21, -6.37) * mm, "mid": v(-73.17, -5.97) * mm, "end": v(-73.13, -5.57) * mm});
            skArc(sketch, "E1014", {"start": v(-73.13, -5.57) * mm, "mid": v(-73.1, -5.04) * mm, "end": v(-73.07, -4.5) * mm});
            skArc(sketch, "E1015", {"start": v(-73.07, -4.5) * mm, "mid": v(-73.04, -3.83) * mm, "end": v(-73.02, -3.16) * mm});
            skArc(sketch, "E1016", {"start": v(-73.02, -3.16) * mm, "mid": v(-72.99, -2.25) * mm, "end": v(-72.95, -1.35) * mm});
            skArc(sketch, "E1017", {"start": v(-72.95, -1.35) * mm, "mid": v(-72.91, -0.7) * mm, "end": v(-72.85, -0.04) * mm});
            skArc(sketch, "E1018", {"start": v(-72.85, -0.04) * mm, "mid": v(-72.8, 0.43) * mm, "end": v(-72.74, 0.91) * mm});
            skArc(sketch, "E1019", {"start": v(-72.74, 0.91) * mm, "mid": v(-72.69, 1.08) * mm, "end": v(-72.59, 1.23) * mm});
            skArc(sketch, "E1020", {"start": v(-72.59, 1.23) * mm, "mid": v(-72.49, 1.31) * mm, "end": v(-72.36, 1.36) * mm});
            skArc(sketch, "E1021", {"start": v(-72.36, 1.36) * mm, "mid": v(-72.12, 1.42) * mm, "end": v(-71.88, 1.46) * mm});
            skArc(sketch, "E1022", {"start": v(-71.88, 1.46) * mm, "mid": v(-71.54, 1.5) * mm, "end": v(-71.2, 1.51) * mm});
            skArc(sketch, "E1023", {"start": v(-71.2, 1.51) * mm, "mid": v(-70.74, 1.53) * mm, "end": v(-70.29, 1.53) * mm});
            skArc(sketch, "E1024", {"start": v(-70.29, 1.53) * mm, "mid": v(-69.82, 1.53) * mm, "end": v(-69.36, 1.51) * mm});
            skArc(sketch, "E1025", {"start": v(-69.36, 1.51) * mm, "mid": v(-69, 1.49) * mm, "end": v(-68.65, 1.45) * mm});
            skArc(sketch, "E1026", {"start": v(-68.65, 1.45) * mm, "mid": v(-68.4, 1.4) * mm, "end": v(-68.14, 1.35) * mm});
            skArc(sketch, "E1027", {"start": v(-68.14, 1.35) * mm, "mid": v(-67.98, 1.3) * mm, "end": v(-67.84, 1.2) * mm});
            skArc(sketch, "E1028", {"start": v(-67.84, 1.2) * mm, "mid": v(-67.8, 1.18) * mm, "end": v(-67.77, 1.14) * mm});
            skArc(sketch, "E1029", {"start": v(-67.77, 1.14) * mm, "mid": v(-67.73, 1.09) * mm, "end": v(-67.7, 1.04) * mm});
            skArc(sketch, "E1030", {"start": v(-67.7, 1.04) * mm, "mid": v(-67.66, 0.98) * mm, "end": v(-67.63, 0.92) * mm});
            skArc(sketch, "E1031", {"start": v(-67.63, 0.92) * mm, "mid": v(-67.61, 0.87) * mm, "end": v(-67.6, 0.81) * mm});
            skArc(sketch, "E1032", {"start": v(-67.6, 0.81) * mm, "mid": v(-67.57, 0.71) * mm, "end": v(-67.55, 0.6) * mm});
            skArc(sketch, "E1033", {"start": v(-67.55, 0.6) * mm, "mid": v(-67.54, 0.22) * mm, "end": v(-67.52, -0.16) * mm});
            skArc(sketch, "E1034", {"start": v(-67.52, -0.16) * mm, "mid": v(-67.5, -0.64) * mm, "end": v(-67.48, -1.13) * mm});
            skArc(sketch, "E1035", {"start": v(-67.48, -1.13) * mm, "mid": v(-67.47, -1.74) * mm, "end": v(-67.45, -2.35) * mm});
            skArc(sketch, "E1036", {"start": v(-67.45, -2.35) * mm, "mid": v(-67.44, -2.93) * mm, "end": v(-67.43, -3.5) * mm});
            skArc(sketch, "E1037", {"start": v(-67.43, -3.5) * mm, "mid": v(-67.41, -4.04) * mm, "end": v(-67.4, -4.58) * mm});
            skArc(sketch, "E1038", {"start": v(-67.4, -4.58) * mm, "mid": v(-67.37, -5.02) * mm, "end": v(-67.35, -5.47) * mm});
            skArc(sketch, "E1039", {"start": v(-67.35, -5.47) * mm, "mid": v(-67.34, -5.66) * mm, "end": v(-67.32, -5.84) * mm});
            skArc(sketch, "E1040", {"start": v(-67.32, -5.84) * mm, "mid": v(-67.24, -6.26) * mm, "end": v(-67.14, -6.67) * mm});
            skArc(sketch, "E1041", {"start": v(-67.14, -6.67) * mm, "mid": v(-67.03, -6.96) * mm, "end": v(-66.87, -7.24) * mm});
            skArc(sketch, "E1042", {"start": v(-66.87, -7.24) * mm, "mid": v(-66.7, -7.45) * mm, "end": v(-66.47, -7.63) * mm});
            skArc(sketch, "E1043", {"start": v(-66.47, -7.63) * mm, "mid": v(-66.2, -7.78) * mm, "end": v(-65.9, -7.9) * mm});
            skArc(sketch, "E1044", {"start": v(-65.9, -7.9) * mm, "mid": v(-65.72, -7.94) * mm, "end": v(-65.55, -7.98) * mm});
            skArc(sketch, "E1045", {"start": v(-65.55, -7.98) * mm, "mid": v(-65.38, -8.01) * mm, "end": v(-65.21, -8.03) * mm});
            skArc(sketch, "E1046", {"start": v(-65.21, -8.03) * mm, "mid": v(-64.97, -8.04) * mm, "end": v(-64.73, -8.05) * mm});
            skArc(sketch, "E1047", {"start": v(-64.73, -8.05) * mm, "mid": v(-64.24, -8.05) * mm, "end": v(-63.74, -8.05) * mm});
            skArc(sketch, "E1048", {"start": v(-63.74, -8.05) * mm, "mid": v(-63.36, -8.05) * mm, "end": v(-62.97, -8.05) * mm});
            skArc(sketch, "E1049", {"start": v(-62.97, -8.05) * mm, "mid": v(-62.48, -8.04) * mm, "end": v(-61.99, -8.03) * mm});
            skArc(sketch, "E1050", {"start": v(-61.99, -8.03) * mm, "mid": v(-61.48, -8.01) * mm, "end": v(-60.97, -8) * mm});
            skArc(sketch, "E1051", {"start": v(-60.97, -8) * mm, "mid": v(-60.52, -7.98) * mm, "end": v(-60.07, -7.96) * mm});
            skArc(sketch, "E1052", {"start": v(-60.07, -7.96) * mm, "mid": v(-59.38, -7.93) * mm, "end": v(-58.69, -7.9) * mm});
            skArc(sketch, "E1053", {"start": v(-58.69, -7.9) * mm, "mid": v(-57.96, -7.9) * mm, "end": v(-57.22, -7.9) * mm});
            skArc(sketch, "E1054", {"start": v(-57.22, -7.9) * mm, "mid": v(-56.17, -7.9) * mm, "end": v(-55.12, -7.91) * mm});
            skArc(sketch, "E1055", {"start": v(-55.12, -7.91) * mm, "mid": v(-53.17, -7.94) * mm, "end": v(-51.21, -7.98) * mm});
            skArc(sketch, "E1056", {"start": v(-51.21, -7.98) * mm, "mid": v(-48.32, -8.02) * mm, "end": v(-45.43, -8.06) * mm});
            skArc(sketch, "E1057", {"start": v(-45.43, -8.06) * mm, "mid": v(-43.49, -8.08) * mm, "end": v(-41.55, -8.1) * mm});
            skArc(sketch, "E1058", {"start": v(-41.55, -8.1) * mm, "mid": v(-40.15, -8.09) * mm, "end": v(-38.75, -8.08) * mm});
            skArc(sketch, "E1059", {"start": v(-38.75, -8.08) * mm, "mid": v(-38.4, -8.06) * mm, "end": v(-38.03, -7.99) * mm});
            skArc(sketch, "E1060", {"start": v(-38.03, -7.99) * mm, "mid": v(-37.84, -7.93) * mm, "end": v(-37.66, -7.87) * mm});
            skArc(sketch, "E1061", {"start": v(-37.66, -7.87) * mm, "mid": v(-37.49, -7.8) * mm, "end": v(-37.32, -7.72) * mm});
            skArc(sketch, "E1062", {"start": v(-37.32, -7.72) * mm, "mid": v(-37.14, -7.62) * mm, "end": v(-36.96, -7.5) * mm});
            skArc(sketch, "E1063", {"start": v(-36.96, -7.5) * mm, "mid": v(-36.74, -7.36) * mm, "end": v(-36.52, -7.2) * mm});
            skArc(sketch, "E1064", {"start": v(-36.52, -7.2) * mm, "mid": v(-36.34, -7.08) * mm, "end": v(-36.14, -6.96) * mm});
            skArc(sketch, "E1065", {"start": v(-36.14, -6.96) * mm, "mid": v(-36, -6.9) * mm, "end": v(-35.87, -6.85) * mm});
            skArc(sketch, "E1066", {"start": v(-35.87, -6.85) * mm, "mid": v(-35.74, -6.83) * mm, "end": v(-35.6, -6.84) * mm});
            skArc(sketch, "E1067", {"start": v(-35.6, -6.84) * mm, "mid": v(-35.45, -6.88) * mm, "end": v(-35.3, -6.94) * mm});
            skArc(sketch, "E1068", {"start": v(-35.3, -6.94) * mm, "mid": v(-35.07, -7.02) * mm, "end": v(-34.83, -7.1) * mm});
            skArc(sketch, "E1069", {"start": v(-34.83, -7.1) * mm, "mid": v(-34.27, -7.24) * mm, "end": v(-33.71, -7.39) * mm});
            skArc(sketch, "E1070", {"start": v(-33.71, -7.39) * mm, "mid": v(-33.1, -7.54) * mm, "end": v(-32.48, -7.68) * mm});
            skArc(sketch, "E1071", {"start": v(-32.48, -7.68) * mm, "mid": v(-31.93, -7.8) * mm, "end": v(-31.37, -7.92) * mm});
            skArc(sketch, "E1072", {"start": v(-31.37, -7.92) * mm, "mid": v(-31.02, -8) * mm, "end": v(-30.67, -8.06) * mm});
            skArc(sketch, "E1073", {"start": v(-30.67, -8.06) * mm, "mid": v(-30.42, -8.1) * mm, "end": v(-30.18, -8.14) * mm});
            skArc(sketch, "E1074", {"start": v(-30.18, -8.14) * mm, "mid": v(-29.95, -8.16) * mm, "end": v(-29.73, -8.17) * mm});
            skArc(sketch, "E1075", {"start": v(-29.73, -8.17) * mm, "mid": v(-29.46, -8.18) * mm, "end": v(-29.2, -8.19) * mm});
            skArc(sketch, "E1076", {"start": v(-29.2, -8.19) * mm, "mid": v(-28.92, -8.2) * mm, "end": v(-28.64, -8.19) * mm});
            skArc(sketch, "E1077", {"start": v(-28.64, -8.19) * mm, "mid": v(-28.5, -8.18) * mm, "end": v(-28.37, -8.17) * mm});
            skArc(sketch, "E1078", {"start": v(-28.37, -8.17) * mm, "mid": v(-28.26, -8.15) * mm, "end": v(-28.15, -8.11) * mm});
            skArc(sketch, "E1079", {"start": v(-28.15, -8.11) * mm, "mid": v(-28.03, -8.06) * mm, "end": v(-27.9, -8) * mm});
            skArc(sketch, "E1080", {"start": v(-27.9, -8) * mm, "mid": v(-27.67, -7.86) * mm, "end": v(-27.47, -7.68) * mm});
            skArc(sketch, "E1081", {"start": v(-27.47, -7.68) * mm, "mid": v(-27.24, -7.4) * mm, "end": v(-27.03, -7.1) * mm});
            skArc(sketch, "E1082", {"start": v(-27.03, -7.1) * mm, "mid": v(-26.72, -6.6) * mm, "end": v(-26.44, -6.1) * mm});
            skArc(sketch, "E1083", {"start": v(-26.44, -6.1) * mm, "mid": v(-25.9, -5.08) * mm, "end": v(-25.37, -4.07) * mm});
            skArc(sketch, "E1084", {"start": v(-25.37, -4.07) * mm, "mid": v(-24.93, -3.22) * mm, "end": v(-24.48, -2.38) * mm});
            skArc(sketch, "E1085", {"start": v(-24.48, -2.38) * mm, "mid": v(-24.24, -1.95) * mm, "end": v(-23.99, -1.53) * mm});
            skArc(sketch, "E1086", {"start": v(-23.99, -1.53) * mm, "mid": v(-23.83, -1.3) * mm, "end": v(-23.65, -1.07) * mm});
            skArc(sketch, "E1087", {"start": v(-23.65, -1.07) * mm, "mid": v(-23.53, -0.98) * mm, "end": v(-23.4, -0.95) * mm});
            skArc(sketch, "E1088", {"start": v(-23.4, -0.95) * mm, "mid": v(-23.27, -0.98) * mm, "end": v(-23.17, -1.07) * mm});
            skArc(sketch, "E1089", {"start": v(-23.17, -1.07) * mm, "mid": v(-22.9, -1.47) * mm, "end": v(-22.63, -1.88) * mm});
            skArc(sketch, "E1090", {"start": v(-22.63, -1.88) * mm, "mid": v(-22.27, -2.46) * mm, "end": v(-21.92, -3.04) * mm});
            skArc(sketch, "E1091", {"start": v(-21.92, -3.04) * mm, "mid": v(-21.43, -3.9) * mm, "end": v(-20.94, -4.77) * mm});
            skArc(sketch, "E1092", {"start": v(-20.94, -4.77) * mm, "mid": v(-20.61, -5.35) * mm, "end": v(-20.28, -5.93) * mm});
            skArc(sketch, "E1093", {"start": v(-20.28, -5.93) * mm, "mid": v(-20.04, -6.33) * mm, "end": v(-19.8, -6.72) * mm});
            skArc(sketch, "E1094", {"start": v(-19.8, -6.72) * mm, "mid": v(-19.6, -7) * mm, "end": v(-19.4, -7.28) * mm});
            skArc(sketch, "E1095", {"start": v(-19.4, -7.28) * mm, "mid": v(-19.25, -7.46) * mm, "end": v(-19.08, -7.63) * mm});
            skArc(sketch, "E1096", {"start": v(-19.08, -7.63) * mm, "mid": v(-18.92, -7.77) * mm, "end": v(-18.75, -7.88) * mm});
            skArc(sketch, "E1097", {"start": v(-18.75, -7.88) * mm, "mid": v(-18.56, -8) * mm, "end": v(-18.37, -8.09) * mm});
            skArc(sketch, "E1098", {"start": v(-18.37, -8.09) * mm, "mid": v(-18.17, -8.16) * mm, "end": v(-17.97, -8.22) * mm});
            skArc(sketch, "E1099", {"start": v(-17.97, -8.22) * mm, "mid": v(-17.77, -8.27) * mm, "end": v(-17.58, -8.29) * mm});
            skArc(sketch, "E1100", {"start": v(-17.58, -8.29) * mm, "mid": v(-17.18, -8.3) * mm, "end": v(-16.79, -8.25) * mm});
            skArc(sketch, "E1101", {"start": v(-16.79, -8.25) * mm, "mid": v(-16.02, -8.11) * mm, "end": v(-15.26, -7.96) * mm});
            skArc(sketch, "E1102", {"start": v(-15.26, -7.96) * mm, "mid": v(-14.36, -7.77) * mm, "end": v(-13.47, -7.56) * mm});
            skArc(sketch, "E1103", {"start": v(-13.47, -7.56) * mm, "mid": v(-12.53, -7.32) * mm, "end": v(-11.6, -7.06) * mm});
            skLineSegment(sketch, "E1104", {"start": v(-11.6, -7.06) * mm, "end": v(-10.25, -6.67) * mm});
            skLineSegment(sketch, "E1105", {"start": v(-10.25, -6.67) * mm, "end": v(-9.82, -7.13) * mm});
            skArc(sketch, "E1106", {"start": v(-9.82, -7.13) * mm, "mid": v(-9.64, -7.31) * mm, "end": v(-9.45, -7.48) * mm});
            skArc(sketch, "E1107", {"start": v(-9.45, -7.48) * mm, "mid": v(-9.27, -7.61) * mm, "end": v(-9.07, -7.73) * mm});
            skArc(sketch, "E1108", {"start": v(-9.07, -7.73) * mm, "mid": v(-8.87, -7.83) * mm, "end": v(-8.65, -7.9) * mm});
            skArc(sketch, "E1109", {"start": v(-8.65, -7.9) * mm, "mid": v(-8.4, -7.97) * mm, "end": v(-8.14, -8.03) * mm});
            skArc(sketch, "E1110", {"start": v(-8.14, -8.03) * mm, "mid": v(-7.76, -8.07) * mm, "end": v(-7.38, -8.09) * mm});
            skArc(sketch, "E1111", {"start": v(-7.38, -8.09) * mm, "mid": v(-6.28, -8.08) * mm, "end": v(-5.19, -8.07) * mm});
            skArc(sketch, "E1112", {"start": v(-5.19, -8.07) * mm, "mid": v(-4.08, -8.05) * mm, "end": v(-2.97, -8.03) * mm});
            skArc(sketch, "E1113", {"start": v(-2.97, -8.03) * mm, "mid": v(-2.65, -8) * mm, "end": v(-2.32, -7.95) * mm});
            skArc(sketch, "E1114", {"start": v(-2.32, -7.95) * mm, "mid": v(-2.09, -7.86) * mm, "end": v(-1.88, -7.74) * mm});
            skArc(sketch, "E1115", {"start": v(-1.88, -7.74) * mm, "mid": v(-1.64, -7.53) * mm, "end": v(-1.42, -7.3) * mm});
            skArc(sketch, "E1116", {"start": v(-1.42, -7.3) * mm, "mid": v(-1.2, -7.04) * mm, "end": v(-1.02, -6.75) * mm});
            skArc(sketch, "E1117", {"start": v(-1.02, -6.75) * mm, "mid": v(-0.87, -6.45) * mm, "end": v(-0.76, -6.13) * mm});
            skArc(sketch, "E1118", {"start": v(-0.76, -6.13) * mm, "mid": v(-0.73, -6.05) * mm, "end": v(-0.71, -5.97) * mm});
            skArc(sketch, "E1119", {"start": v(-0.71, -5.97) * mm, "mid": v(-0.67, -5.76) * mm, "end": v(-0.63, -5.54) * mm});
            skArc(sketch, "E1120", {"start": v(-0.63, -5.54) * mm, "mid": v(-0.58, -5.29) * mm, "end": v(-0.54, -5.03) * mm});
            skArc(sketch, "E1121", {"start": v(-0.54, -5.03) * mm, "mid": v(-0.49, -4.75) * mm, "end": v(-0.44, -4.47) * mm});
            skArc(sketch, "E1122", {"start": v(-0.44, -4.47) * mm, "mid": v(-0.34, -3.9) * mm, "end": v(-0.23, -3.33) * mm});
            skArc(sketch, "E1123", {"start": v(-0.23, -3.33) * mm, "mid": v(-0.15, -3.02) * mm, "end": v(-0.04, -2.71) * mm});
            skArc(sketch, "E1124", {"start": v(-0.04, -2.71) * mm, "mid": v(0.07, -2.51) * mm, "end": v(0.2, -2.33) * mm});
            skArc(sketch, "E1125", {"start": v(0.2, -2.33) * mm, "mid": v(0.36, -2.19) * mm, "end": v(0.55, -2.07) * mm});
            skArc(sketch, "E1126", {"start": v(0.55, -2.07) * mm, "mid": v(0.68, -2.01) * mm, "end": v(0.82, -1.97) * mm});
            skArc(sketch, "E1127", {"start": v(0.82, -1.97) * mm, "mid": v(0.96, -1.94) * mm, "end": v(1.1, -1.92) * mm});
            skArc(sketch, "E1128", {"start": v(1.1, -1.92) * mm, "mid": v(1.33, -1.9) * mm, "end": v(1.56, -1.9) * mm});
            skArc(sketch, "E1129", {"start": v(1.56, -1.9) * mm, "mid": v(2.2, -1.9) * mm, "end": v(2.83, -1.9) * mm});
            skArc(sketch, "E1130", {"start": v(2.83, -1.9) * mm, "mid": v(3.52, -1.9) * mm, "end": v(4.21, -1.9) * mm});
            skArc(sketch, "E1131", {"start": v(4.21, -1.9) * mm, "mid": v(4.54, -1.92) * mm, "end": v(4.86, -1.96) * mm});
            skArc(sketch, "E1132", {"start": v(4.86, -1.96) * mm, "mid": v(5.04, -2) * mm, "end": v(5.22, -2.06) * mm});
            skArc(sketch, "E1133", {"start": v(5.22, -2.06) * mm, "mid": v(5.33, -2.14) * mm, "end": v(5.4, -2.26) * mm});
            skArc(sketch, "E1134", {"start": v(5.4, -2.26) * mm, "mid": v(5.47, -2.4) * mm, "end": v(5.51, -2.56) * mm});
            skArc(sketch, "E1135", {"start": v(5.51, -2.56) * mm, "mid": v(5.58, -2.83) * mm, "end": v(5.64, -3.11) * mm});
            skArc(sketch, "E1136", {"start": v(5.64, -3.11) * mm, "mid": v(5.71, -3.45) * mm, "end": v(5.78, -3.8) * mm});
            skArc(sketch, "E1137", {"start": v(5.78, -3.8) * mm, "mid": v(5.84, -4.17) * mm, "end": v(5.9, -4.56) * mm});
            skArc(sketch, "E1138", {"start": v(5.9, -4.56) * mm, "mid": v(6.02, -5.26) * mm, "end": v(6.15, -5.96) * mm});
            skArc(sketch, "E1139", {"start": v(6.15, -5.96) * mm, "mid": v(6.25, -6.38) * mm, "end": v(6.4, -6.8) * mm});
            skArc(sketch, "E1140", {"start": v(6.4, -6.8) * mm, "mid": v(6.54, -7.07) * mm, "end": v(6.73, -7.32) * mm});
            skArc(sketch, "E1141", {"start": v(6.73, -7.32) * mm, "mid": v(6.94, -7.52) * mm, "end": v(7.19, -7.68) * mm});
            skArc(sketch, "E1142", {"start": v(7.19, -7.68) * mm, "mid": v(7.43, -7.79) * mm, "end": v(7.68, -7.86) * mm});
            skArc(sketch, "E1143", {"start": v(7.68, -7.86) * mm, "mid": v(8.01, -7.93) * mm, "end": v(8.34, -7.97) * mm});
            skArc(sketch, "E1144", {"start": v(8.34, -7.97) * mm, "mid": v(8.84, -8) * mm, "end": v(9.35, -8.03) * mm});
            skArc(sketch, "E1145", {"start": v(9.35, -8.03) * mm, "mid": v(10.25, -8.05) * mm, "end": v(11.16, -8.07) * mm});
            skArc(sketch, "E1146", {"start": v(11.16, -8.07) * mm, "mid": v(12, -8.08) * mm, "end": v(12.84, -8.09) * mm});
            skArc(sketch, "E1147", {"start": v(12.84, -8.09) * mm, "mid": v(13.16, -8.09) * mm, "end": v(13.48, -8.08) * mm});
            skArc(sketch, "E1148", {"start": v(13.48, -8.08) * mm, "mid": v(13.67, -8.07) * mm, "end": v(13.86, -8.04) * mm});
            skArc(sketch, "E1149", {"start": v(13.86, -8.04) * mm, "mid": v(14.02, -8) * mm, "end": v(14.18, -7.96) * mm});
            skArc(sketch, "E1150", {"start": v(14.18, -7.96) * mm, "mid": v(14.43, -7.83) * mm, "end": v(14.67, -7.67) * mm});
            skArc(sketch, "E1151", {"start": v(14.67, -7.67) * mm, "mid": v(14.89, -7.47) * mm, "end": v(15.07, -7.24) * mm});
            skArc(sketch, "E1152", {"start": v(15.07, -7.24) * mm, "mid": v(15.22, -6.98) * mm, "end": v(15.33, -6.7) * mm});
            skArc(sketch, "E1153", {"start": v(15.33, -6.7) * mm, "mid": v(15.4, -6.42) * mm, "end": v(15.43, -6.14) * mm});
            skArc(sketch, "E1154", {"start": v(15.43, -6.14) * mm, "mid": v(15.4, -5.47) * mm, "end": v(15.3, -4.8) * mm});
            skArc(sketch, "E1155", {"start": v(15.3, -4.8) * mm, "mid": v(14.4, -0.03) * mm, "end": v(13.5, 4.74) * mm});
            skArc(sketch, "E1156", {"start": v(13.5, 4.74) * mm, "mid": v(12.65, 9.16) * mm, "end": v(11.79, 13.57) * mm});
            skArc(sketch, "E1157", {"start": v(11.79, 13.57) * mm, "mid": v(11.35, 15.69) * mm, "end": v(10.87, 17.8) * mm});
            skArc(sketch, "E1158", {"start": v(10.87, 17.8) * mm, "mid": v(10.74, 18.21) * mm, "end": v(10.56, 18.6) * mm});
            skArc(sketch, "E1159", {"start": v(10.56, 18.6) * mm, "mid": v(10.35, 18.89) * mm, "end": v(10.08, 19.1) * mm});
            skArc(sketch, "E1160", {"start": v(10.08, 19.1) * mm, "mid": v(9.7, 19.28) * mm, "end": v(9.3, 19.39) * mm});
            skArc(sketch, "E1161", {"start": v(9.3, 19.39) * mm, "mid": v(8.62, 19.49) * mm, "end": v(7.93, 19.56) * mm});
            skArc(sketch, "E1162", {"start": v(7.93, 19.56) * mm, "mid": v(7.23, 19.6) * mm, "end": v(6.52, 19.61) * mm});
            skArc(sketch, "E1163", {"start": v(6.52, 19.61) * mm, "mid": v(4.55, 19.62) * mm, "end": v(2.58, 19.63) * mm});
            skArc(sketch, "E1164", {"start": v(2.58, 19.63) * mm, "mid": v(0.6, 19.62) * mm, "end": v(-1.38, 19.62) * mm});
            skArc(sketch, "E1165", {"start": v(-1.38, 19.62) * mm, "mid": v(-2.03, 19.6) * mm, "end": v(-2.67, 19.56) * mm});
            skArc(sketch, "E1166", {"start": v(-2.67, 19.56) * mm, "mid": v(-3.16, 19.51) * mm, "end": v(-3.66, 19.44) * mm});
            skArc(sketch, "E1167", {"start": v(-3.66, 19.44) * mm, "mid": v(-3.97, 19.36) * mm, "end": v(-4.28, 19.25) * mm});
            skArc(sketch, "E1168", {"start": v(-4.28, 19.25) * mm, "mid": v(-4.51, 19.12) * mm, "end": v(-4.71, 18.94) * mm});
            skArc(sketch, "E1169", {"start": v(-4.71, 18.94) * mm, "mid": v(-4.9, 18.72) * mm, "end": v(-5.06, 18.47) * mm});
            skArc(sketch, "E1170", {"start": v(-5.06, 18.47) * mm, "mid": v(-5.24, 18.08) * mm, "end": v(-5.37, 17.68) * mm});
            skArc(sketch, "E1171", {"start": v(-5.37, 17.68) * mm, "mid": v(-5.62, 16.63) * mm, "end": v(-5.86, 15.59) * mm});
            skArc(sketch, "E1172", {"start": v(-5.86, 15.59) * mm, "mid": v(-6.19, 14.1) * mm, "end": v(-6.5, 12.6) * mm});
            skArc(sketch, "E1173", {"start": v(-6.5, 12.6) * mm, "mid": v(-6.93, 10.41) * mm, "end": v(-7.36, 8.22) * mm});
            skArc(sketch, "E1174", {"start": v(-7.36, 8.22) * mm, "mid": v(-7.93, 5.24) * mm, "end": v(-8.51, 2.27) * mm});
            skArc(sketch, "E1175", {"start": v(-8.51, 2.27) * mm, "mid": v(-8.9, 0.36) * mm, "end": v(-9.28, -1.55) * mm});
            skArc(sketch, "E1176", {"start": v(-9.28, -1.55) * mm, "mid": v(-9.58, -2.97) * mm, "end": v(-9.87, -4.39) * mm});
            skArc(sketch, "E1177", {"start": v(-9.87, -4.39) * mm, "mid": v(-9.92, -4.53) * mm, "end": v(-10.01, -4.65) * mm});
            skArc(sketch, "E1178", {"start": v(-10.01, -4.65) * mm, "mid": v(-10.08, -4.7) * mm, "end": v(-10.17, -4.72) * mm});
            skArc(sketch, "E1179", {"start": v(-10.17, -4.72) * mm, "mid": v(-10.26, -4.7) * mm, "end": v(-10.34, -4.66) * mm});
            skArc(sketch, "E1180", {"start": v(-10.34, -4.66) * mm, "mid": v(-10.46, -4.57) * mm, "end": v(-10.55, -4.46) * mm});
            skArc(sketch, "E1181", {"start": v(-10.55, -4.46) * mm, "mid": v(-10.7, -4.25) * mm, "end": v(-10.84, -4.05) * mm});
            skArc(sketch, "E1182", {"start": v(-10.84, -4.05) * mm, "mid": v(-11.5, -3) * mm, "end": v(-12.14, -1.93) * mm});
            skArc(sketch, "E1183", {"start": v(-12.14, -1.93) * mm, "mid": v(-13.03, -0.43) * mm, "end": v(-13.91, 1.07) * mm});
            skArc(sketch, "E1184", {"start": v(-13.91, 1.07) * mm, "mid": v(-14.8, 2.6) * mm, "end": v(-15.67, 4.13) * mm});
            skArc(sketch, "E1185", {"start": v(-15.67, 4.13) * mm, "mid": v(-15.9, 4.56) * mm, "end": v(-16.08, 5) * mm});
            skArc(sketch, "E1186", {"start": v(-16.08, 5) * mm, "mid": v(-16.14, 5.2) * mm, "end": v(-16.2, 5.39) * mm});
            skArc(sketch, "E1187", {"start": v(-16.2, 5.39) * mm, "mid": v(-16.21, 5.57) * mm, "end": v(-16.22, 5.76) * mm});
            skArc(sketch, "E1188", {"start": v(-16.22, 5.76) * mm, "mid": v(-16.2, 5.95) * mm, "end": v(-16.17, 6.14) * mm});
            skArc(sketch, "E1189", {"start": v(-16.17, 6.14) * mm, "mid": v(-16.12, 6.34) * mm, "end": v(-16.05, 6.54) * mm});
            skArc(sketch, "E1190", {"start": v(-16.05, 6.54) * mm, "mid": v(-15.9, 6.87) * mm, "end": v(-15.74, 7.2) * mm});
            skArc(sketch, "E1191", {"start": v(-15.74, 7.2) * mm, "mid": v(-15.33, 8) * mm, "end": v(-14.91, 8.8) * mm});
            skArc(sketch, "E1192", {"start": v(-14.91, 8.8) * mm, "mid": v(-14.44, 9.69) * mm, "end": v(-13.97, 10.58) * mm});
            skArc(sketch, "E1193", {"start": v(-13.97, 10.58) * mm, "mid": v(-13.5, 11.43) * mm, "end": v(-13.03, 12.28) * mm});
            skArc(sketch, "E1194", {"start": v(-13.03, 12.28) * mm, "mid": v(-12.62, 13.02) * mm, "end": v(-12.22, 13.77) * mm});
            skArc(sketch, "E1195", {"start": v(-12.22, 13.77) * mm, "mid": v(-11.86, 14.45) * mm, "end": v(-11.5, 15.13) * mm});
            skArc(sketch, "E1196", {"start": v(-11.5, 15.13) * mm, "mid": v(-11.22, 15.7) * mm, "end": v(-10.95, 16.27) * mm});
            skArc(sketch, "E1197", {"start": v(-10.95, 16.27) * mm, "mid": v(-10.8, 16.58) * mm, "end": v(-10.69, 16.9) * mm});
            skArc(sketch, "E1198", {"start": v(-10.69, 16.9) * mm, "mid": v(-10.62, 17.12) * mm, "end": v(-10.57, 17.35) * mm});
            skArc(sketch, "E1199", {"start": v(-10.57, 17.35) * mm, "mid": v(-10.54, 17.58) * mm, "end": v(-10.52, 17.8) * mm});
            skArc(sketch, "E1200", {"start": v(-10.52, 17.8) * mm, "mid": v(-10.53, 18.01) * mm, "end": v(-10.56, 18.22) * mm});
            skArc(sketch, "E1201", {"start": v(-10.56, 18.22) * mm, "mid": v(-10.6, 18.4) * mm, "end": v(-10.67, 18.56) * mm});
            skArc(sketch, "E1202", {"start": v(-10.67, 18.56) * mm, "mid": v(-10.84, 18.8) * mm, "end": v(-11.07, 18.96) * mm});
            skArc(sketch, "E1203", {"start": v(-11.07, 18.96) * mm, "mid": v(-11.44, 19.13) * mm, "end": v(-11.82, 19.26) * mm});
            skArc(sketch, "E1204", {"start": v(-11.82, 19.26) * mm, "mid": v(-12.45, 19.4) * mm, "end": v(-13.09, 19.5) * mm});
            skArc(sketch, "E1205", {"start": v(-13.09, 19.5) * mm, "mid": v(-14.27, 19.66) * mm, "end": v(-15.44, 19.8) * mm});
            skArc(sketch, "E1206", {"start": v(-15.44, 19.8) * mm, "mid": v(-16.1, 19.87) * mm, "end": v(-16.75, 19.93) * mm});
            skArc(sketch, "E1207", {"start": v(-16.75, 19.93) * mm, "mid": v(-17.27, 19.96) * mm, "end": v(-17.8, 19.97) * mm});
            skArc(sketch, "E1208", {"start": v(-17.8, 19.97) * mm, "mid": v(-18.2, 19.97) * mm, "end": v(-18.61, 19.95) * mm});
            skArc(sketch, "E1209", {"start": v(-18.61, 19.95) * mm, "mid": v(-18.87, 19.92) * mm, "end": v(-19.13, 19.85) * mm});
            skArc(sketch, "E1210", {"start": v(-36.04, 16.78) * mm, "mid": v(-35.7, 16.32) * mm, "end": v(-35.4, 15.84) * mm});
            skArc(sketch, "E1211", {"start": v(-35.4, 15.84) * mm, "mid": v(-34.6, 14.47) * mm, "end": v(-33.82, 13.09) * mm});
            skArc(sketch, "E1212", {"start": v(-33.82, 13.09) * mm, "mid": v(-33.02, 11.69) * mm, "end": v(-32.24, 10.28) * mm});
            skArc(sketch, "E1213", {"start": v(-32.24, 10.28) * mm, "mid": v(-31.69, 9.26) * mm, "end": v(-31.16, 8.22) * mm});
            skArc(sketch, "E1214", {"start": v(-31.16, 8.22) * mm, "mid": v(-30.84, 7.58) * mm, "end": v(-30.53, 6.92) * mm});
            skArc(sketch, "E1215", {"start": v(-30.53, 6.92) * mm, "mid": v(-30.4, 6.56) * mm, "end": v(-30.3, 6.2) * mm});
            skArc(sketch, "E1216", {"start": v(-30.3, 6.2) * mm, "mid": v(-30.28, 5.9) * mm, "end": v(-30.31, 5.6) * mm});
            skArc(sketch, "E1217", {"start": v(-30.31, 5.6) * mm, "mid": v(-30.4, 5.24) * mm, "end": v(-30.53, 4.89) * mm});
            skArc(sketch, "E1218", {"start": v(-30.53, 4.89) * mm, "mid": v(-30.85, 4.2) * mm, "end": v(-31.2, 3.52) * mm});
            skArc(sketch, "E1219", {"start": v(-31.2, 3.52) * mm, "mid": v(-31.87, 2.3) * mm, "end": v(-32.56, 1.08) * mm});
            skArc(sketch, "E1220", {"start": v(-32.56, 1.08) * mm, "mid": v(-33.28, -0.17) * mm, "end": v(-34, -1.4) * mm});
            skArc(sketch, "E1221", {"start": v(-34, -1.4) * mm, "mid": v(-34.57, -2.32) * mm, "end": v(-35.15, -3.22) * mm});
            skArc(sketch, "E1222", {"start": v(-35.15, -3.22) * mm, "mid": v(-35.37, -3.54) * mm, "end": v(-35.61, -3.84) * mm});
            skArc(sketch, "E1223", {"start": v(-35.61, -3.84) * mm, "mid": v(-35.74, -3.9) * mm, "end": v(-35.88, -3.88) * mm});
            skArc(sketch, "E1224", {"start": v(-35.88, -3.88) * mm, "mid": v(-36, -3.75) * mm, "end": v(-36.07, -3.58) * mm});
            skArc(sketch, "E1225", {"start": v(-36.07, -3.58) * mm, "mid": v(-36.12, -3.09) * mm, "end": v(-36.16, -2.59) * mm});
            skArc(sketch, "E1226", {"start": v(-36.16, -2.59) * mm, "mid": v(-36.22, -1.98) * mm, "end": v(-36.32, -1.38) * mm});
            skArc(sketch, "E1227", {"start": v(-36.32, -1.38) * mm, "mid": v(-36.44, -0.95) * mm, "end": v(-36.63, -0.55) * mm});
            skArc(sketch, "E1228", {"start": v(-36.63, -0.55) * mm, "mid": v(-36.84, -0.25) * mm, "end": v(-37.12, 0) * mm});
            skArc(sketch, "E1229", {"start": v(-37.12, 0) * mm, "mid": v(-37.47, 0.21) * mm, "end": v(-37.84, 0.36) * mm});
            skArc(sketch, "E1230", {"start": v(-37.84, 0.36) * mm, "mid": v(-38.04, 0.41) * mm, "end": v(-38.23, 0.43) * mm});
            skArc(sketch, "E1231", {"start": v(-38.23, 0.43) * mm, "mid": v(-38.62, 0.45) * mm, "end": v(-39, 0.46) * mm});
            skArc(sketch, "E1232", {"start": v(-39, 0.46) * mm, "mid": v(-39.7, 0.47) * mm, "end": v(-40.37, 0.47) * mm});
            skArc(sketch, "E1233", {"start": v(-40.37, 0.47) * mm, "mid": v(-41.99, 0.47) * mm, "end": v(-43.6, 0.46) * mm});
            skArc(sketch, "E1234", {"start": v(-43.6, 0.46) * mm, "mid": v(-44.63, 0.46) * mm, "end": v(-45.67, 0.45) * mm});
            skArc(sketch, "E1235", {"start": v(-45.67, 0.45) * mm, "mid": v(-46.57, 0.45) * mm, "end": v(-47.47, 0.46) * mm});
            skArc(sketch, "E1236", {"start": v(-47.47, 0.46) * mm, "mid": v(-48.25, 0.46) * mm, "end": v(-49.03, 0.46) * mm});
            skArc(sketch, "E1237", {"start": v(-49.03, 0.46) * mm, "mid": v(-49.14, 0.47) * mm, "end": v(-49.24, 0.48) * mm});
            skArc(sketch, "E1238", {"start": v(-49.24, 0.48) * mm, "mid": v(-49.32, 0.5) * mm, "end": v(-49.4, 0.52) * mm});
            skArc(sketch, "E1239", {"start": v(-49.4, 0.52) * mm, "mid": v(-49.45, 0.54) * mm, "end": v(-49.5, 0.56) * mm});
            skArc(sketch, "E1240", {"start": v(-49.5, 0.56) * mm, "mid": v(-49.52, 0.6) * mm, "end": v(-49.55, 0.64) * mm});
            skArc(sketch, "E1241", {"start": v(-49.55, 0.64) * mm, "mid": v(-49.58, 0.7) * mm, "end": v(-49.6, 0.76) * mm});
            skArc(sketch, "E1242", {"start": v(-49.6, 0.76) * mm, "mid": v(-49.63, 0.88) * mm, "end": v(-49.65, 1) * mm});
            skArc(sketch, "E1243", {"start": v(-49.65, 1) * mm, "mid": v(-49.64, 1.1) * mm, "end": v(-49.6, 1.19) * mm});
            skArc(sketch, "E1244", {"start": v(-49.6, 1.19) * mm, "mid": v(-49.55, 1.27) * mm, "end": v(-49.48, 1.33) * mm});
            skArc(sketch, "E1245", {"start": v(-49.48, 1.33) * mm, "mid": v(-49.38, 1.39) * mm, "end": v(-49.28, 1.43) * mm});
            skArc(sketch, "E1246", {"start": v(-49.28, 1.43) * mm, "mid": v(-49.16, 1.46) * mm, "end": v(-49.04, 1.47) * mm});
            skArc(sketch, "E1247", {"start": v(-49.04, 1.47) * mm, "mid": v(-48.57, 1.49) * mm, "end": v(-48.1, 1.5) * mm});
            skArc(sketch, "E1248", {"start": v(-48.1, 1.5) * mm, "mid": v(-47.47, 1.52) * mm, "end": v(-46.85, 1.54) * mm});
            skArc(sketch, "E1249", {"start": v(-46.85, 1.54) * mm, "mid": v(-45.99, 1.55) * mm, "end": v(-45.12, 1.57) * mm});
            skArc(sketch, "E1250", {"start": v(-45.12, 1.57) * mm, "mid": v(-44.24, 1.58) * mm, "end": v(-43.36, 1.6) * mm});
            skArc(sketch, "E1251", {"start": v(-43.36, 1.6) * mm, "mid": v(-42.72, 1.61) * mm, "end": v(-42.1, 1.63) * mm});
            skArc(sketch, "E1252", {"start": v(-42.1, 1.63) * mm, "mid": v(-41.64, 1.65) * mm, "end": v(-41.18, 1.67) * mm});
            skArc(sketch, "E1253", {"start": v(-41.18, 1.67) * mm, "mid": v(-41.02, 1.68) * mm, "end": v(-40.86, 1.71) * mm});
            skArc(sketch, "E1254", {"start": v(-40.86, 1.71) * mm, "mid": v(-40.75, 1.74) * mm, "end": v(-40.64, 1.78) * mm});
            skArc(sketch, "E1255", {"start": v(-40.64, 1.78) * mm, "mid": v(-40.55, 1.81) * mm, "end": v(-40.47, 1.86) * mm});
            skArc(sketch, "E1256", {"start": v(-40.47, 1.86) * mm, "mid": v(-40.37, 1.92) * mm, "end": v(-40.3, 2) * mm});
            skArc(sketch, "E1257", {"start": v(-40.3, 2) * mm, "mid": v(-40.17, 2.1) * mm, "end": v(-40.05, 2.23) * mm});
            skArc(sketch, "E1258", {"start": v(-40.05, 2.23) * mm, "mid": v(-39.94, 2.34) * mm, "end": v(-39.83, 2.45) * mm});
            skArc(sketch, "E1259", {"start": v(-39.83, 2.45) * mm, "mid": v(-39.76, 2.54) * mm, "end": v(-39.7, 2.63) * mm});
            skArc(sketch, "E1260", {"start": v(-39.7, 2.63) * mm, "mid": v(-39.64, 2.71) * mm, "end": v(-39.6, 2.8) * mm});
            skArc(sketch, "E1261", {"start": v(-39.6, 2.8) * mm, "mid": v(-39.57, 2.88) * mm, "end": v(-39.54, 2.97) * mm});
            skArc(sketch, "E1262", {"start": v(-39.54, 2.97) * mm, "mid": v(-39.5, 3.24) * mm, "end": v(-39.46, 3.51) * mm});
            skArc(sketch, "E1263", {"start": v(-39.46, 3.51) * mm, "mid": v(-39.44, 4.13) * mm, "end": v(-39.42, 4.76) * mm});
            skArc(sketch, "E1264", {"start": v(-39.42, 4.76) * mm, "mid": v(-39.41, 5.41) * mm, "end": v(-39.4, 6.07) * mm});
            skArc(sketch, "E1265", {"start": v(-39.4, 6.07) * mm, "mid": v(-39.42, 6.6) * mm, "end": v(-39.44, 7.15) * mm});
            skArc(sketch, "E1266", {"start": v(-39.44, 7.15) * mm, "mid": v(-39.47, 7.57) * mm, "end": v(-39.51, 8) * mm});
            skArc(sketch, "E1267", {"start": v(-39.51, 8) * mm, "mid": v(-39.55, 8.24) * mm, "end": v(-39.61, 8.47) * mm});
            skArc(sketch, "E1268", {"start": v(-39.61, 8.47) * mm, "mid": v(-39.7, 8.66) * mm, "end": v(-39.8, 8.84) * mm});
            skArc(sketch, "E1269", {"start": v(-39.8, 8.84) * mm, "mid": v(-40, 9.08) * mm, "end": v(-40.19, 9.31) * mm});
            skLineSegment(sketch, "E1270", {"start": v(-40.19, 9.31) * mm, "end": v(-40.57, 9.74) * mm});
            skLineSegment(sketch, "E1271", {"start": v(-40.57, 9.74) * mm, "end": v(-44.4, 9.78) * mm});
            skArc(sketch, "E1272", {"start": v(-44.4, 9.78) * mm, "mid": v(-45.82, 9.8) * mm, "end": v(-47.24, 9.82) * mm});
            skArc(sketch, "E1273", {"start": v(-47.24, 9.82) * mm, "mid": v(-47.89, 9.84) * mm, "end": v(-48.53, 9.88) * mm});
            skArc(sketch, "E1274", {"start": v(-48.53, 9.88) * mm, "mid": v(-48.9, 9.9) * mm, "end": v(-49.27, 9.95) * mm});
            skArc(sketch, "E1275", {"start": v(-49.27, 9.95) * mm, "mid": v(-49.43, 10) * mm, "end": v(-49.55, 10.1) * mm});
            skArc(sketch, "E1276", {"start": v(-49.55, 10.1) * mm, "mid": v(-49.6, 10.2) * mm, "end": v(-49.64, 10.3) * mm});
            skArc(sketch, "E1277", {"start": v(-49.64, 10.3) * mm, "mid": v(-49.67, 10.4) * mm, "end": v(-49.67, 10.5) * mm});
            skArc(sketch, "E1278", {"start": v(-49.67, 10.5) * mm, "mid": v(-49.66, 10.62) * mm, "end": v(-49.63, 10.73) * mm});
            skArc(sketch, "E1279", {"start": v(-49.63, 10.73) * mm, "mid": v(-49.58, 10.83) * mm, "end": v(-49.52, 10.91) * mm});
            skArc(sketch, "E1280", {"start": v(-49.52, 10.91) * mm, "mid": v(-49.46, 10.97) * mm, "end": v(-49.4, 11.02) * mm});
            skArc(sketch, "E1281", {"start": v(-49.4, 11.02) * mm, "mid": v(-49.34, 11.05) * mm, "end": v(-49.28, 11.08) * mm});
            skArc(sketch, "E1282", {"start": v(-49.28, 11.08) * mm, "mid": v(-49.18, 11.1) * mm, "end": v(-49.09, 11.1) * mm});
            skArc(sketch, "E1283", {"start": v(-49.09, 11.1) * mm, "mid": v(-48.89, 11.13) * mm, "end": v(-48.69, 11.14) * mm});
            skArc(sketch, "E1284", {"start": v(-48.69, 11.14) * mm, "mid": v(-48.47, 11.15) * mm, "end": v(-48.25, 11.15) * mm});
            skArc(sketch, "E1285", {"start": v(-48.25, 11.15) * mm, "mid": v(-47.64, 11.15) * mm, "end": v(-47.02, 11.14) * mm});
            skArc(sketch, "E1286", {"start": v(-47.02, 11.14) * mm, "mid": v(-46.3, 11.13) * mm, "end": v(-45.57, 11.12) * mm});
            skArc(sketch, "E1287", {"start": v(-45.57, 11.12) * mm, "mid": v(-44.77, 11.11) * mm, "end": v(-43.96, 11.1) * mm});
            skArc(sketch, "E1288", {"start": v(-43.96, 11.1) * mm, "mid": v(-42.2, 11.06) * mm, "end": v(-40.42, 11.04) * mm});
            skArc(sketch, "E1289", {"start": v(-40.42, 11.04) * mm, "mid": v(-39.68, 11.05) * mm, "end": v(-38.94, 11.1) * mm});
            skArc(sketch, "E1290", {"start": v(-38.94, 11.1) * mm, "mid": v(-38.52, 11.16) * mm, "end": v(-38.1, 11.28) * mm});
            skArc(sketch, "E1291", {"start": v(-38.1, 11.28) * mm, "mid": v(-37.78, 11.43) * mm, "end": v(-37.51, 11.65) * mm});
            skArc(sketch, "E1292", {"start": v(-37.51, 11.65) * mm, "mid": v(-37.34, 11.86) * mm, "end": v(-37.2, 12.1) * mm});
            skArc(sketch, "E1293", {"start": v(-37.2, 12.1) * mm, "mid": v(-37.07, 12.38) * mm, "end": v(-36.98, 12.67) * mm});
            skArc(sketch, "E1294", {"start": v(-36.98, 12.67) * mm, "mid": v(-36.89, 13.08) * mm, "end": v(-36.82, 13.5) * mm});
            skArc(sketch, "E1295", {"start": v(-36.82, 13.5) * mm, "mid": v(-36.75, 14.14) * mm, "end": v(-36.7, 14.79) * mm});
            skArc(sketch, "E1296", {"start": v(-36.7, 14.79) * mm, "mid": v(-36.66, 15.2) * mm, "end": v(-36.62, 15.62) * mm});
            skArc(sketch, "E1297", {"start": v(-36.62, 15.62) * mm, "mid": v(-36.58, 15.96) * mm, "end": v(-36.54, 16.3) * mm});
            skArc(sketch, "E1298", {"start": v(-36.54, 16.3) * mm, "mid": v(-36.5, 16.56) * mm, "end": v(-36.46, 16.82) * mm});
            skArc(sketch, "E1299", {"start": v(-36.46, 16.82) * mm, "mid": v(-36.44, 16.9) * mm, "end": v(-36.4, 16.99) * mm});
            skArc(sketch, "E1300", {"start": v(-36.4, 16.99) * mm, "mid": v(-36.37, 17.01) * mm, "end": v(-36.34, 17.03) * mm});
            skArc(sketch, "E1301", {"start": v(-36.34, 17.03) * mm, "mid": v(-36.3, 17.03) * mm, "end": v(-36.27, 17.02) * mm});
            skArc(sketch, "E1302", {"start": v(-36.27, 17.02) * mm, "mid": v(-36.22, 16.98) * mm, "end": v(-36.18, 16.94) * mm});
            skArc(sketch, "E1303", {"start": v(-36.18, 16.94) * mm, "mid": v(-36.1, 16.86) * mm, "end": v(-36.04, 16.78) * mm});
            skArc(sketch, "E1304", {"start": v(3.17, 10.55) * mm, "mid": v(3.37, 10.29) * mm, "end": v(3.5, 9.99) * mm});
            skArc(sketch, "E1305", {"start": v(3.5, 9.99) * mm, "mid": v(3.66, 9.48) * mm, "end": v(3.77, 8.96) * mm});
            skArc(sketch, "E1306", {"start": v(3.77, 8.96) * mm, "mid": v(3.86, 8.44) * mm, "end": v(3.9, 7.9) * mm});
            skArc(sketch, "E1307", {"start": v(3.9, 7.9) * mm, "mid": v(3.9, 7.59) * mm, "end": v(3.8, 7.28) * mm});
            skArc(sketch, "E1308", {"start": v(3.8, 7.28) * mm, "mid": v(3.67, 7.1) * mm, "end": v(3.5, 7) * mm});
            skArc(sketch, "E1309", {"start": v(3.5, 7) * mm, "mid": v(3.2, 6.9) * mm, "end": v(2.88, 6.84) * mm});
            skArc(sketch, "E1310", {"start": v(2.88, 6.84) * mm, "mid": v(2.56, 6.82) * mm, "end": v(2.24, 6.84) * mm});
            skArc(sketch, "E1311", {"start": v(2.24, 6.84) * mm, "mid": v(2.02, 6.9) * mm, "end": v(1.84, 7.03) * mm});
            skArc(sketch, "E1312", {"start": v(1.84, 7.03) * mm, "mid": v(1.75, 7.17) * mm, "end": v(1.7, 7.33) * mm});
            skArc(sketch, "E1313", {"start": v(1.7, 7.33) * mm, "mid": v(1.7, 7.67) * mm, "end": v(1.7, 8) * mm});
            skArc(sketch, "E1314", {"start": v(1.7, 8) * mm, "mid": v(1.73, 8.43) * mm, "end": v(1.79, 8.85) * mm});
            skArc(sketch, "E1315", {"start": v(1.79, 8.85) * mm, "mid": v(1.86, 9.31) * mm, "end": v(1.96, 9.77) * mm});
            skArc(sketch, "E1316", {"start": v(1.96, 9.77) * mm, "mid": v(2.04, 10.06) * mm, "end": v(2.16, 10.33) * mm});
            skArc(sketch, "E1317", {"start": v(2.16, 10.33) * mm, "mid": v(2.3, 10.52) * mm, "end": v(2.47, 10.67) * mm});
            skArc(sketch, "E1318", {"start": v(2.47, 10.67) * mm, "mid": v(2.64, 10.73) * mm, "end": v(2.82, 10.73) * mm});
            skArc(sketch, "E1319", {"start": v(2.82, 10.73) * mm, "mid": v(3, 10.67) * mm, "end": v(3.17, 10.55) * mm});
            skArc(sketch, "E1320", {"start": v(18.26, 19.56) * mm, "mid": v(17.9, 19.54) * mm, "end": v(17.55, 19.5) * mm});
            skArc(sketch, "E1321", {"start": v(17.55, 19.5) * mm, "mid": v(17.27, 19.48) * mm, "end": v(17, 19.44) * mm});
            skArc(sketch, "E1322", {"start": v(17, 19.44) * mm, "mid": v(16.76, 19.4) * mm, "end": v(16.52, 19.34) * mm});
            skArc(sketch, "E1323", {"start": v(16.52, 19.34) * mm, "mid": v(16.3, 19.28) * mm, "end": v(16.09, 19.2) * mm});
            skArc(sketch, "E1324", {"start": v(16.09, 19.2) * mm, "mid": v(15.75, 19.03) * mm, "end": v(15.47, 18.78) * mm});
            skArc(sketch, "E1325", {"start": v(15.47, 18.78) * mm, "mid": v(15.24, 18.44) * mm, "end": v(15.06, 18.06) * mm});
            skArc(sketch, "E1326", {"start": v(15.06, 18.06) * mm, "mid": v(14.92, 17.53) * mm, "end": v(14.84, 16.97) * mm});
            skArc(sketch, "E1327", {"start": v(14.84, 16.97) * mm, "mid": v(14.79, 16.17) * mm, "end": v(14.77, 15.36) * mm});
            skArc(sketch, "E1328", {"start": v(14.77, 15.36) * mm, "mid": v(14.79, 14.61) * mm, "end": v(14.83, 13.87) * mm});
            skArc(sketch, "E1329", {"start": v(14.83, 13.87) * mm, "mid": v(14.9, 13.31) * mm, "end": v(15.02, 12.77) * mm});
            skArc(sketch, "E1330", {"start": v(15.02, 12.77) * mm, "mid": v(15.16, 12.38) * mm, "end": v(15.34, 12) * mm});
            skArc(sketch, "E1331", {"start": v(15.34, 12) * mm, "mid": v(15.53, 11.76) * mm, "end": v(15.8, 11.57) * mm});
            skArc(sketch, "E1332", {"start": v(15.8, 11.57) * mm, "mid": v(15.97, 11.5) * mm, "end": v(16.15, 11.45) * mm});
            skArc(sketch, "E1333", {"start": v(16.15, 11.45) * mm, "mid": v(16.48, 11.4) * mm, "end": v(16.8, 11.37) * mm});
            skArc(sketch, "E1334", {"start": v(16.8, 11.37) * mm, "mid": v(17.3, 11.33) * mm, "end": v(17.8, 11.3) * mm});
            skArc(sketch, "E1335", {"start": v(17.8, 11.3) * mm, "mid": v(18.64, 11.26) * mm, "end": v(19.49, 11.23) * mm});
            skArc(sketch, "E1336", {"start": v(19.49, 11.23) * mm, "mid": v(20.47, 11.19) * mm, "end": v(21.46, 11.14) * mm});
            skArc(sketch, "E1337", {"start": v(21.46, 11.14) * mm, "mid": v(21.95, 11.1) * mm, "end": v(22.44, 11.04) * mm});
            skArc(sketch, "E1338", {"start": v(22.44, 11.04) * mm, "mid": v(22.72, 10.97) * mm, "end": v(23, 10.88) * mm});
            skArc(sketch, "E1339", {"start": v(23, 10.88) * mm, "mid": v(23.15, 10.77) * mm, "end": v(23.26, 10.61) * mm});
            skArc(sketch, "E1340", {"start": v(23.26, 10.61) * mm, "mid": v(23.38, 10.28) * mm, "end": v(23.42, 9.92) * mm});
            skArc(sketch, "E1341", {"start": v(23.42, 9.92) * mm, "mid": v(23.44, 8.7) * mm, "end": v(23.46, 7.49) * mm});
            skArc(sketch, "E1342", {"start": v(23.46, 7.49) * mm, "mid": v(23.46, 5.63) * mm, "end": v(23.44, 3.77) * mm});
            skArc(sketch, "E1343", {"start": v(23.44, 3.77) * mm, "mid": v(23.39, 0.47) * mm, "end": v(23.33, -2.83) * mm});
            skLineSegment(sketch, "E1344", {"start": v(23.33, -2.83) * mm, "end": v(23.26, -6.63) * mm});
            skLineSegment(sketch, "E1345", {"start": v(23.26, -6.63) * mm, "end": v(23.98, -7.4) * mm});
            skLineSegment(sketch, "E1346", {"start": v(23.98, -7.4) * mm, "end": v(24.7, -8.16) * mm});
            skLineSegment(sketch, "E1347", {"start": v(24.7, -8.16) * mm, "end": v(28, -8.16) * mm});
            skLineSegment(sketch, "E1348", {"start": v(28, -8.16) * mm, "end": v(31.28, -8.16) * mm});
            skLineSegment(sketch, "E1349", {"start": v(31.28, -8.16) * mm, "end": v(32.03, -7.4) * mm});
            skLineSegment(sketch, "E1350", {"start": v(32.03, -7.4) * mm, "end": v(32.77, -6.66) * mm});
            skLineSegment(sketch, "E1351", {"start": v(32.77, -6.66) * mm, "end": v(32.67, -1.97) * mm});
            skArc(sketch, "E1352", {"start": v(32.67, -1.97) * mm, "mid": v(32.63, 0.35) * mm, "end": v(32.6, 2.66) * mm});
            skArc(sketch, "E1353", {"start": v(32.6, 2.66) * mm, "mid": v(32.57, 4.62) * mm, "end": v(32.56, 6.58) * mm});
            skArc(sketch, "E1354", {"start": v(32.56, 6.58) * mm, "mid": v(32.55, 8.24) * mm, "end": v(32.55, 9.9) * mm});
            skArc(sketch, "E1355", {"start": v(32.55, 9.9) * mm, "mid": v(32.57, 10.18) * mm, "end": v(32.63, 10.44) * mm});
            skArc(sketch, "E1356", {"start": v(32.63, 10.44) * mm, "mid": v(32.73, 10.64) * mm, "end": v(32.89, 10.78) * mm});
            skArc(sketch, "E1357", {"start": v(32.89, 10.78) * mm, "mid": v(33.13, 10.91) * mm, "end": v(33.4, 11) * mm});
            skArc(sketch, "E1358", {"start": v(33.4, 11) * mm, "mid": v(33.87, 11.07) * mm, "end": v(34.34, 11.12) * mm});
            skArc(sketch, "E1359", {"start": v(34.34, 11.12) * mm, "mid": v(35.35, 11.18) * mm, "end": v(36.36, 11.23) * mm});
            skArc(sketch, "E1360", {"start": v(36.36, 11.23) * mm, "mid": v(36.93, 11.26) * mm, "end": v(37.5, 11.29) * mm});
            skArc(sketch, "E1361", {"start": v(37.5, 11.29) * mm, "mid": v(38, 11.32) * mm, "end": v(38.5, 11.35) * mm});
            skArc(sketch, "E1362", {"start": v(38.5, 11.35) * mm, "mid": v(38.93, 11.38) * mm, "end": v(39.34, 11.42) * mm});
            skArc(sketch, "E1363", {"start": v(39.34, 11.42) * mm, "mid": v(39.63, 11.45) * mm, "end": v(39.91, 11.48) * mm});
            skArc(sketch, "E1364", {"start": v(39.91, 11.48) * mm, "mid": v(40.16, 11.55) * mm, "end": v(40.37, 11.69) * mm});
            skArc(sketch, "E1365", {"start": v(40.37, 11.69) * mm, "mid": v(40.56, 11.88) * mm, "end": v(40.7, 12.12) * mm});
            skArc(sketch, "E1366", {"start": v(40.7, 12.12) * mm, "mid": v(40.83, 12.47) * mm, "end": v(40.92, 12.84) * mm});
            skArc(sketch, "E1367", {"start": v(40.92, 12.84) * mm, "mid": v(41, 13.4) * mm, "end": v(41.05, 13.98) * mm});
            skArc(sketch, "E1368", {"start": v(41.05, 13.98) * mm, "mid": v(41.1, 14.68) * mm, "end": v(41.1, 15.39) * mm});
            skArc(sketch, "E1369", {"start": v(41.1, 15.39) * mm, "mid": v(41.1, 16.06) * mm, "end": v(41.05, 16.74) * mm});
            skArc(sketch, "E1370", {"start": v(41.05, 16.74) * mm, "mid": v(40.99, 17.31) * mm, "end": v(40.9, 17.89) * mm});
            skArc(sketch, "E1371", {"start": v(40.9, 17.89) * mm, "mid": v(40.8, 18.26) * mm, "end": v(40.66, 18.63) * mm});
            skArc(sketch, "E1372", {"start": v(40.66, 18.63) * mm, "mid": v(40.54, 18.83) * mm, "end": v(40.4, 19.03) * mm});
            skArc(sketch, "E1373", {"start": v(40.4, 19.03) * mm, "mid": v(40.26, 19.15) * mm, "end": v(40.1, 19.24) * mm});
            skArc(sketch, "E1374", {"start": v(40.1, 19.24) * mm, "mid": v(39.87, 19.31) * mm, "end": v(39.63, 19.35) * mm});
            skArc(sketch, "E1375", {"start": v(39.63, 19.35) * mm, "mid": v(39.1, 19.39) * mm, "end": v(38.59, 19.42) * mm});
            skArc(sketch, "E1376", {"start": v(38.59, 19.42) * mm, "mid": v(36.77, 19.5) * mm, "end": v(34.94, 19.53) * mm});
            skArc(sketch, "E1377", {"start": v(34.94, 19.53) * mm, "mid": v(31.5, 19.57) * mm, "end": v(28.07, 19.6) * mm});
            skArc(sketch, "E1378", {"start": v(28.07, 19.6) * mm, "mid": v(24.61, 19.62) * mm, "end": v(21.16, 19.63) * mm});
            skArc(sketch, "E1379", {"start": v(21.16, 19.63) * mm, "mid": v(19.7, 19.61) * mm, "end": v(18.26, 19.56) * mm});
            skArc(sketch, "E1380", {"start": v(70.9, 19.56) * mm, "mid": v(68.82, 19.51) * mm, "end": v(66.75, 19.46) * mm});
            skArc(sketch, "E1381", {"start": v(66.75, 19.46) * mm, "mid": v(65.13, 19.4) * mm, "end": v(63.52, 19.35) * mm});
            skArc(sketch, "E1382", {"start": v(63.52, 19.35) * mm, "mid": v(62.24, 19.3) * mm, "end": v(60.95, 19.24) * mm});
            skArc(sketch, "E1383", {"start": v(60.95, 19.24) * mm, "mid": v(60.7, 19.2) * mm, "end": v(60.45, 19.13) * mm});
            skArc(sketch, "E1384", {"start": v(60.45, 19.13) * mm, "mid": v(60.35, 19.09) * mm, "end": v(60.26, 19.03) * mm});
            skArc(sketch, "E1385", {"start": v(60.26, 19.03) * mm, "mid": v(60.16, 18.96) * mm, "end": v(60.07, 18.87) * mm});
            skArc(sketch, "E1386", {"start": v(60.07, 18.87) * mm, "mid": v(59.97, 18.78) * mm, "end": v(59.89, 18.68) * mm});
            skArc(sketch, "E1387", {"start": v(59.89, 18.68) * mm, "mid": v(59.82, 18.59) * mm, "end": v(59.76, 18.49) * mm});
            skArc(sketch, "E1388", {"start": v(59.76, 18.49) * mm, "mid": v(59.7, 18.33) * mm, "end": v(59.64, 18.17) * mm});
            skArc(sketch, "E1389", {"start": v(59.64, 18.17) * mm, "mid": v(59.59, 17.9) * mm, "end": v(59.54, 17.63) * mm});
            skArc(sketch, "E1390", {"start": v(59.54, 17.63) * mm, "mid": v(59.5, 17.3) * mm, "end": v(59.45, 16.95) * mm});
            skArc(sketch, "E1391", {"start": v(59.45, 16.95) * mm, "mid": v(59.42, 16.53) * mm, "end": v(59.39, 16.1) * mm});
            skArc(sketch, "E1392", {"start": v(59.39, 16.1) * mm, "mid": v(59.36, 15.55) * mm, "end": v(59.33, 14.98) * mm});
            skArc(sketch, "E1393", {"start": v(59.33, 14.98) * mm, "mid": v(59.3, 13.83) * mm, "end": v(59.26, 12.68) * mm});
            skArc(sketch, "E1394", {"start": v(59.26, 12.68) * mm, "mid": v(59.22, 11.52) * mm, "end": v(59.2, 10.37) * mm});
            skArc(sketch, "E1395", {"start": v(59.2, 10.37) * mm, "mid": v(59.18, 9.82) * mm, "end": v(59.18, 9.26) * mm});
            skLineSegment(sketch, "E1396", {"start": v(59.18, 9.26) * mm, "end": v(59.18, 8.83) * mm});
            skLineSegment(sketch, "E1397", {"start": v(59.18, 8.83) * mm, "end": v(52.44, 8.88) * mm});
            skArc(sketch, "E1398", {"start": v(52.44, 8.88) * mm, "mid": v(49.76, 8.9) * mm, "end": v(47.08, 8.9) * mm});
            skArc(sketch, "E1399", {"start": v(47.08, 8.9) * mm, "mid": v(45.72, 8.9) * mm, "end": v(44.36, 8.86) * mm});
            skArc(sketch, "E1400", {"start": v(44.36, 8.86) * mm, "mid": v(43.54, 8.81) * mm, "end": v(42.72, 8.74) * mm});
            skArc(sketch, "E1401", {"start": v(42.72, 8.74) * mm, "mid": v(42.29, 8.66) * mm, "end": v(41.87, 8.5) * mm});
            skArc(sketch, "E1402", {"start": v(41.87, 8.5) * mm, "mid": v(41.62, 8.32) * mm, "end": v(41.42, 8.08) * mm});
            skArc(sketch, "E1403", {"start": v(41.42, 8.08) * mm, "mid": v(41.24, 7.75) * mm, "end": v(41.12, 7.4) * mm});
            skArc(sketch, "E1404", {"start": v(41.12, 7.4) * mm, "mid": v(41, 6.9) * mm, "end": v(40.95, 6.38) * mm});
            skArc(sketch, "E1405", {"start": v(40.95, 6.38) * mm, "mid": v(40.9, 5.64) * mm, "end": v(40.9, 4.9) * mm});
            skArc(sketch, "E1406", {"start": v(40.9, 4.9) * mm, "mid": v(40.9, 4.28) * mm, "end": v(40.94, 3.68) * mm});
            skArc(sketch, "E1407", {"start": v(40.94, 3.68) * mm, "mid": v(40.98, 3.2) * mm, "end": v(41.06, 2.72) * mm});
            skArc(sketch, "E1408", {"start": v(41.06, 2.72) * mm, "mid": v(41.15, 2.36) * mm, "end": v(41.26, 2.01) * mm});
            skArc(sketch, "E1409", {"start": v(41.26, 2.01) * mm, "mid": v(41.38, 1.78) * mm, "end": v(41.54, 1.57) * mm});
            skArc(sketch, "E1410", {"start": v(41.54, 1.57) * mm, "mid": v(41.83, 1.36) * mm, "end": v(42.17, 1.24) * mm});
            skArc(sketch, "E1411", {"start": v(42.17, 1.24) * mm, "mid": v(42.77, 1.14) * mm, "end": v(43.37, 1.09) * mm});
            skArc(sketch, "E1412", {"start": v(43.37, 1.09) * mm, "mid": v(44.49, 1.04) * mm, "end": v(45.6, 1.02) * mm});
            skArc(sketch, "E1413", {"start": v(45.6, 1.02) * mm, "mid": v(48.57, 1.01) * mm, "end": v(51.53, 1) * mm});
            skLineSegment(sketch, "E1414", {"start": v(51.53, 1) * mm, "end": v(59.18, 1) * mm});
            skLineSegment(sketch, "E1415", {"start": v(59.18, 1) * mm, "end": v(59.18, 0.71) * mm});
            skArc(sketch, "E1416", {"start": v(59.18, 0.71) * mm, "mid": v(59.18, 0) * mm, "end": v(59.2, -0.73) * mm});
            skArc(sketch, "E1417", {"start": v(59.2, -0.73) * mm, "mid": v(59.27, -2.03) * mm, "end": v(59.33, -3.32) * mm});
            skArc(sketch, "E1418", {"start": v(59.33, -3.32) * mm, "mid": v(59.4, -4.65) * mm, "end": v(59.47, -5.97) * mm});
            skArc(sketch, "E1419", {"start": v(59.47, -5.97) * mm, "mid": v(59.5, -6.4) * mm, "end": v(59.56, -6.84) * mm});
            skArc(sketch, "E1420", {"start": v(59.56, -6.84) * mm, "mid": v(59.6, -6.96) * mm, "end": v(59.65, -7.07) * mm});
            skArc(sketch, "E1421", {"start": v(59.65, -7.07) * mm, "mid": v(59.74, -7.2) * mm, "end": v(59.84, -7.33) * mm});
            skArc(sketch, "E1422", {"start": v(59.84, -7.33) * mm, "mid": v(59.96, -7.45) * mm, "end": v(60.1, -7.56) * mm});
            skArc(sketch, "E1423", {"start": v(60.1, -7.56) * mm, "mid": v(60.23, -7.66) * mm, "end": v(60.37, -7.74) * mm});
            skArc(sketch, "E1424", {"start": v(60.37, -7.74) * mm, "mid": v(60.72, -7.89) * mm, "end": v(61.09, -7.97) * mm});
            skArc(sketch, "E1425", {"start": v(61.09, -7.97) * mm, "mid": v(61.78, -8.05) * mm, "end": v(62.48, -8.1) * mm});
            skArc(sketch, "E1426", {"start": v(62.48, -8.1) * mm, "mid": v(63.28, -8.14) * mm, "end": v(64.07, -8.16) * mm});
            skArc(sketch, "E1427", {"start": v(64.07, -8.16) * mm, "mid": v(64.83, -8.14) * mm, "end": v(65.6, -8.1) * mm});
            skArc(sketch, "E1428", {"start": v(65.6, -8.1) * mm, "mid": v(66.25, -8.03) * mm, "end": v(66.9, -7.94) * mm});
            skArc(sketch, "E1429", {"start": v(66.9, -7.94) * mm, "mid": v(67.27, -7.85) * mm, "end": v(67.62, -7.7) * mm});
            skArc(sketch, "E1430", {"start": v(67.62, -7.7) * mm, "mid": v(67.86, -7.51) * mm, "end": v(68.04, -7.27) * mm});
            skArc(sketch, "E1431", {"start": v(68.04, -7.27) * mm, "mid": v(68.19, -6.95) * mm, "end": v(68.28, -6.6) * mm});
            skArc(sketch, "E1432", {"start": v(68.28, -6.6) * mm, "mid": v(68.3, -6.48) * mm, "end": v(68.3, -6.36) * mm});
            skArc(sketch, "E1433", {"start": v(68.3, -6.36) * mm, "mid": v(68.32, -6) * mm, "end": v(68.34, -5.63) * mm});
            skArc(sketch, "E1434", {"start": v(68.34, -5.63) * mm, "mid": v(68.36, -5.2) * mm, "end": v(68.38, -4.77) * mm});
            skArc(sketch, "E1435", {"start": v(68.38, -4.77) * mm, "mid": v(68.4, -4.3) * mm, "end": v(68.41, -3.82) * mm});
            skArc(sketch, "E1436", {"start": v(68.41, -3.82) * mm, "mid": v(68.45, -2.65) * mm, "end": v(68.49, -1.48) * mm});
            skArc(sketch, "E1437", {"start": v(68.49, -1.48) * mm, "mid": v(68.52, -0.9) * mm, "end": v(68.56, -0.3) * mm});
            skArc(sketch, "E1438", {"start": v(68.56, -0.3) * mm, "mid": v(68.6, 0.05) * mm, "end": v(68.65, 0.4) * mm});
            skArc(sketch, "E1439", {"start": v(68.65, 0.4) * mm, "mid": v(68.7, 0.55) * mm, "end": v(68.81, 0.67) * mm});
            skArc(sketch, "E1440", {"start": v(68.81, 0.67) * mm, "mid": v(68.93, 0.74) * mm, "end": v(69.07, 0.78) * mm});
            skArc(sketch, "E1441", {"start": v(69.07, 0.78) * mm, "mid": v(69.4, 0.81) * mm, "end": v(69.75, 0.84) * mm});
            skArc(sketch, "E1442", {"start": v(69.75, 0.84) * mm, "mid": v(70.32, 0.87) * mm, "end": v(70.9, 0.88) * mm});
            skArc(sketch, "E1443", {"start": v(70.9, 0.88) * mm, "mid": v(72.09, 0.91) * mm, "end": v(73.28, 0.93) * mm});
            skArc(sketch, "E1444", {"start": v(73.28, 0.93) * mm, "mid": v(74.05, 0.95) * mm, "end": v(74.83, 0.97) * mm});
            skArc(sketch, "E1445", {"start": v(74.83, 0.97) * mm, "mid": v(75.44, 0.98) * mm, "end": v(76.05, 1) * mm});
            skArc(sketch, "E1446", {"start": v(76.05, 1) * mm, "mid": v(76.53, 1.02) * mm, "end": v(77, 1.04) * mm});
            skArc(sketch, "E1447", {"start": v(77, 1.04) * mm, "mid": v(77.15, 1.06) * mm, "end": v(77.3, 1.08) * mm});
            skArc(sketch, "E1448", {"start": v(77.3, 1.08) * mm, "mid": v(77.54, 1.16) * mm, "end": v(77.77, 1.28) * mm});
            skArc(sketch, "E1449", {"start": v(77.77, 1.28) * mm, "mid": v(77.98, 1.44) * mm, "end": v(78.15, 1.64) * mm});
            skArc(sketch, "E1450", {"start": v(78.15, 1.64) * mm, "mid": v(78.32, 1.9) * mm, "end": v(78.45, 2.18) * mm});
            skArc(sketch, "E1451", {"start": v(78.45, 2.18) * mm, "mid": v(78.58, 2.55) * mm, "end": v(78.68, 2.93) * mm});
            skArc(sketch, "E1452", {"start": v(78.68, 2.93) * mm, "mid": v(78.75, 3.32) * mm, "end": v(78.79, 3.71) * mm});
            skArc(sketch, "E1453", {"start": v(78.79, 3.71) * mm, "mid": v(78.81, 4.35) * mm, "end": v(78.82, 4.98) * mm});
            skArc(sketch, "E1454", {"start": v(78.82, 4.98) * mm, "mid": v(78.81, 5.63) * mm, "end": v(78.79, 6.27) * mm});
            skArc(sketch, "E1455", {"start": v(78.79, 6.27) * mm, "mid": v(78.75, 6.7) * mm, "end": v(78.68, 7.13) * mm});
            skArc(sketch, "E1456", {"start": v(78.68, 7.13) * mm, "mid": v(78.5, 7.74) * mm, "end": v(78.24, 8.31) * mm});
            skArc(sketch, "E1457", {"start": v(78.24, 8.31) * mm, "mid": v(77.92, 8.7) * mm, "end": v(77.5, 8.95) * mm});
            skArc(sketch, "E1458", {"start": v(77.5, 8.95) * mm, "mid": v(76.84, 9.15) * mm, "end": v(76.17, 9.23) * mm});
            skArc(sketch, "E1459", {"start": v(76.17, 9.23) * mm, "mid": v(74.8, 9.24) * mm, "end": v(73.42, 9.23) * mm});
            skArc(sketch, "E1460", {"start": v(73.42, 9.23) * mm, "mid": v(72.48, 9.2) * mm, "end": v(71.54, 9.18) * mm});
            skArc(sketch, "E1461", {"start": v(71.54, 9.18) * mm, "mid": v(70.9, 9.17) * mm, "end": v(70.25, 9.17) * mm});
            skArc(sketch, "E1462", {"start": v(70.25, 9.17) * mm, "mid": v(69.8, 9.18) * mm, "end": v(69.34, 9.2) * mm});
            skArc(sketch, "E1463", {"start": v(69.34, 9.2) * mm, "mid": v(69.18, 9.21) * mm, "end": v(69.03, 9.26) * mm});
            skArc(sketch, "E1464", {"start": v(69.03, 9.26) * mm, "mid": v(68.93, 9.3) * mm, "end": v(68.85, 9.38) * mm});
            skArc(sketch, "E1465", {"start": v(68.85, 9.38) * mm, "mid": v(68.76, 9.47) * mm, "end": v(68.7, 9.58) * mm});
            skArc(sketch, "E1466", {"start": v(68.7, 9.58) * mm, "mid": v(68.63, 9.7) * mm, "end": v(68.6, 9.83) * mm});
            skArc(sketch, "E1467", {"start": v(68.6, 9.83) * mm, "mid": v(68.56, 9.95) * mm, "end": v(68.56, 10.09) * mm});
            skArc(sketch, "E1468", {"start": v(68.56, 10.09) * mm, "mid": v(68.57, 10.22) * mm, "end": v(68.6, 10.35) * mm});
            skArc(sketch, "E1469", {"start": v(68.6, 10.35) * mm, "mid": v(68.65, 10.47) * mm, "end": v(68.73, 10.58) * mm});
            skArc(sketch, "E1470", {"start": v(68.73, 10.58) * mm, "mid": v(68.82, 10.68) * mm, "end": v(68.92, 10.76) * mm});
            skArc(sketch, "E1471", {"start": v(68.92, 10.76) * mm, "mid": v(69.04, 10.83) * mm, "end": v(69.17, 10.88) * mm});
            skArc(sketch, "E1472", {"start": v(69.17, 10.88) * mm, "mid": v(69.28, 10.9) * mm, "end": v(69.4, 10.9) * mm});
            skArc(sketch, "E1473", {"start": v(69.4, 10.9) * mm, "mid": v(70.04, 10.92) * mm, "end": v(70.68, 10.93) * mm});
            skArc(sketch, "E1474", {"start": v(70.68, 10.93) * mm, "mid": v(71.5, 10.94) * mm, "end": v(72.32, 10.94) * mm});
            skArc(sketch, "E1475", {"start": v(72.32, 10.94) * mm, "mid": v(73.41, 10.95) * mm, "end": v(74.5, 10.95) * mm});
            skArc(sketch, "E1476", {"start": v(74.5, 10.95) * mm, "mid": v(75.5, 10.95) * mm, "end": v(76.5, 10.95) * mm});
            skArc(sketch, "E1477", {"start": v(76.5, 10.95) * mm, "mid": v(77.39, 10.96) * mm, "end": v(78.27, 10.97) * mm});
            skArc(sketch, "E1478", {"start": v(78.27, 10.97) * mm, "mid": v(79.01, 10.98) * mm, "end": v(79.75, 11) * mm});
            skArc(sketch, "E1479", {"start": v(79.75, 11) * mm, "mid": v(79.96, 11) * mm, "end": v(80.17, 11.02) * mm});
            skArc(sketch, "E1480", {"start": v(80.17, 11.02) * mm, "mid": v(80.56, 11.07) * mm, "end": v(80.95, 11.16) * mm});
            skArc(sketch, "E1481", {"start": v(80.95, 11.16) * mm, "mid": v(81.2, 11.24) * mm, "end": v(81.43, 11.37) * mm});
            skArc(sketch, "E1482", {"start": v(81.43, 11.37) * mm, "mid": v(81.6, 11.53) * mm, "end": v(81.75, 11.72) * mm});
            skArc(sketch, "E1483", {"start": v(81.75, 11.72) * mm, "mid": v(81.88, 12) * mm, "end": v(81.97, 12.27) * mm});
            skArc(sketch, "E1484", {"start": v(81.97, 12.27) * mm, "mid": v(82.01, 12.44) * mm, "end": v(82.04, 12.61) * mm});
            skArc(sketch, "E1485", {"start": v(82.04, 12.61) * mm, "mid": v(82.06, 12.82) * mm, "end": v(82.08, 13.03) * mm});
            skArc(sketch, "E1486", {"start": v(82.08, 13.03) * mm, "mid": v(82.1, 13.35) * mm, "end": v(82.1, 13.68) * mm});
            skArc(sketch, "E1487", {"start": v(82.1, 13.68) * mm, "mid": v(82.1, 14.3) * mm, "end": v(82.1, 14.9) * mm});
            skArc(sketch, "E1488", {"start": v(82.1, 14.9) * mm, "mid": v(82.09, 16.15) * mm, "end": v(82.04, 17.39) * mm});
            skArc(sketch, "E1489", {"start": v(82.04, 17.39) * mm, "mid": v(81.96, 17.96) * mm, "end": v(81.78, 18.51) * mm});
            skArc(sketch, "E1490", {"start": v(81.78, 18.51) * mm, "mid": v(81.54, 18.87) * mm, "end": v(81.2, 19.12) * mm});
            skArc(sketch, "E1491", {"start": v(81.2, 19.12) * mm, "mid": v(80.67, 19.33) * mm, "end": v(80.1, 19.47) * mm});
            skArc(sketch, "E1492", {"start": v(80.1, 19.47) * mm, "mid": v(79.65, 19.52) * mm, "end": v(79.18, 19.55) * mm});
            skArc(sketch, "E1493", {"start": v(79.18, 19.55) * mm, "mid": v(77.91, 19.57) * mm, "end": v(76.64, 19.59) * mm});
            skArc(sketch, "E1494", {"start": v(76.64, 19.59) * mm, "mid": v(75.2, 19.6) * mm, "end": v(73.77, 19.6) * mm});
            skArc(sketch, "E1495", {"start": v(73.77, 19.6) * mm, "mid": v(72.33, 19.58) * mm, "end": v(70.9, 19.56) * mm});
            skArc(sketch, "E1496", {"start": v(37.99, -13.94) * mm, "mid": v(37.96, -14.05) * mm, "end": v(37.97, -14.17) * mm});
            skArc(sketch, "E1497", {"start": v(37.97, -14.17) * mm, "mid": v(38.02, -14.33) * mm, "end": v(38.08, -14.48) * mm});
            skArc(sketch, "E1498", {"start": v(38.08, -14.48) * mm, "mid": v(38.16, -14.6) * mm, "end": v(38.25, -14.73) * mm});
            skArc(sketch, "E1499", {"start": v(38.25, -14.73) * mm, "mid": v(38.33, -14.79) * mm, "end": v(38.43, -14.81) * mm});
            skArc(sketch, "E1500", {"start": v(38.43, -14.81) * mm, "mid": v(38.5, -14.79) * mm, "end": v(38.57, -14.73) * mm});
            skArc(sketch, "E1501", {"start": v(38.57, -14.73) * mm, "mid": v(38.6, -14.62) * mm, "end": v(38.6, -14.52) * mm});
            skArc(sketch, "E1502", {"start": v(38.6, -14.52) * mm, "mid": v(38.59, -14.37) * mm, "end": v(38.54, -14.24) * mm});
            skArc(sketch, "E1503", {"start": v(38.54, -14.24) * mm, "mid": v(38.47, -14.11) * mm, "end": v(38.37, -14) * mm});
            skArc(sketch, "E1504", {"start": v(38.37, -14) * mm, "mid": v(38.31, -13.94) * mm, "end": v(38.25, -13.88) * mm});
            skArc(sketch, "E1505", {"start": v(38.25, -13.88) * mm, "mid": v(38.2, -13.85) * mm, "end": v(38.14, -13.84) * mm});
            skArc(sketch, "E1506", {"start": v(38.14, -13.84) * mm, "mid": v(38.1, -13.84) * mm, "end": v(38.05, -13.86) * mm});
            skArc(sketch, "E1507", {"start": v(38.05, -13.86) * mm, "mid": v(38.01, -13.9) * mm, "end": v(37.99, -13.94) * mm});
            skArc(sketch, "E1508", {"start": v(37.07, -14.12) * mm, "mid": v(37.05, -14.15) * mm, "end": v(37.04, -14.17) * mm});
            skArc(sketch, "E1509", {"start": v(37.04, -14.17) * mm, "mid": v(37.02, -14.2) * mm, "end": v(37, -14.23) * mm});
            skArc(sketch, "E1510", {"start": v(37, -14.23) * mm, "mid": v(37, -14.26) * mm, "end": v(37, -14.3) * mm});
            skArc(sketch, "E1511", {"start": v(37, -14.3) * mm, "mid": v(36.99, -14.33) * mm, "end": v(36.99, -14.36) * mm});
            skArc(sketch, "E1512", {"start": v(36.99, -14.36) * mm, "mid": v(36.96, -14.44) * mm, "end": v(36.9, -14.5) * mm});
            skArc(sketch, "E1513", {"start": v(36.9, -14.5) * mm, "mid": v(36.76, -14.54) * mm, "end": v(36.62, -14.57) * mm});
            skArc(sketch, "E1514", {"start": v(36.62, -14.57) * mm, "mid": v(36.34, -14.6) * mm, "end": v(36.06, -14.62) * mm});
            skArc(sketch, "E1515", {"start": v(36.06, -14.62) * mm, "mid": v(35.35, -14.64) * mm, "end": v(34.65, -14.67) * mm});
            skArc(sketch, "E1516", {"start": v(34.65, -14.67) * mm, "mid": v(34.05, -14.7) * mm, "end": v(33.46, -14.72) * mm});
            skArc(sketch, "E1517", {"start": v(33.46, -14.72) * mm, "mid": v(33.13, -14.74) * mm, "end": v(32.8, -14.78) * mm});
            skArc(sketch, "E1518", {"start": v(32.8, -14.78) * mm, "mid": v(32.66, -14.8) * mm, "end": v(32.53, -14.86) * mm});
            skArc(sketch, "E1519", {"start": v(32.53, -14.86) * mm, "mid": v(32.5, -14.91) * mm, "end": v(32.53, -14.96) * mm});
            skArc(sketch, "E1520", {"start": v(32.53, -14.96) * mm, "mid": v(32.65, -15.01) * mm, "end": v(32.78, -15.04) * mm});
            skArc(sketch, "E1521", {"start": v(32.78, -15.04) * mm, "mid": v(33.1, -15.07) * mm, "end": v(33.43, -15.1) * mm});
            skArc(sketch, "E1522", {"start": v(33.43, -15.1) * mm, "mid": v(33.83, -15.13) * mm, "end": v(34.24, -15.14) * mm});
            skArc(sketch, "E1523", {"start": v(34.24, -15.14) * mm, "mid": v(34.71, -15.15) * mm, "end": v(35.19, -15.16) * mm});
            skLineSegment(sketch, "E1524", {"start": v(35.19, -15.16) * mm, "end": v(36.44, -15.16) * mm});
            skLineSegment(sketch, "E1525", {"start": v(36.44, -15.16) * mm, "end": v(36.17, -15.63) * mm});
            skArc(sketch, "E1526", {"start": v(36.17, -15.63) * mm, "mid": v(35.91, -16.08) * mm, "end": v(35.62, -16.51) * mm});
            skArc(sketch, "E1527", {"start": v(35.62, -16.51) * mm, "mid": v(35.33, -16.9) * mm, "end": v(35.02, -17.26) * mm});
            skArc(sketch, "E1528", {"start": v(35.02, -17.26) * mm, "mid": v(34.67, -17.62) * mm, "end": v(34.3, -17.95) * mm});
            skArc(sketch, "E1529", {"start": v(34.3, -17.95) * mm, "mid": v(33.84, -18.31) * mm, "end": v(33.38, -18.66) * mm});
            skArc(sketch, "E1530", {"start": v(33.38, -18.66) * mm, "mid": v(33.02, -18.9) * mm, "end": v(32.67, -19.16) * mm});
            skArc(sketch, "E1531", {"start": v(32.67, -19.16) * mm, "mid": v(32.46, -19.32) * mm, "end": v(32.25, -19.48) * mm});
            skArc(sketch, "E1532", {"start": v(32.25, -19.48) * mm, "mid": v(32.12, -19.6) * mm, "end": v(32, -19.7) * mm});
            skArc(sketch, "E1533", {"start": v(32, -19.7) * mm, "mid": v(31.96, -19.76) * mm, "end": v(31.95, -19.82) * mm});
            skArc(sketch, "E1534", {"start": v(31.95, -19.82) * mm, "mid": v(32, -19.92) * mm, "end": v(32.1, -19.93) * mm});
            skArc(sketch, "E1535", {"start": v(32.1, -19.93) * mm, "mid": v(32.37, -19.83) * mm, "end": v(32.64, -19.7) * mm});
            skArc(sketch, "E1536", {"start": v(32.64, -19.7) * mm, "mid": v(33.03, -19.5) * mm, "end": v(33.4, -19.27) * mm});
            skArc(sketch, "E1537", {"start": v(33.4, -19.27) * mm, "mid": v(33.87, -18.95) * mm, "end": v(34.33, -18.63) * mm});
            skArc(sketch, "E1538", {"start": v(34.33, -18.63) * mm, "mid": v(34.62, -18.41) * mm, "end": v(34.92, -18.2) * mm});
            skArc(sketch, "E1539", {"start": v(34.92, -18.2) * mm, "mid": v(35.05, -18.11) * mm, "end": v(35.2, -18.04) * mm});
            skArc(sketch, "E1540", {"start": v(35.2, -18.04) * mm, "mid": v(35.28, -18) * mm, "end": v(35.38, -18) * mm});
            skArc(sketch, "E1541", {"start": v(35.38, -18) * mm, "mid": v(35.47, -18) * mm, "end": v(35.55, -18.03) * mm});
            skArc(sketch, "E1542", {"start": v(35.55, -18.03) * mm, "mid": v(35.6, -18.06) * mm, "end": v(35.66, -18.1) * mm});
            skArc(sketch, "E1543", {"start": v(35.66, -18.1) * mm, "mid": v(35.79, -18.22) * mm, "end": v(35.92, -18.33) * mm});
            skArc(sketch, "E1544", {"start": v(35.92, -18.33) * mm, "mid": v(36.08, -18.47) * mm, "end": v(36.23, -18.6) * mm});
            skArc(sketch, "E1545", {"start": v(36.23, -18.6) * mm, "mid": v(36.4, -18.76) * mm, "end": v(36.57, -18.92) * mm});
            skArc(sketch, "E1546", {"start": v(36.57, -18.92) * mm, "mid": v(36.9, -19.23) * mm, "end": v(37.25, -19.53) * mm});
            skArc(sketch, "E1547", {"start": v(37.25, -19.53) * mm, "mid": v(37.45, -19.7) * mm, "end": v(37.67, -19.84) * mm});
            skArc(sketch, "E1548", {"start": v(37.67, -19.84) * mm, "mid": v(37.8, -19.9) * mm, "end": v(37.93, -19.91) * mm});
            skArc(sketch, "E1549", {"start": v(37.93, -19.91) * mm, "mid": v(38.02, -19.89) * mm, "end": v(38.08, -19.81) * mm});
            skArc(sketch, "E1550", {"start": v(38.08, -19.81) * mm, "mid": v(38.1, -19.72) * mm, "end": v(38.06, -19.63) * mm});
            skArc(sketch, "E1551", {"start": v(38.06, -19.63) * mm, "mid": v(37.95, -19.47) * mm, "end": v(37.83, -19.32) * mm});
            skArc(sketch, "E1552", {"start": v(37.83, -19.32) * mm, "mid": v(37.64, -19.11) * mm, "end": v(37.43, -18.92) * mm});
            skArc(sketch, "E1553", {"start": v(37.43, -18.92) * mm, "mid": v(37.13, -18.64) * mm, "end": v(36.82, -18.37) * mm});
            skArc(sketch, "E1554", {"start": v(36.82, -18.37) * mm, "mid": v(36.64, -18.22) * mm, "end": v(36.46, -18.06) * mm});
            skArc(sketch, "E1555", {"start": v(36.46, -18.06) * mm, "mid": v(36.3, -17.93) * mm, "end": v(36.14, -17.8) * mm});
            skArc(sketch, "E1556", {"start": v(36.14, -17.8) * mm, "mid": v(36, -17.67) * mm, "end": v(35.87, -17.56) * mm});
            skArc(sketch, "E1557", {"start": v(35.87, -17.56) * mm, "mid": v(35.84, -17.53) * mm, "end": v(35.8, -17.5) * mm});
            skArc(sketch, "E1558", {"start": v(35.8, -17.5) * mm, "mid": v(35.78, -17.46) * mm, "end": v(35.77, -17.42) * mm});
            skArc(sketch, "E1559", {"start": v(35.77, -17.42) * mm, "mid": v(35.78, -17.37) * mm, "end": v(35.8, -17.31) * mm});
            skArc(sketch, "E1560", {"start": v(35.8, -17.31) * mm, "mid": v(35.84, -17.22) * mm, "end": v(35.89, -17.13) * mm});
            skArc(sketch, "E1561", {"start": v(35.89, -17.13) * mm, "mid": v(36, -16.96) * mm, "end": v(36.1, -16.8) * mm});
            skArc(sketch, "E1562", {"start": v(36.1, -16.8) * mm, "mid": v(36.19, -16.66) * mm, "end": v(36.28, -16.52) * mm});
            skArc(sketch, "E1563", {"start": v(36.28, -16.52) * mm, "mid": v(36.38, -16.36) * mm, "end": v(36.48, -16.2) * mm});
            skArc(sketch, "E1564", {"start": v(36.48, -16.2) * mm, "mid": v(36.57, -16.03) * mm, "end": v(36.67, -15.88) * mm});
            skArc(sketch, "E1565", {"start": v(36.67, -15.88) * mm, "mid": v(36.75, -15.75) * mm, "end": v(36.83, -15.62) * mm});
            skArc(sketch, "E1566", {"start": v(36.83, -15.62) * mm, "mid": v(36.92, -15.46) * mm, "end": v(37.02, -15.3) * mm});
            skArc(sketch, "E1567", {"start": v(37.02, -15.3) * mm, "mid": v(37.08, -15.22) * mm, "end": v(37.15, -15.14) * mm});
            skArc(sketch, "E1568", {"start": v(37.15, -15.14) * mm, "mid": v(37.2, -15.09) * mm, "end": v(37.27, -15.05) * mm});
            skArc(sketch, "E1569", {"start": v(37.27, -15.05) * mm, "mid": v(37.36, -15) * mm, "end": v(37.44, -14.98) * mm});
            skArc(sketch, "E1570", {"start": v(37.44, -14.98) * mm, "mid": v(37.5, -14.96) * mm, "end": v(37.55, -14.95) * mm});
            skArc(sketch, "E1571", {"start": v(37.55, -14.95) * mm, "mid": v(37.6, -14.93) * mm, "end": v(37.64, -14.9) * mm});
            skArc(sketch, "E1572", {"start": v(37.64, -14.9) * mm, "mid": v(37.67, -14.88) * mm, "end": v(37.7, -14.86) * mm});
            skArc(sketch, "E1573", {"start": v(37.7, -14.86) * mm, "mid": v(37.71, -14.84) * mm, "end": v(37.71, -14.82) * mm});
            skArc(sketch, "E1574", {"start": v(37.71, -14.82) * mm, "mid": v(37.71, -14.8) * mm, "end": v(37.7, -14.78) * mm});
            skArc(sketch, "E1575", {"start": v(37.7, -14.78) * mm, "mid": v(37.7, -14.76) * mm, "end": v(37.7, -14.73) * mm});
            skArc(sketch, "E1576", {"start": v(37.7, -14.73) * mm, "mid": v(37.7, -14.7) * mm, "end": v(37.7, -14.68) * mm});
            skArc(sketch, "E1577", {"start": v(37.7, -14.68) * mm, "mid": v(37.7, -14.66) * mm, "end": v(37.7, -14.64) * mm});
            skArc(sketch, "E1578", {"start": v(37.7, -14.64) * mm, "mid": v(37.68, -14.58) * mm, "end": v(37.65, -14.53) * mm});
            skArc(sketch, "E1579", {"start": v(37.65, -14.53) * mm, "mid": v(37.56, -14.41) * mm, "end": v(37.47, -14.3) * mm});
            skArc(sketch, "E1580", {"start": v(37.47, -14.3) * mm, "mid": v(37.38, -14.19) * mm, "end": v(37.28, -14.08) * mm});
            skArc(sketch, "E1581", {"start": v(37.28, -14.08) * mm, "mid": v(37.25, -14.05) * mm, "end": v(37.2, -14.04) * mm});
            skArc(sketch, "E1582", {"start": v(37.2, -14.04) * mm, "mid": v(37.19, -14.04) * mm, "end": v(37.18, -14.05) * mm});
            skArc(sketch, "E1583", {"start": v(37.18, -14.05) * mm, "mid": v(37.16, -14.06) * mm, "end": v(37.14, -14.07) * mm});
            skArc(sketch, "E1584", {"start": v(37.14, -14.07) * mm, "mid": v(37.12, -14.08) * mm, "end": v(37.1, -14.1) * mm});
            skArc(sketch, "E1585", {"start": v(37.1, -14.1) * mm, "mid": v(37.09, -14.1) * mm, "end": v(37.07, -14.12) * mm});
            skArc(sketch, "E1586", {"start": v(-24.85, -14.54) * mm, "mid": v(-24.87, -14.57) * mm, "end": v(-24.9, -14.61) * mm});
            skArc(sketch, "E1587", {"start": v(-24.9, -14.61) * mm, "mid": v(-24.91, -14.66) * mm, "end": v(-24.93, -14.7) * mm});
            skArc(sketch, "E1588", {"start": v(-24.93, -14.7) * mm, "mid": v(-24.94, -14.75) * mm, "end": v(-24.96, -14.8) * mm});
            skArc(sketch, "E1589", {"start": v(-24.96, -14.8) * mm, "mid": v(-24.96, -14.84) * mm, "end": v(-24.96, -14.88) * mm});
            skArc(sketch, "E1590", {"start": v(-24.96, -14.88) * mm, "mid": v(-24.97, -14.98) * mm, "end": v(-25, -15.08) * mm});
            skArc(sketch, "E1591", {"start": v(-25, -15.08) * mm, "mid": v(-25.03, -15.15) * mm, "end": v(-25.1, -15.21) * mm});
            skArc(sketch, "E1592", {"start": v(-25.1, -15.21) * mm, "mid": v(-25.17, -15.27) * mm, "end": v(-25.26, -15.3) * mm});
            skArc(sketch, "E1593", {"start": v(-25.26, -15.3) * mm, "mid": v(-25.4, -15.34) * mm, "end": v(-25.54, -15.36) * mm});
            skArc(sketch, "E1594", {"start": v(-25.54, -15.36) * mm, "mid": v(-25.77, -15.4) * mm, "end": v(-26, -15.46) * mm});
            skArc(sketch, "E1595", {"start": v(-26, -15.46) * mm, "mid": v(-26.08, -15.51) * mm, "end": v(-26.12, -15.6) * mm});
            skArc(sketch, "E1596", {"start": v(-26.12, -15.6) * mm, "mid": v(-26.09, -15.7) * mm, "end": v(-26, -15.75) * mm});
            skArc(sketch, "E1597", {"start": v(-26, -15.75) * mm, "mid": v(-25.78, -15.8) * mm, "end": v(-25.56, -15.84) * mm});
            skArc(sketch, "E1598", {"start": v(-25.56, -15.84) * mm, "mid": v(-25.44, -15.86) * mm, "end": v(-25.32, -15.88) * mm});
            skArc(sketch, "E1599", {"start": v(-25.32, -15.88) * mm, "mid": v(-25.26, -15.9) * mm, "end": v(-25.2, -15.91) * mm});
            skArc(sketch, "E1600", {"start": v(-25.2, -15.91) * mm, "mid": v(-25.17, -15.94) * mm, "end": v(-25.15, -15.97) * mm});
            skArc(sketch, "E1601", {"start": v(-25.15, -15.97) * mm, "mid": v(-25.13, -16.01) * mm, "end": v(-25.12, -16.06) * mm});
            skArc(sketch, "E1602", {"start": v(-25.12, -16.06) * mm, "mid": v(-25.11, -16.18) * mm, "end": v(-25.13, -16.3) * mm});
            skArc(sketch, "E1603", {"start": v(-25.13, -16.3) * mm, "mid": v(-25.2, -16.52) * mm, "end": v(-25.27, -16.74) * mm});
            skArc(sketch, "E1604", {"start": v(-25.27, -16.74) * mm, "mid": v(-25.38, -17.03) * mm, "end": v(-25.49, -17.3) * mm});
            skArc(sketch, "E1605", {"start": v(-25.49, -17.3) * mm, "mid": v(-25.63, -17.64) * mm, "end": v(-25.78, -17.96) * mm});
            skArc(sketch, "E1606", {"start": v(-25.78, -17.96) * mm, "mid": v(-25.91, -18.26) * mm, "end": v(-26.05, -18.57) * mm});
            skArc(sketch, "E1607", {"start": v(-26.05, -18.57) * mm, "mid": v(-26.12, -18.75) * mm, "end": v(-26.18, -18.94) * mm});
            skArc(sketch, "E1608", {"start": v(-26.18, -18.94) * mm, "mid": v(-26.2, -19.04) * mm, "end": v(-26.2, -19.15) * mm});
            skArc(sketch, "E1609", {"start": v(-26.2, -19.15) * mm, "mid": v(-26.19, -19.2) * mm, "end": v(-26.13, -19.22) * mm});
            skArc(sketch, "E1610", {"start": v(-26.13, -19.22) * mm, "mid": v(-26, -19.19) * mm, "end": v(-25.9, -19.1) * mm});
            skArc(sketch, "E1611", {"start": v(-25.9, -19.1) * mm, "mid": v(-25.73, -18.86) * mm, "end": v(-25.57, -18.6) * mm});
            skArc(sketch, "E1612", {"start": v(-25.57, -18.6) * mm, "mid": v(-25.39, -18.25) * mm, "end": v(-25.22, -17.9) * mm});
            skArc(sketch, "E1613", {"start": v(-25.22, -17.9) * mm, "mid": v(-25.03, -17.45) * mm, "end": v(-24.86, -17) * mm});
            skArc(sketch, "E1614", {"start": v(-24.86, -17) * mm, "mid": v(-24.75, -16.71) * mm, "end": v(-24.63, -16.44) * mm});
            skArc(sketch, "E1615", {"start": v(-24.63, -16.44) * mm, "mid": v(-24.54, -16.28) * mm, "end": v(-24.43, -16.14) * mm});
            skArc(sketch, "E1616", {"start": v(-24.43, -16.14) * mm, "mid": v(-24.3, -16.05) * mm, "end": v(-24.17, -15.98) * mm});
            skArc(sketch, "E1617", {"start": v(-24.17, -15.98) * mm, "mid": v(-23.97, -15.93) * mm, "end": v(-23.76, -15.9) * mm});
            skArc(sketch, "E1618", {"start": v(-23.76, -15.9) * mm, "mid": v(-23.53, -15.86) * mm, "end": v(-23.3, -15.82) * mm});
            skArc(sketch, "E1619", {"start": v(-23.3, -15.82) * mm, "mid": v(-23.15, -15.78) * mm, "end": v(-23, -15.7) * mm});
            skArc(sketch, "E1620", {"start": v(-23, -15.7) * mm, "mid": v(-22.94, -15.66) * mm, "end": v(-22.9, -15.59) * mm});
            skArc(sketch, "E1621", {"start": v(-22.9, -15.59) * mm, "mid": v(-22.9, -15.52) * mm, "end": v(-22.95, -15.47) * mm});
            skArc(sketch, "E1622", {"start": v(-22.95, -15.47) * mm, "mid": v(-22.98, -15.45) * mm, "end": v(-23, -15.45) * mm});
            skArc(sketch, "E1623", {"start": v(-23, -15.45) * mm, "mid": v(-23.1, -15.43) * mm, "end": v(-23.19, -15.42) * mm});
            skArc(sketch, "E1624", {"start": v(-23.19, -15.42) * mm, "mid": v(-23.3, -15.4) * mm, "end": v(-23.4, -15.39) * mm});
            skArc(sketch, "E1625", {"start": v(-23.4, -15.39) * mm, "mid": v(-23.53, -15.38) * mm, "end": v(-23.65, -15.37) * mm});
            skArc(sketch, "E1626", {"start": v(-23.65, -15.37) * mm, "mid": v(-23.77, -15.35) * mm, "end": v(-23.9, -15.34) * mm});
            skArc(sketch, "E1627", {"start": v(-23.9, -15.34) * mm, "mid": v(-24, -15.32) * mm, "end": v(-24.12, -15.3) * mm});
            skArc(sketch, "E1628", {"start": v(-24.12, -15.3) * mm, "mid": v(-24.2, -15.29) * mm, "end": v(-24.3, -15.27) * mm});
            skArc(sketch, "E1629", {"start": v(-24.3, -15.27) * mm, "mid": v(-24.34, -15.25) * mm, "end": v(-24.37, -15.23) * mm});
            skArc(sketch, "E1630", {"start": v(-24.37, -15.23) * mm, "mid": v(-24.4, -15.2) * mm, "end": v(-24.41, -15.18) * mm});
            skArc(sketch, "E1631", {"start": v(-24.41, -15.18) * mm, "mid": v(-24.43, -15.14) * mm, "end": v(-24.44, -15.1) * mm});
            skArc(sketch, "E1632", {"start": v(-24.44, -15.1) * mm, "mid": v(-24.46, -15.06) * mm, "end": v(-24.47, -15) * mm});
            skArc(sketch, "E1633", {"start": v(-24.47, -15) * mm, "mid": v(-24.47, -14.96) * mm, "end": v(-24.47, -14.92) * mm});
            skArc(sketch, "E1634", {"start": v(-24.47, -14.92) * mm, "mid": v(-24.48, -14.87) * mm, "end": v(-24.48, -14.82) * mm});
            skArc(sketch, "E1635", {"start": v(-24.48, -14.82) * mm, "mid": v(-24.5, -14.76) * mm, "end": v(-24.51, -14.7) * mm});
            skArc(sketch, "E1636", {"start": v(-24.51, -14.7) * mm, "mid": v(-24.53, -14.66) * mm, "end": v(-24.55, -14.6) * mm});
            skArc(sketch, "E1637", {"start": v(-24.55, -14.6) * mm, "mid": v(-24.58, -14.57) * mm, "end": v(-24.6, -14.53) * mm});
            skLineSegment(sketch, "E1638", {"start": v(-24.6, -14.53) * mm, "end": v(-24.73, -14.37) * mm});
            skLineSegment(sketch, "E1639", {"start": v(-24.73, -14.37) * mm, "end": v(-24.85, -14.54) * mm});
            skArc(sketch, "E1640", {"start": v(-21.74, -14.77) * mm, "mid": v(-21.73, -14.85) * mm, "end": v(-21.7, -14.92) * mm});
            skArc(sketch, "E1641", {"start": v(-21.7, -14.92) * mm, "mid": v(-21.55, -15.1) * mm, "end": v(-21.4, -15.27) * mm});
            skArc(sketch, "E1642", {"start": v(-21.4, -15.27) * mm, "mid": v(-21.24, -15.45) * mm, "end": v(-21.07, -15.63) * mm});
            skArc(sketch, "E1643", {"start": v(-21.07, -15.63) * mm, "mid": v(-20.9, -15.8) * mm, "end": v(-20.72, -15.95) * mm});
            skArc(sketch, "E1644", {"start": v(-20.72, -15.95) * mm, "mid": v(-20.59, -16.05) * mm, "end": v(-20.45, -16.16) * mm});
            skArc(sketch, "E1645", {"start": v(-20.45, -16.16) * mm, "mid": v(-20.34, -16.23) * mm, "end": v(-20.22, -16.3) * mm});
            skArc(sketch, "E1646", {"start": v(-20.22, -16.3) * mm, "mid": v(-20.13, -16.33) * mm, "end": v(-20.05, -16.35) * mm});
            skArc(sketch, "E1647", {"start": v(-20.05, -16.35) * mm, "mid": v(-20, -16.35) * mm, "end": v(-19.95, -16.33) * mm});
            skArc(sketch, "E1648", {"start": v(-19.95, -16.33) * mm, "mid": v(-19.91, -16.25) * mm, "end": v(-19.94, -16.17) * mm});
            skArc(sketch, "E1649", {"start": v(-19.94, -16.17) * mm, "mid": v(-20.16, -15.92) * mm, "end": v(-20.38, -15.67) * mm});
            skArc(sketch, "E1650", {"start": v(-20.38, -15.67) * mm, "mid": v(-20.63, -15.42) * mm, "end": v(-20.88, -15.18) * mm});
            skArc(sketch, "E1651", {"start": v(-20.88, -15.18) * mm, "mid": v(-21.1, -15) * mm, "end": v(-21.34, -14.84) * mm});
            skArc(sketch, "E1652", {"start": v(-21.34, -14.84) * mm, "mid": v(-21.44, -14.78) * mm, "end": v(-21.54, -14.72) * mm});
            skArc(sketch, "E1653", {"start": v(-21.54, -14.72) * mm, "mid": v(-21.6, -14.7) * mm, "end": v(-21.65, -14.68) * mm});
            skArc(sketch, "E1654", {"start": v(-21.65, -14.68) * mm, "mid": v(-21.69, -14.68) * mm, "end": v(-21.72, -14.7) * mm});
            skArc(sketch, "E1655", {"start": v(-21.72, -14.7) * mm, "mid": v(-21.74, -14.73) * mm, "end": v(-21.74, -14.77) * mm});
            skArc(sketch, "E1656", {"start": v(-21.82, -16.46) * mm, "mid": v(-21.84, -16.52) * mm, "end": v(-21.85, -16.58) * mm});
            skArc(sketch, "E1657", {"start": v(-21.85, -16.58) * mm, "mid": v(-21.87, -16.69) * mm, "end": v(-21.89, -16.8) * mm});
            skArc(sketch, "E1658", {"start": v(-21.89, -16.8) * mm, "mid": v(-21.9, -16.92) * mm, "end": v(-21.92, -17.05) * mm});
            skArc(sketch, "E1659", {"start": v(-21.92, -17.05) * mm, "mid": v(-21.93, -17.18) * mm, "end": v(-21.94, -17.32) * mm});
            skArc(sketch, "E1660", {"start": v(-21.94, -17.32) * mm, "mid": v(-21.96, -17.57) * mm, "end": v(-21.99, -17.81) * mm});
            skArc(sketch, "E1661", {"start": v(-21.99, -17.81) * mm, "mid": v(-22.02, -17.93) * mm, "end": v(-22.09, -18.03) * mm});
            skArc(sketch, "E1662", {"start": v(-22.09, -18.03) * mm, "mid": v(-22.17, -18.1) * mm, "end": v(-22.28, -18.14) * mm});
            skArc(sketch, "E1663", {"start": v(-22.28, -18.14) * mm, "mid": v(-22.47, -18.16) * mm, "end": v(-22.66, -18.17) * mm});
            skArc(sketch, "E1664", {"start": v(-22.66, -18.17) * mm, "mid": v(-22.92, -18.18) * mm, "end": v(-23.19, -18.23) * mm});
            skArc(sketch, "E1665", {"start": v(-23.19, -18.23) * mm, "mid": v(-23.43, -18.3) * mm, "end": v(-23.66, -18.39) * mm});
            skArc(sketch, "E1666", {"start": v(-23.66, -18.39) * mm, "mid": v(-23.87, -18.5) * mm, "end": v(-24.06, -18.64) * mm});
            skArc(sketch, "E1667", {"start": v(-24.06, -18.64) * mm, "mid": v(-24.21, -18.8) * mm, "end": v(-24.34, -18.97) * mm});
            skArc(sketch, "E1668", {"start": v(-24.34, -18.97) * mm, "mid": v(-24.43, -19.18) * mm, "end": v(-24.46, -19.4) * mm});
            skArc(sketch, "E1669", {"start": v(-24.46, -19.4) * mm, "mid": v(-24.42, -19.62) * mm, "end": v(-24.32, -19.8) * mm});
            skArc(sketch, "E1670", {"start": v(-24.32, -19.8) * mm, "mid": v(-24.12, -19.98) * mm, "end": v(-23.89, -20.1) * mm});
            skArc(sketch, "E1671", {"start": v(-23.89, -20.1) * mm, "mid": v(-23.56, -20.19) * mm, "end": v(-23.23, -20.25) * mm});
            skArc(sketch, "E1672", {"start": v(-23.23, -20.25) * mm, "mid": v(-22.97, -20.26) * mm, "end": v(-22.7, -20.24) * mm});
            skArc(sketch, "E1673", {"start": v(-22.7, -20.24) * mm, "mid": v(-22.42, -20.18) * mm, "end": v(-22.15, -20.1) * mm});
            skArc(sketch, "E1674", {"start": v(-22.15, -20.1) * mm, "mid": v(-21.92, -20.01) * mm, "end": v(-21.7, -19.9) * mm});
            skArc(sketch, "E1675", {"start": v(-21.7, -19.9) * mm, "mid": v(-21.58, -19.8) * mm, "end": v(-21.51, -19.66) * mm});
            skArc(sketch, "E1676", {"start": v(-21.51, -19.66) * mm, "mid": v(-21.5, -19.63) * mm, "end": v(-21.5, -19.6) * mm});
            skArc(sketch, "E1677", {"start": v(-21.5, -19.6) * mm, "mid": v(-21.48, -19.56) * mm, "end": v(-21.47, -19.51) * mm});
            skArc(sketch, "E1678", {"start": v(-21.47, -19.51) * mm, "mid": v(-21.46, -19.47) * mm, "end": v(-21.45, -19.43) * mm});
            skArc(sketch, "E1679", {"start": v(-21.45, -19.43) * mm, "mid": v(-21.44, -19.38) * mm, "end": v(-21.43, -19.34) * mm});
            skArc(sketch, "E1680", {"start": v(-21.43, -19.34) * mm, "mid": v(-21.4, -19.27) * mm, "end": v(-21.35, -19.2) * mm});
            skArc(sketch, "E1681", {"start": v(-21.35, -19.2) * mm, "mid": v(-21.3, -19.17) * mm, "end": v(-21.22, -19.16) * mm});
            skArc(sketch, "E1682", {"start": v(-21.22, -19.16) * mm, "mid": v(-21.11, -19.17) * mm, "end": v(-21, -19.21) * mm});
            skArc(sketch, "E1683", {"start": v(-21, -19.21) * mm, "mid": v(-20.85, -19.3) * mm, "end": v(-20.7, -19.4) * mm});
            skArc(sketch, "E1684", {"start": v(-20.7, -19.4) * mm, "mid": v(-20.56, -19.47) * mm, "end": v(-20.43, -19.55) * mm});
            skArc(sketch, "E1685", {"start": v(-20.43, -19.55) * mm, "mid": v(-20.32, -19.6) * mm, "end": v(-20.21, -19.62) * mm});
            skArc(sketch, "E1686", {"start": v(-20.21, -19.62) * mm, "mid": v(-20.13, -19.63) * mm, "end": v(-20.05, -19.63) * mm});
            skArc(sketch, "E1687", {"start": v(-20.05, -19.63) * mm, "mid": v(-20, -19.6) * mm, "end": v(-19.96, -19.57) * mm});
            skArc(sketch, "E1688", {"start": v(-19.96, -19.57) * mm, "mid": v(-19.94, -19.5) * mm, "end": v(-19.95, -19.45) * mm});
            skArc(sketch, "E1689", {"start": v(-19.95, -19.45) * mm, "mid": v(-20, -19.36) * mm, "end": v(-20.07, -19.28) * mm});
            skArc(sketch, "E1690", {"start": v(-20.07, -19.28) * mm, "mid": v(-20.18, -19.17) * mm, "end": v(-20.3, -19.08) * mm});
            skArc(sketch, "E1691", {"start": v(-20.3, -19.08) * mm, "mid": v(-20.46, -18.95) * mm, "end": v(-20.63, -18.83) * mm});
            skArc(sketch, "E1692", {"start": v(-20.63, -18.83) * mm, "mid": v(-20.86, -18.66) * mm, "end": v(-21.1, -18.49) * mm});
            skArc(sketch, "E1693", {"start": v(-21.1, -18.49) * mm, "mid": v(-21.2, -18.38) * mm, "end": v(-21.3, -18.24) * mm});
            skArc(sketch, "E1694", {"start": v(-21.3, -18.24) * mm, "mid": v(-21.36, -18.1) * mm, "end": v(-21.4, -17.93) * mm});
            skArc(sketch, "E1695", {"start": v(-21.4, -17.93) * mm, "mid": v(-21.44, -17.61) * mm, "end": v(-21.46, -17.3) * mm});
            skArc(sketch, "E1696", {"start": v(-21.46, -17.3) * mm, "mid": v(-21.48, -17.1) * mm, "end": v(-21.5, -16.9) * mm});
            skArc(sketch, "E1697", {"start": v(-21.5, -16.9) * mm, "mid": v(-21.5, -16.77) * mm, "end": v(-21.53, -16.64) * mm});
            skArc(sketch, "E1698", {"start": v(-21.53, -16.64) * mm, "mid": v(-21.55, -16.55) * mm, "end": v(-21.57, -16.46) * mm});
            skArc(sketch, "E1699", {"start": v(-21.57, -16.46) * mm, "mid": v(-21.6, -16.41) * mm, "end": v(-21.63, -16.37) * mm});
            skArc(sketch, "E1700", {"start": v(-21.63, -16.37) * mm, "mid": v(-21.66, -16.34) * mm, "end": v(-21.7, -16.31) * mm});
            skArc(sketch, "E1701", {"start": v(-21.7, -16.31) * mm, "mid": v(-21.71, -16.3) * mm, "end": v(-21.73, -16.3) * mm});
            skArc(sketch, "E1702", {"start": v(-21.73, -16.3) * mm, "mid": v(-21.75, -16.32) * mm, "end": v(-21.77, -16.34) * mm});
            skArc(sketch, "E1703", {"start": v(-21.77, -16.34) * mm, "mid": v(-21.8, -16.4) * mm, "end": v(-21.82, -16.46) * mm});
            skArc(sketch, "E1704", {"start": v(-22.04, -18.74) * mm, "mid": v(-22, -18.8) * mm, "end": v(-21.98, -18.84) * mm});
            skArc(sketch, "E1705", {"start": v(-21.98, -18.84) * mm, "mid": v(-21.96, -18.9) * mm, "end": v(-21.96, -18.98) * mm});
            skArc(sketch, "E1706", {"start": v(-21.96, -18.98) * mm, "mid": v(-21.96, -19.06) * mm, "end": v(-21.98, -19.15) * mm});
            skArc(sketch, "E1707", {"start": v(-21.98, -19.15) * mm, "mid": v(-22, -19.25) * mm, "end": v(-22.03, -19.35) * mm});
            skArc(sketch, "E1708", {"start": v(-22.03, -19.35) * mm, "mid": v(-22.05, -19.4) * mm, "end": v(-22.08, -19.45) * mm});
            skArc(sketch, "E1709", {"start": v(-22.08, -19.45) * mm, "mid": v(-22.1, -19.5) * mm, "end": v(-22.14, -19.53) * mm});
            skArc(sketch, "E1710", {"start": v(-22.14, -19.53) * mm, "mid": v(-22.18, -19.56) * mm, "end": v(-22.22, -19.59) * mm});
            skArc(sketch, "E1711", {"start": v(-22.22, -19.59) * mm, "mid": v(-22.27, -19.61) * mm, "end": v(-22.33, -19.63) * mm});
            skArc(sketch, "E1712", {"start": v(-22.33, -19.63) * mm, "mid": v(-22.57, -19.7) * mm, "end": v(-22.82, -19.74) * mm});
            skArc(sketch, "E1713", {"start": v(-22.82, -19.74) * mm, "mid": v(-23.07, -19.75) * mm, "end": v(-23.31, -19.75) * mm});
            skArc(sketch, "E1714", {"start": v(-23.31, -19.75) * mm, "mid": v(-23.52, -19.72) * mm, "end": v(-23.72, -19.67) * mm});
            skArc(sketch, "E1715", {"start": v(-23.72, -19.67) * mm, "mid": v(-23.83, -19.6) * mm, "end": v(-23.91, -19.5) * mm});
            skArc(sketch, "E1716", {"start": v(-23.91, -19.5) * mm, "mid": v(-23.96, -19.4) * mm, "end": v(-23.98, -19.27) * mm});
            skArc(sketch, "E1717", {"start": v(-23.98, -19.27) * mm, "mid": v(-23.98, -19.17) * mm, "end": v(-23.94, -19.07) * mm});
            skArc(sketch, "E1718", {"start": v(-23.94, -19.07) * mm, "mid": v(-23.88, -18.97) * mm, "end": v(-23.79, -18.9) * mm});
            skArc(sketch, "E1719", {"start": v(-23.79, -18.9) * mm, "mid": v(-23.66, -18.82) * mm, "end": v(-23.53, -18.77) * mm});
            skArc(sketch, "E1720", {"start": v(-23.53, -18.77) * mm, "mid": v(-23.37, -18.72) * mm, "end": v(-23.2, -18.7) * mm});
            skArc(sketch, "E1721", {"start": v(-23.2, -18.7) * mm, "mid": v(-22.95, -18.67) * mm, "end": v(-22.7, -18.67) * mm});
            skArc(sketch, "E1722", {"start": v(-22.7, -18.67) * mm, "mid": v(-22.45, -18.67) * mm, "end": v(-22.2, -18.67) * mm});
            skArc(sketch, "E1723", {"start": v(-22.2, -18.67) * mm, "mid": v(-22.11, -18.7) * mm, "end": v(-22.04, -18.74) * mm});
            skArc(sketch, "E1724", {"start": v(-36.5, -14.52) * mm, "mid": v(-36.55, -14.59) * mm, "end": v(-36.52, -14.66) * mm});
            skArc(sketch, "E1725", {"start": v(-36.52, -14.66) * mm, "mid": v(-36.41, -14.74) * mm, "end": v(-36.3, -14.8) * mm});
            skArc(sketch, "E1726", {"start": v(-36.3, -14.8) * mm, "mid": v(-36, -14.88) * mm, "end": v(-35.7, -14.95) * mm});
            skArc(sketch, "E1727", {"start": v(-35.7, -14.95) * mm, "mid": v(-35.17, -15.06) * mm, "end": v(-34.63, -15.16) * mm});
            skArc(sketch, "E1728", {"start": v(-34.63, -15.16) * mm, "mid": v(-34.28, -15.22) * mm, "end": v(-33.93, -15.28) * mm});
            skArc(sketch, "E1729", {"start": v(-33.93, -15.28) * mm, "mid": v(-33.78, -15.3) * mm, "end": v(-33.63, -15.32) * mm});
            skArc(sketch, "E1730", {"start": v(-33.63, -15.32) * mm, "mid": v(-33.55, -15.32) * mm, "end": v(-33.47, -15.31) * mm});
            skArc(sketch, "E1731", {"start": v(-33.47, -15.31) * mm, "mid": v(-33.4, -15.3) * mm, "end": v(-33.35, -15.25) * mm});
            skArc(sketch, "E1732", {"start": v(-33.35, -15.25) * mm, "mid": v(-33.29, -15.16) * mm, "end": v(-33.27, -15.06) * mm});
            skArc(sketch, "E1733", {"start": v(-33.27, -15.06) * mm, "mid": v(-33.3, -14.96) * mm, "end": v(-33.38, -14.89) * mm});
            skArc(sketch, "E1734", {"start": v(-33.38, -14.89) * mm, "mid": v(-33.58, -14.8) * mm, "end": v(-33.8, -14.75) * mm});
            skArc(sketch, "E1735", {"start": v(-33.8, -14.75) * mm, "mid": v(-34.23, -14.67) * mm, "end": v(-34.67, -14.6) * mm});
            skArc(sketch, "E1736", {"start": v(-34.67, -14.6) * mm, "mid": v(-35.02, -14.56) * mm, "end": v(-35.37, -14.51) * mm});
            skArc(sketch, "E1737", {"start": v(-35.37, -14.51) * mm, "mid": v(-35.64, -14.49) * mm, "end": v(-35.92, -14.47) * mm});
            skArc(sketch, "E1738", {"start": v(-35.92, -14.47) * mm, "mid": v(-36.12, -14.46) * mm, "end": v(-36.32, -14.47) * mm});
            skArc(sketch, "E1739", {"start": v(-36.32, -14.47) * mm, "mid": v(-36.42, -14.48) * mm, "end": v(-36.5, -14.52) * mm});
            skArc(sketch, "E1740", {"start": v(-35.17, -15.42) * mm, "mid": v(-35.22, -15.45) * mm, "end": v(-35.26, -15.51) * mm});
            skArc(sketch, "E1741", {"start": v(-35.26, -15.51) * mm, "mid": v(-35.3, -15.63) * mm, "end": v(-35.33, -15.76) * mm});
            skArc(sketch, "E1742", {"start": v(-35.33, -15.76) * mm, "mid": v(-35.36, -15.9) * mm, "end": v(-35.37, -16.05) * mm});
            skArc(sketch, "E1743", {"start": v(-35.37, -16.05) * mm, "mid": v(-35.37, -16.18) * mm, "end": v(-35.36, -16.3) * mm});
            skArc(sketch, "E1744", {"start": v(-35.36, -16.3) * mm, "mid": v(-35.33, -16.47) * mm, "end": v(-35.3, -16.62) * mm});
            skArc(sketch, "E1745", {"start": v(-35.3, -16.62) * mm, "mid": v(-35.25, -16.8) * mm, "end": v(-35.2, -16.97) * mm});
            skArc(sketch, "E1746", {"start": v(-35.2, -16.97) * mm, "mid": v(-35.14, -17.14) * mm, "end": v(-35.07, -17.32) * mm});
            skArc(sketch, "E1747", {"start": v(-35.07, -17.32) * mm, "mid": v(-35, -17.47) * mm, "end": v(-34.93, -17.63) * mm});
            skArc(sketch, "E1748", {"start": v(-34.93, -17.63) * mm, "mid": v(-34.9, -17.7) * mm, "end": v(-34.86, -17.79) * mm});
            skArc(sketch, "E1749", {"start": v(-34.86, -17.79) * mm, "mid": v(-34.82, -17.89) * mm, "end": v(-34.78, -18) * mm});
            skArc(sketch, "E1750", {"start": v(-34.78, -18) * mm, "mid": v(-34.74, -18.1) * mm, "end": v(-34.7, -18.2) * mm});
            skArc(sketch, "E1751", {"start": v(-34.7, -18.2) * mm, "mid": v(-34.68, -18.3) * mm, "end": v(-34.65, -18.4) * mm});
            skArc(sketch, "E1752", {"start": v(-34.65, -18.4) * mm, "mid": v(-34.6, -18.7) * mm, "end": v(-34.58, -19) * mm});
            skArc(sketch, "E1753", {"start": v(-34.58, -19) * mm, "mid": v(-34.62, -19.2) * mm, "end": v(-34.73, -19.37) * mm});
            skArc(sketch, "E1754", {"start": v(-34.73, -19.37) * mm, "mid": v(-34.9, -19.48) * mm, "end": v(-35.1, -19.5) * mm});
            skArc(sketch, "E1755", {"start": v(-35.1, -19.5) * mm, "mid": v(-35.37, -19.45) * mm, "end": v(-35.64, -19.36) * mm});
            skArc(sketch, "E1756", {"start": v(-35.64, -19.36) * mm, "mid": v(-35.77, -19.3) * mm, "end": v(-35.9, -19.26) * mm});
            skArc(sketch, "E1757", {"start": v(-35.9, -19.26) * mm, "mid": v(-36, -19.24) * mm, "end": v(-36.09, -19.23) * mm});
            skArc(sketch, "E1758", {"start": v(-36.09, -19.23) * mm, "mid": v(-36.15, -19.23) * mm, "end": v(-36.2, -19.25) * mm});
            skArc(sketch, "E1759", {"start": v(-36.2, -19.25) * mm, "mid": v(-36.25, -19.28) * mm, "end": v(-36.28, -19.33) * mm});
            skArc(sketch, "E1760", {"start": v(-36.28, -19.33) * mm, "mid": v(-36.29, -19.44) * mm, "end": v(-36.23, -19.54) * mm});
            skArc(sketch, "E1761", {"start": v(-36.23, -19.54) * mm, "mid": v(-36.07, -19.66) * mm, "end": v(-35.9, -19.76) * mm});
            skArc(sketch, "E1762", {"start": v(-35.9, -19.76) * mm, "mid": v(-35.68, -19.86) * mm, "end": v(-35.44, -19.93) * mm});
            skArc(sketch, "E1763", {"start": v(-35.44, -19.93) * mm, "mid": v(-35.2, -19.98) * mm, "end": v(-34.97, -20) * mm});
            skArc(sketch, "E1764", {"start": v(-34.97, -20) * mm, "mid": v(-34.86, -19.99) * mm, "end": v(-34.76, -19.98) * mm});
            skArc(sketch, "E1765", {"start": v(-34.76, -19.98) * mm, "mid": v(-34.7, -19.97) * mm, "end": v(-34.63, -19.95) * mm});
            skArc(sketch, "E1766", {"start": v(-34.63, -19.95) * mm, "mid": v(-34.57, -19.92) * mm, "end": v(-34.52, -19.88) * mm});
            skArc(sketch, "E1767", {"start": v(-34.52, -19.88) * mm, "mid": v(-34.45, -19.82) * mm, "end": v(-34.38, -19.76) * mm});
            skArc(sketch, "E1768", {"start": v(-34.38, -19.76) * mm, "mid": v(-34.23, -19.56) * mm, "end": v(-34.13, -19.33) * mm});
            skArc(sketch, "E1769", {"start": v(-34.13, -19.33) * mm, "mid": v(-34.08, -19.05) * mm, "end": v(-34.07, -18.76) * mm});
            skArc(sketch, "E1770", {"start": v(-34.07, -18.76) * mm, "mid": v(-34.12, -18.4) * mm, "end": v(-34.2, -18.06) * mm});
            skArc(sketch, "E1771", {"start": v(-34.2, -18.06) * mm, "mid": v(-34.35, -17.66) * mm, "end": v(-34.53, -17.27) * mm});
            skArc(sketch, "E1772", {"start": v(-34.53, -17.27) * mm, "mid": v(-34.64, -17.06) * mm, "end": v(-34.74, -16.84) * mm});
            skArc(sketch, "E1773", {"start": v(-34.74, -16.84) * mm, "mid": v(-34.78, -16.73) * mm, "end": v(-34.82, -16.6) * mm});
            skArc(sketch, "E1774", {"start": v(-34.82, -16.6) * mm, "mid": v(-34.85, -16.5) * mm, "end": v(-34.86, -16.37) * mm});
            skArc(sketch, "E1775", {"start": v(-34.86, -16.37) * mm, "mid": v(-34.87, -16.19) * mm, "end": v(-34.87, -16) * mm});
            skArc(sketch, "E1776", {"start": v(-34.87, -16) * mm, "mid": v(-34.87, -15.8) * mm, "end": v(-34.88, -15.6) * mm});
            skArc(sketch, "E1777", {"start": v(-34.88, -15.6) * mm, "mid": v(-34.9, -15.52) * mm, "end": v(-34.92, -15.44) * mm});
            skArc(sketch, "E1778", {"start": v(-34.92, -15.44) * mm, "mid": v(-34.96, -15.4) * mm, "end": v(-35.01, -15.39) * mm});
            skArc(sketch, "E1779", {"start": v(-35.01, -15.39) * mm, "mid": v(-35.1, -15.4) * mm, "end": v(-35.17, -15.42) * mm});
            skArc(sketch, "E1780", {"start": v(-33.32, -16.6) * mm, "mid": v(-33.34, -16.66) * mm, "end": v(-33.33, -16.7) * mm});
            skArc(sketch, "E1781", {"start": v(-33.33, -16.7) * mm, "mid": v(-33.06, -17.24) * mm, "end": v(-32.79, -17.77) * mm});
            skArc(sketch, "E1782", {"start": v(-32.79, -17.77) * mm, "mid": v(-32.54, -18.25) * mm, "end": v(-32.28, -18.72) * mm});
            skArc(sketch, "E1783", {"start": v(-32.28, -18.72) * mm, "mid": v(-32.14, -18.96) * mm, "end": v(-31.98, -19.19) * mm});
            skArc(sketch, "E1784", {"start": v(-31.98, -19.19) * mm, "mid": v(-31.86, -19.33) * mm, "end": v(-31.74, -19.48) * mm});
            skArc(sketch, "E1785", {"start": v(-31.74, -19.48) * mm, "mid": v(-31.69, -19.53) * mm, "end": v(-31.62, -19.56) * mm});
            skArc(sketch, "E1786", {"start": v(-31.62, -19.56) * mm, "mid": v(-31.58, -19.55) * mm, "end": v(-31.56, -19.5) * mm});
            skArc(sketch, "E1787", {"start": v(-31.56, -19.5) * mm, "mid": v(-31.55, -19.4) * mm, "end": v(-31.56, -19.29) * mm});
            skArc(sketch, "E1788", {"start": v(-31.56, -19.29) * mm, "mid": v(-31.6, -19.12) * mm, "end": v(-31.65, -18.96) * mm});
            skArc(sketch, "E1789", {"start": v(-31.65, -18.96) * mm, "mid": v(-31.74, -18.73) * mm, "end": v(-31.85, -18.5) * mm});
            skArc(sketch, "E1790", {"start": v(-31.85, -18.5) * mm, "mid": v(-31.98, -18.24) * mm, "end": v(-32.12, -17.98) * mm});
            skArc(sketch, "E1791", {"start": v(-32.12, -17.98) * mm, "mid": v(-32.29, -17.7) * mm, "end": v(-32.46, -17.43) * mm});
            skArc(sketch, "E1792", {"start": v(-32.46, -17.43) * mm, "mid": v(-32.63, -17.17) * mm, "end": v(-32.8, -16.92) * mm});
            skArc(sketch, "E1793", {"start": v(-32.8, -16.92) * mm, "mid": v(-32.9, -16.79) * mm, "end": v(-33.02, -16.66) * mm});
            skArc(sketch, "E1794", {"start": v(-33.02, -16.66) * mm, "mid": v(-33.1, -16.6) * mm, "end": v(-33.18, -16.57) * mm});
            skArc(sketch, "E1795", {"start": v(-33.18, -16.57) * mm, "mid": v(-33.26, -16.57) * mm, "end": v(-33.32, -16.6) * mm});
            skArc(sketch, "E1796", {"start": v(-36.8, -17) * mm, "mid": v(-36.9, -17.16) * mm, "end": v(-36.98, -17.33) * mm});
            skArc(sketch, "E1797", {"start": v(-36.98, -17.33) * mm, "mid": v(-37.11, -17.6) * mm, "end": v(-37.24, -17.86) * mm});
            skArc(sketch, "E1798", {"start": v(-37.24, -17.86) * mm, "mid": v(-37.37, -18.14) * mm, "end": v(-37.5, -18.42) * mm});
            skArc(sketch, "E1799", {"start": v(-37.5, -18.42) * mm, "mid": v(-37.6, -18.64) * mm, "end": v(-37.68, -18.85) * mm});
            skArc(sketch, "E1800", {"start": v(-37.68, -18.85) * mm, "mid": v(-37.77, -19.1) * mm, "end": v(-37.85, -19.33) * mm});
            skArc(sketch, "E1801", {"start": v(-37.85, -19.33) * mm, "mid": v(-37.85, -19.41) * mm, "end": v(-37.83, -19.48) * mm});
            skArc(sketch, "E1802", {"start": v(-37.83, -19.48) * mm, "mid": v(-37.78, -19.51) * mm, "end": v(-37.72, -19.5) * mm});
            skArc(sketch, "E1803", {"start": v(-37.72, -19.5) * mm, "mid": v(-37.57, -19.36) * mm, "end": v(-37.43, -19.22) * mm});
            skArc(sketch, "E1804", {"start": v(-37.43, -19.22) * mm, "mid": v(-37.3, -19.06) * mm, "end": v(-37.17, -18.89) * mm});
            skArc(sketch, "E1805", {"start": v(-37.17, -18.89) * mm, "mid": v(-37.03, -18.64) * mm, "end": v(-36.9, -18.38) * mm});
            skArc(sketch, "E1806", {"start": v(-36.9, -18.38) * mm, "mid": v(-36.76, -18.12) * mm, "end": v(-36.65, -17.84) * mm});
            skArc(sketch, "E1807", {"start": v(-36.65, -17.84) * mm, "mid": v(-36.57, -17.62) * mm, "end": v(-36.51, -17.39) * mm});
            skArc(sketch, "E1808", {"start": v(-36.51, -17.39) * mm, "mid": v(-36.47, -17.2) * mm, "end": v(-36.45, -17) * mm});
            skArc(sketch, "E1809", {"start": v(-36.45, -17) * mm, "mid": v(-36.46, -16.9) * mm, "end": v(-36.5, -16.8) * mm});
            skArc(sketch, "E1810", {"start": v(-36.5, -16.8) * mm, "mid": v(-36.56, -16.77) * mm, "end": v(-36.62, -16.79) * mm});
            skArc(sketch, "E1811", {"start": v(-36.62, -16.79) * mm, "mid": v(-36.72, -16.89) * mm, "end": v(-36.8, -17) * mm});
            skArc(sketch, "E1812", {"start": v(9.73, -14.62) * mm, "mid": v(9.71, -14.67) * mm, "end": v(9.7, -14.73) * mm});
            skArc(sketch, "E1813", {"start": v(9.7, -14.73) * mm, "mid": v(9.7, -14.94) * mm, "end": v(9.68, -15.15) * mm});
            skArc(sketch, "E1814", {"start": v(9.68, -15.15) * mm, "mid": v(9.66, -15.4) * mm, "end": v(9.64, -15.65) * mm});
            skArc(sketch, "E1815", {"start": v(9.64, -15.65) * mm, "mid": v(9.63, -15.93) * mm, "end": v(9.61, -16.21) * mm});
            skArc(sketch, "E1816", {"start": v(9.61, -16.21) * mm, "mid": v(9.6, -16.81) * mm, "end": v(9.58, -17.41) * mm});
            skArc(sketch, "E1817", {"start": v(9.58, -17.41) * mm, "mid": v(9.58, -18) * mm, "end": v(9.6, -18.59) * mm});
            skArc(sketch, "E1818", {"start": v(9.6, -18.59) * mm, "mid": v(9.62, -19.1) * mm, "end": v(9.65, -19.63) * mm});
            skArc(sketch, "E1819", {"start": v(9.65, -19.63) * mm, "mid": v(9.68, -19.76) * mm, "end": v(9.75, -19.88) * mm});
            skArc(sketch, "E1820", {"start": v(9.75, -19.88) * mm, "mid": v(9.92, -20) * mm, "end": v(10.12, -20.01) * mm});
            skArc(sketch, "E1821", {"start": v(10.12, -20.01) * mm, "mid": v(10.55, -19.91) * mm, "end": v(10.97, -19.78) * mm});
            skArc(sketch, "E1822", {"start": v(10.97, -19.78) * mm, "mid": v(11.49, -19.58) * mm, "end": v(11.99, -19.34) * mm});
            skArc(sketch, "E1823", {"start": v(11.99, -19.34) * mm, "mid": v(12.53, -19.05) * mm, "end": v(13.05, -18.73) * mm});
            skArc(sketch, "E1824", {"start": v(13.05, -18.73) * mm, "mid": v(13.4, -18.47) * mm, "end": v(13.76, -18.2) * mm});
            skArc(sketch, "E1825", {"start": v(13.76, -18.2) * mm, "mid": v(14.12, -17.88) * mm, "end": v(14.47, -17.55) * mm});
            skArc(sketch, "E1826", {"start": v(14.47, -17.55) * mm, "mid": v(14.77, -17.24) * mm, "end": v(15.05, -16.93) * mm});
            skArc(sketch, "E1827", {"start": v(15.05, -16.93) * mm, "mid": v(15.1, -16.82) * mm, "end": v(15.05, -16.72) * mm});
            skArc(sketch, "E1828", {"start": v(15.05, -16.72) * mm, "mid": v(15, -16.7) * mm, "end": v(14.95, -16.7) * mm});
            skArc(sketch, "E1829", {"start": v(14.95, -16.7) * mm, "mid": v(14.85, -16.73) * mm, "end": v(14.76, -16.78) * mm});
            skArc(sketch, "E1830", {"start": v(14.76, -16.78) * mm, "mid": v(14.62, -16.85) * mm, "end": v(14.5, -16.94) * mm});
            skArc(sketch, "E1831", {"start": v(14.5, -16.94) * mm, "mid": v(14.33, -17.07) * mm, "end": v(14.17, -17.2) * mm});
            skArc(sketch, "E1832", {"start": v(14.17, -17.2) * mm, "mid": v(13.68, -17.58) * mm, "end": v(13.17, -17.94) * mm});
            skArc(sketch, "E1833", {"start": v(13.17, -17.94) * mm, "mid": v(12.64, -18.29) * mm, "end": v(12.1, -18.61) * mm});
            skArc(sketch, "E1834", {"start": v(12.1, -18.61) * mm, "mid": v(11.6, -18.88) * mm, "end": v(11.11, -19.12) * mm});
            skArc(sketch, "E1835", {"start": v(11.11, -19.12) * mm, "mid": v(10.83, -19.22) * mm, "end": v(10.53, -19.25) * mm});
            skArc(sketch, "E1836", {"start": v(10.53, -19.25) * mm, "mid": v(10.44, -19.25) * mm, "end": v(10.35, -19.25) * mm});
            skArc(sketch, "E1837", {"start": v(10.35, -19.25) * mm, "mid": v(10.3, -19.24) * mm, "end": v(10.26, -19.22) * mm});
            skArc(sketch, "E1838", {"start": v(10.26, -19.22) * mm, "mid": v(10.23, -19.2) * mm, "end": v(10.2, -19.17) * mm});
            skArc(sketch, "E1839", {"start": v(10.2, -19.17) * mm, "mid": v(10.18, -19.1) * mm, "end": v(10.16, -19.05) * mm});
            skArc(sketch, "E1840", {"start": v(10.16, -19.05) * mm, "mid": v(10.15, -18.97) * mm, "end": v(10.14, -18.9) * mm});
            skArc(sketch, "E1841", {"start": v(10.14, -18.9) * mm, "mid": v(10.12, -18.6) * mm, "end": v(10.1, -18.3) * mm});
            skArc(sketch, "E1842", {"start": v(10.1, -18.3) * mm, "mid": v(10.08, -17.95) * mm, "end": v(10.07, -17.6) * mm});
            skArc(sketch, "E1843", {"start": v(10.07, -17.6) * mm, "mid": v(10.05, -17.2) * mm, "end": v(10.04, -16.8) * mm});
            skArc(sketch, "E1844", {"start": v(10.04, -16.8) * mm, "mid": v(10.02, -16.17) * mm, "end": v(10, -15.53) * mm});
            skArc(sketch, "E1845", {"start": v(10, -15.53) * mm, "mid": v(9.98, -15.22) * mm, "end": v(9.95, -14.9) * mm});
            skArc(sketch, "E1846", {"start": v(9.95, -14.9) * mm, "mid": v(9.93, -14.71) * mm, "end": v(9.9, -14.53) * mm});
            skArc(sketch, "E1847", {"start": v(9.9, -14.53) * mm, "mid": v(9.88, -14.48) * mm, "end": v(9.83, -14.46) * mm});
            skArc(sketch, "E1848", {"start": v(9.83, -14.46) * mm, "mid": v(9.81, -14.46) * mm, "end": v(9.8, -14.47) * mm});
            skArc(sketch, "E1849", {"start": v(9.8, -14.47) * mm, "mid": v(9.79, -14.49) * mm, "end": v(9.77, -14.5) * mm});
            skArc(sketch, "E1850", {"start": v(9.77, -14.5) * mm, "mid": v(9.76, -14.53) * mm, "end": v(9.75, -14.56) * mm});
            skArc(sketch, "E1851", {"start": v(9.75, -14.56) * mm, "mid": v(9.74, -14.59) * mm, "end": v(9.73, -14.62) * mm});
            skArc(sketch, "E1852", {"start": v(20.99, -14.82) * mm, "mid": v(20.97, -14.88) * mm, "end": v(21, -14.93) * mm});
            skArc(sketch, "E1853", {"start": v(21, -14.93) * mm, "mid": v(21.08, -15.03) * mm, "end": v(21.17, -15.12) * mm});
            skArc(sketch, "E1854", {"start": v(21.17, -15.12) * mm, "mid": v(21.31, -15.24) * mm, "end": v(21.46, -15.35) * mm});
            skArc(sketch, "E1855", {"start": v(21.46, -15.35) * mm, "mid": v(21.66, -15.48) * mm, "end": v(21.86, -15.6) * mm});
            skArc(sketch, "E1856", {"start": v(21.86, -15.6) * mm, "mid": v(22.15, -15.77) * mm, "end": v(22.45, -15.94) * mm});
            skArc(sketch, "E1857", {"start": v(22.45, -15.94) * mm, "mid": v(22.65, -16.04) * mm, "end": v(22.86, -16.14) * mm});
            skArc(sketch, "E1858", {"start": v(22.86, -16.14) * mm, "mid": v(23, -16.2) * mm, "end": v(23.16, -16.23) * mm});
            skArc(sketch, "E1859", {"start": v(23.16, -16.23) * mm, "mid": v(23.25, -16.24) * mm, "end": v(23.33, -16.21) * mm});
            skArc(sketch, "E1860", {"start": v(23.33, -16.21) * mm, "mid": v(23.36, -16.2) * mm, "end": v(23.39, -16.18) * mm});
            skArc(sketch, "E1861", {"start": v(23.39, -16.18) * mm, "mid": v(23.41, -16.15) * mm, "end": v(23.43, -16.13) * mm});
            skArc(sketch, "E1862", {"start": v(23.43, -16.13) * mm, "mid": v(23.45, -16.1) * mm, "end": v(23.46, -16.08) * mm});
            skArc(sketch, "E1863", {"start": v(23.46, -16.08) * mm, "mid": v(23.47, -16.06) * mm, "end": v(23.48, -16.03) * mm});
            skArc(sketch, "E1864", {"start": v(23.48, -16.03) * mm, "mid": v(23.45, -15.92) * mm, "end": v(23.37, -15.83) * mm});
            skArc(sketch, "E1865", {"start": v(23.37, -15.83) * mm, "mid": v(23.06, -15.63) * mm, "end": v(22.75, -15.45) * mm});
            skArc(sketch, "E1866", {"start": v(22.75, -15.45) * mm, "mid": v(22.4, -15.26) * mm, "end": v(22.06, -15.09) * mm});
            skArc(sketch, "E1867", {"start": v(22.06, -15.09) * mm, "mid": v(21.76, -14.96) * mm, "end": v(21.45, -14.85) * mm});
            skArc(sketch, "E1868", {"start": v(21.45, -14.85) * mm, "mid": v(21.3, -14.8) * mm, "end": v(21.14, -14.76) * mm});
            skArc(sketch, "E1869", {"start": v(21.14, -14.76) * mm, "mid": v(21.1, -14.75) * mm, "end": v(21.07, -14.75) * mm});
            skArc(sketch, "E1870", {"start": v(21.07, -14.75) * mm, "mid": v(21.05, -14.75) * mm, "end": v(21.03, -14.76) * mm});
            skArc(sketch, "E1871", {"start": v(21.03, -14.76) * mm, "mid": v(21, -14.79) * mm, "end": v(20.99, -14.82) * mm});
            skArc(sketch, "E1872", {"start": v(26.16, -16.84) * mm, "mid": v(26.1, -16.88) * mm, "end": v(26.03, -16.93) * mm});
            skArc(sketch, "E1873", {"start": v(26.03, -16.93) * mm, "mid": v(25.92, -17.02) * mm, "end": v(25.8, -17.12) * mm});
            skArc(sketch, "E1874", {"start": v(25.8, -17.12) * mm, "mid": v(25.67, -17.23) * mm, "end": v(25.54, -17.35) * mm});
            skArc(sketch, "E1875", {"start": v(25.54, -17.35) * mm, "mid": v(25.4, -17.47) * mm, "end": v(25.27, -17.6) * mm});
            skArc(sketch, "E1876", {"start": v(25.27, -17.6) * mm, "mid": v(24.9, -17.92) * mm, "end": v(24.5, -18.23) * mm});
            skArc(sketch, "E1877", {"start": v(24.5, -18.23) * mm, "mid": v(24.1, -18.5) * mm, "end": v(23.7, -18.73) * mm});
            skArc(sketch, "E1878", {"start": v(23.7, -18.73) * mm, "mid": v(23.27, -18.94) * mm, "end": v(22.83, -19.12) * mm});
            skArc(sketch, "E1879", {"start": v(22.83, -19.12) * mm, "mid": v(22.36, -19.27) * mm, "end": v(21.89, -19.4) * mm});
            skArc(sketch, "E1880", {"start": v(21.89, -19.4) * mm, "mid": v(21.64, -19.45) * mm, "end": v(21.4, -19.52) * mm});
            skArc(sketch, "E1881", {"start": v(21.4, -19.52) * mm, "mid": v(21.24, -19.57) * mm, "end": v(21.07, -19.63) * mm});
            skArc(sketch, "E1882", {"start": v(21.07, -19.63) * mm, "mid": v(20.97, -19.68) * mm, "end": v(20.87, -19.74) * mm});
            skArc(sketch, "E1883", {"start": v(20.87, -19.74) * mm, "mid": v(20.84, -19.78) * mm, "end": v(20.83, -19.84) * mm});
            skArc(sketch, "E1884", {"start": v(20.83, -19.84) * mm, "mid": v(20.93, -20) * mm, "end": v(21.12, -20.04) * mm});
            skArc(sketch, "E1885", {"start": v(21.12, -20.04) * mm, "mid": v(21.71, -19.93) * mm, "end": v(22.3, -19.8) * mm});
            skArc(sketch, "E1886", {"start": v(22.3, -19.8) * mm, "mid": v(22.94, -19.6) * mm, "end": v(23.57, -19.37) * mm});
            skArc(sketch, "E1887", {"start": v(23.57, -19.37) * mm, "mid": v(24.1, -19.13) * mm, "end": v(24.59, -18.84) * mm});
            skArc(sketch, "E1888", {"start": v(24.59, -18.84) * mm, "mid": v(24.95, -18.6) * mm, "end": v(25.3, -18.32) * mm});
            skArc(sketch, "E1889", {"start": v(25.3, -18.32) * mm, "mid": v(25.62, -18.05) * mm, "end": v(25.92, -17.76) * mm});
            skArc(sketch, "E1890", {"start": v(25.92, -17.76) * mm, "mid": v(26.15, -17.5) * mm, "end": v(26.37, -17.23) * mm});
            skArc(sketch, "E1891", {"start": v(26.37, -17.23) * mm, "mid": v(26.45, -17.06) * mm, "end": v(26.49, -16.86) * mm});
            skArc(sketch, "E1892", {"start": v(26.49, -16.86) * mm, "mid": v(26.48, -16.8) * mm, "end": v(26.47, -16.75) * mm});
            skArc(sketch, "E1893", {"start": v(26.47, -16.75) * mm, "mid": v(26.46, -16.72) * mm, "end": v(26.43, -16.71) * mm});
            skArc(sketch, "E1894", {"start": v(26.43, -16.71) * mm, "mid": v(26.39, -16.71) * mm, "end": v(26.35, -16.73) * mm});
            skArc(sketch, "E1895", {"start": v(26.35, -16.73) * mm, "mid": v(26.25, -16.78) * mm, "end": v(26.16, -16.84) * mm});
            skArc(sketch, "E1896", {"start": v(-1.79, -14.74) * mm, "mid": v(-1.91, -14.79) * mm, "end": v(-2, -14.88) * mm});
            skArc(sketch, "E1897", {"start": v(-2, -14.88) * mm, "mid": v(-2.01, -14.97) * mm, "end": v(-1.95, -15.02) * mm});
            skArc(sketch, "E1898", {"start": v(-1.95, -15.02) * mm, "mid": v(-1.42, -15.09) * mm, "end": v(-0.9, -15.13) * mm});
            skArc(sketch, "E1899", {"start": v(-0.9, -15.13) * mm, "mid": v(-0.1, -15.15) * mm, "end": v(0.7, -15.16) * mm});
            skArc(sketch, "E1900", {"start": v(0.7, -15.16) * mm, "mid": v(1.3, -15.17) * mm, "end": v(1.9, -15.18) * mm});
            skArc(sketch, "E1901", {"start": v(1.9, -15.18) * mm, "mid": v(2.12, -15.22) * mm, "end": v(2.33, -15.3) * mm});
            skArc(sketch, "E1902", {"start": v(2.33, -15.3) * mm, "mid": v(2.45, -15.4) * mm, "end": v(2.5, -15.56) * mm});
            skArc(sketch, "E1903", {"start": v(2.5, -15.56) * mm, "mid": v(2.5, -15.83) * mm, "end": v(2.46, -16.1) * mm});
            skArc(sketch, "E1904", {"start": v(2.46, -16.1) * mm, "mid": v(2.3, -16.65) * mm, "end": v(2.07, -17.17) * mm});
            skArc(sketch, "E1905", {"start": v(2.07, -17.17) * mm, "mid": v(1.78, -17.64) * mm, "end": v(1.42, -18.05) * mm});
            skArc(sketch, "E1906", {"start": v(1.42, -18.05) * mm, "mid": v(0.97, -18.43) * mm, "end": v(0.46, -18.74) * mm});
            skArc(sketch, "E1907", {"start": v(0.46, -18.74) * mm, "mid": v(-0.18, -19.04) * mm, "end": v(-0.85, -19.3) * mm});
            skArc(sketch, "E1908", {"start": v(-0.85, -19.3) * mm, "mid": v(-1.13, -19.39) * mm, "end": v(-1.4, -19.48) * mm});
            skArc(sketch, "E1909", {"start": v(-1.4, -19.48) * mm, "mid": v(-1.6, -19.56) * mm, "end": v(-1.78, -19.64) * mm});
            skArc(sketch, "E1910", {"start": v(-1.78, -19.64) * mm, "mid": v(-1.9, -19.7) * mm, "end": v(-2.02, -19.78) * mm});
            skArc(sketch, "E1911", {"start": v(-2.02, -19.78) * mm, "mid": v(-2.06, -19.82) * mm, "end": v(-2.06, -19.87) * mm});
            skArc(sketch, "E1912", {"start": v(-2.06, -19.87) * mm, "mid": v(-1.98, -19.97) * mm, "end": v(-1.86, -20) * mm});
            skArc(sketch, "E1913", {"start": v(-1.86, -20) * mm, "mid": v(-1.5, -19.96) * mm, "end": v(-1.14, -19.9) * mm});
            skArc(sketch, "E1914", {"start": v(-1.14, -19.9) * mm, "mid": v(-0.73, -19.8) * mm, "end": v(-0.33, -19.7) * mm});
            skArc(sketch, "E1915", {"start": v(-0.33, -19.7) * mm, "mid": v(0.04, -19.56) * mm, "end": v(0.4, -19.4) * mm});
            skArc(sketch, "E1916", {"start": v(0.4, -19.4) * mm, "mid": v(0.93, -19.1) * mm, "end": v(1.4, -18.71) * mm});
            skArc(sketch, "E1917", {"start": v(1.4, -18.71) * mm, "mid": v(1.86, -18.22) * mm, "end": v(2.26, -17.68) * mm});
            skArc(sketch, "E1918", {"start": v(2.26, -17.68) * mm, "mid": v(2.58, -17.1) * mm, "end": v(2.84, -16.5) * mm});
            skArc(sketch, "E1919", {"start": v(2.84, -16.5) * mm, "mid": v(2.99, -15.92) * mm, "end": v(3.04, -15.33) * mm});
            skArc(sketch, "E1920", {"start": v(3.04, -15.33) * mm, "mid": v(3.03, -15.22) * mm, "end": v(3.03, -15.12) * mm});
            skArc(sketch, "E1921", {"start": v(3.03, -15.12) * mm, "mid": v(3.02, -15.05) * mm, "end": v(3, -14.97) * mm});
            skArc(sketch, "E1922", {"start": v(3, -14.97) * mm, "mid": v(3, -14.92) * mm, "end": v(2.97, -14.87) * mm});
            skArc(sketch, "E1923", {"start": v(2.97, -14.87) * mm, "mid": v(2.95, -14.83) * mm, "end": v(2.92, -14.8) * mm});
            skArc(sketch, "E1924", {"start": v(2.92, -14.8) * mm, "mid": v(2.86, -14.77) * mm, "end": v(2.8, -14.75) * mm});
            skArc(sketch, "E1925", {"start": v(2.8, -14.75) * mm, "mid": v(2.6, -14.73) * mm, "end": v(2.4, -14.72) * mm});
            skArc(sketch, "E1926", {"start": v(2.4, -14.72) * mm, "mid": v(2.1, -14.71) * mm, "end": v(1.8, -14.7) * mm});
            skArc(sketch, "E1927", {"start": v(1.8, -14.7) * mm, "mid": v(1.27, -14.7) * mm, "end": v(0.73, -14.7) * mm});
            skArc(sketch, "E1928", {"start": v(0.73, -14.7) * mm, "mid": v(0.32, -14.7) * mm, "end": v(-0.1, -14.7) * mm});
            skArc(sketch, "E1929", {"start": v(-0.1, -14.7) * mm, "mid": v(-0.48, -14.7) * mm, "end": v(-0.86, -14.7) * mm});
            skArc(sketch, "E1930", {"start": v(-0.86, -14.7) * mm, "mid": v(-1.18, -14.71) * mm, "end": v(-1.5, -14.72) * mm});
            skArc(sketch, "E1931", {"start": v(-1.5, -14.72) * mm, "mid": v(-1.65, -14.73) * mm, "end": v(-1.79, -14.74) * mm});
            skArc(sketch, "E1932", {"start": v(-13.96, -15.07) * mm, "mid": v(-14.07, -15.32) * mm, "end": v(-14.12, -15.58) * mm});
            skArc(sketch, "E1933", {"start": v(-14.12, -15.58) * mm, "mid": v(-14.16, -16.02) * mm, "end": v(-14.18, -16.46) * mm});
            skArc(sketch, "E1934", {"start": v(-14.18, -16.46) * mm, "mid": v(-14.19, -16.92) * mm, "end": v(-14.17, -17.39) * mm});
            skArc(sketch, "E1935", {"start": v(-14.17, -17.39) * mm, "mid": v(-14.12, -17.76) * mm, "end": v(-14.05, -18.12) * mm});
            skArc(sketch, "E1936", {"start": v(-14.05, -18.12) * mm, "mid": v(-13.95, -18.45) * mm, "end": v(-13.83, -18.78) * mm});
            skArc(sketch, "E1937", {"start": v(-13.83, -18.78) * mm, "mid": v(-13.7, -19.05) * mm, "end": v(-13.54, -19.3) * mm});
            skArc(sketch, "E1938", {"start": v(-13.54, -19.3) * mm, "mid": v(-13.4, -19.5) * mm, "end": v(-13.22, -19.67) * mm});
            skArc(sketch, "E1939", {"start": v(-13.22, -19.67) * mm, "mid": v(-13.07, -19.75) * mm, "end": v(-12.9, -19.78) * mm});
            skArc(sketch, "E1940", {"start": v(-12.9, -19.78) * mm, "mid": v(-12.78, -19.76) * mm, "end": v(-12.66, -19.7) * mm});
            skArc(sketch, "E1941", {"start": v(-12.66, -19.7) * mm, "mid": v(-12.5, -19.56) * mm, "end": v(-12.33, -19.4) * mm});
            skArc(sketch, "E1942", {"start": v(-12.33, -19.4) * mm, "mid": v(-12.16, -19.2) * mm, "end": v(-12, -19) * mm});
            skArc(sketch, "E1943", {"start": v(-12, -19) * mm, "mid": v(-11.86, -18.8) * mm, "end": v(-11.74, -18.58) * mm});
            skArc(sketch, "E1944", {"start": v(-11.74, -18.58) * mm, "mid": v(-11.67, -18.43) * mm, "end": v(-11.6, -18.26) * mm});
            skArc(sketch, "E1945", {"start": v(-11.6, -18.26) * mm, "mid": v(-11.56, -18.16) * mm, "end": v(-11.54, -18.06) * mm});
            skArc(sketch, "E1946", {"start": v(-11.54, -18.06) * mm, "mid": v(-11.54, -17.99) * mm, "end": v(-11.55, -17.92) * mm});
            skArc(sketch, "E1947", {"start": v(-11.55, -17.92) * mm, "mid": v(-11.58, -17.88) * mm, "end": v(-11.63, -17.85) * mm});
            skArc(sketch, "E1948", {"start": v(-11.63, -17.85) * mm, "mid": v(-11.7, -17.84) * mm, "end": v(-11.76, -17.85) * mm});
            skArc(sketch, "E1949", {"start": v(-11.76, -17.85) * mm, "mid": v(-11.85, -17.91) * mm, "end": v(-11.92, -17.98) * mm});
            skArc(sketch, "E1950", {"start": v(-11.92, -17.98) * mm, "mid": v(-12.03, -18.1) * mm, "end": v(-12.12, -18.22) * mm});
            skArc(sketch, "E1951", {"start": v(-12.12, -18.22) * mm, "mid": v(-12.27, -18.43) * mm, "end": v(-12.41, -18.64) * mm});
            skArc(sketch, "E1952", {"start": v(-12.41, -18.64) * mm, "mid": v(-12.49, -18.76) * mm, "end": v(-12.56, -18.87) * mm});
            skArc(sketch, "E1953", {"start": v(-12.56, -18.87) * mm, "mid": v(-12.63, -18.96) * mm, "end": v(-12.7, -19.05) * mm});
            skArc(sketch, "E1954", {"start": v(-12.7, -19.05) * mm, "mid": v(-12.77, -19.12) * mm, "end": v(-12.84, -19.2) * mm});
            skArc(sketch, "E1955", {"start": v(-12.84, -19.2) * mm, "mid": v(-12.86, -19.21) * mm, "end": v(-12.9, -19.22) * mm});
            skArc(sketch, "E1956", {"start": v(-12.9, -19.22) * mm, "mid": v(-12.97, -19.2) * mm, "end": v(-13.04, -19.17) * mm});
            skArc(sketch, "E1957", {"start": v(-13.04, -19.17) * mm, "mid": v(-13.13, -19.09) * mm, "end": v(-13.22, -19) * mm});
            skArc(sketch, "E1958", {"start": v(-13.22, -19) * mm, "mid": v(-13.3, -18.9) * mm, "end": v(-13.38, -18.78) * mm});
            skArc(sketch, "E1959", {"start": v(-13.38, -18.78) * mm, "mid": v(-13.44, -18.67) * mm, "end": v(-13.48, -18.55) * mm});
            skArc(sketch, "E1960", {"start": v(-13.48, -18.55) * mm, "mid": v(-13.5, -18.46) * mm, "end": v(-13.52, -18.37) * mm});
            skArc(sketch, "E1961", {"start": v(-13.52, -18.37) * mm, "mid": v(-13.54, -18.14) * mm, "end": v(-13.56, -17.91) * mm});
            skArc(sketch, "E1962", {"start": v(-13.56, -17.91) * mm, "mid": v(-13.58, -17.64) * mm, "end": v(-13.6, -17.37) * mm});
            skArc(sketch, "E1963", {"start": v(-13.6, -17.37) * mm, "mid": v(-13.61, -17.07) * mm, "end": v(-13.63, -16.77) * mm});
            skArc(sketch, "E1964", {"start": v(-13.63, -16.77) * mm, "mid": v(-13.64, -16.48) * mm, "end": v(-13.65, -16.18) * mm});
            skArc(sketch, "E1965", {"start": v(-13.65, -16.18) * mm, "mid": v(-13.67, -15.92) * mm, "end": v(-13.68, -15.66) * mm});
            skArc(sketch, "E1966", {"start": v(-13.68, -15.66) * mm, "mid": v(-13.7, -15.44) * mm, "end": v(-13.71, -15.22) * mm});
            skArc(sketch, "E1967", {"start": v(-13.71, -15.22) * mm, "mid": v(-13.72, -15.16) * mm, "end": v(-13.73, -15.1) * mm});
            skArc(sketch, "E1968", {"start": v(-13.73, -15.1) * mm, "mid": v(-13.75, -15.05) * mm, "end": v(-13.78, -15) * mm});
            skArc(sketch, "E1969", {"start": v(-13.78, -15) * mm, "mid": v(-13.8, -14.97) * mm, "end": v(-13.84, -14.96) * mm});
            skArc(sketch, "E1970", {"start": v(-13.84, -14.96) * mm, "mid": v(-13.87, -14.96) * mm, "end": v(-13.9, -14.98) * mm});
            skArc(sketch, "E1971", {"start": v(-13.9, -14.98) * mm, "mid": v(-13.93, -15.02) * mm, "end": v(-13.96, -15.07) * mm});
            skArc(sketch, "E1972", {"start": v(-9.91, -15.11) * mm, "mid": v(-9.91, -15.17) * mm, "end": v(-9.9, -15.22) * mm});
            skArc(sketch, "E1973", {"start": v(-9.9, -15.22) * mm, "mid": v(-9.86, -15.34) * mm, "end": v(-9.82, -15.45) * mm});
            skArc(sketch, "E1974", {"start": v(-9.82, -15.45) * mm, "mid": v(-9.77, -15.59) * mm, "end": v(-9.72, -15.72) * mm});
            skArc(sketch, "E1975", {"start": v(-9.72, -15.72) * mm, "mid": v(-9.66, -15.86) * mm, "end": v(-9.6, -16) * mm});
            skArc(sketch, "E1976", {"start": v(-9.6, -16) * mm, "mid": v(-9.53, -16.16) * mm, "end": v(-9.47, -16.32) * mm});
            skArc(sketch, "E1977", {"start": v(-9.47, -16.32) * mm, "mid": v(-9.4, -16.5) * mm, "end": v(-9.32, -16.7) * mm});
            skArc(sketch, "E1978", {"start": v(-9.32, -16.7) * mm, "mid": v(-9.26, -16.88) * mm, "end": v(-9.2, -17.07) * mm});
            skArc(sketch, "E1979", {"start": v(-9.2, -17.07) * mm, "mid": v(-9.15, -17.23) * mm, "end": v(-9.1, -17.38) * mm});
            skArc(sketch, "E1980", {"start": v(-9.1, -17.38) * mm, "mid": v(-9, -17.8) * mm, "end": v(-8.88, -18.2) * mm});
            skArc(sketch, "E1981", {"start": v(-8.88, -18.2) * mm, "mid": v(-8.82, -18.4) * mm, "end": v(-8.76, -18.58) * mm});
            skArc(sketch, "E1982", {"start": v(-8.76, -18.58) * mm, "mid": v(-8.71, -18.69) * mm, "end": v(-8.66, -18.8) * mm});
            skArc(sketch, "E1983", {"start": v(-8.66, -18.8) * mm, "mid": v(-8.63, -18.83) * mm, "end": v(-8.57, -18.86) * mm});
            skArc(sketch, "E1984", {"start": v(-8.57, -18.86) * mm, "mid": v(-8.46, -18.83) * mm, "end": v(-8.41, -18.74) * mm});
            skArc(sketch, "E1985", {"start": v(-8.41, -18.74) * mm, "mid": v(-8.4, -18.48) * mm, "end": v(-8.42, -18.22) * mm});
            skArc(sketch, "E1986", {"start": v(-8.42, -18.22) * mm, "mid": v(-8.47, -17.85) * mm, "end": v(-8.55, -17.49) * mm});
            skArc(sketch, "E1987", {"start": v(-8.55, -17.49) * mm, "mid": v(-8.67, -17.07) * mm, "end": v(-8.8, -16.66) * mm});
            skArc(sketch, "E1988", {"start": v(-8.8, -16.66) * mm, "mid": v(-8.9, -16.43) * mm, "end": v(-9, -16.2) * mm});
            skArc(sketch, "E1989", {"start": v(-9, -16.2) * mm, "mid": v(-9.11, -15.98) * mm, "end": v(-9.23, -15.75) * mm});
            skArc(sketch, "E1990", {"start": v(-9.23, -15.75) * mm, "mid": v(-9.36, -15.56) * mm, "end": v(-9.49, -15.37) * mm});
            skArc(sketch, "E1991", {"start": v(-9.49, -15.37) * mm, "mid": v(-9.6, -15.22) * mm, "end": v(-9.73, -15.1) * mm});
            skLineSegment(sketch, "E1992", {"start": v(-9.73, -15.1) * mm, "end": v(-9.91, -14.93) * mm});
            skLineSegment(sketch, "E1993", {"start": v(-9.91, -14.93) * mm, "end": v(-9.91, -15.11) * mm});
            skArc(sketch, "E1994", {"start": v(-35.24, 11.65) * mm, "mid": v(-35.38, 11.23) * mm, "end": v(-35.56, 10.83) * mm});
            skArc(sketch, "E1995", {"start": v(-35.56, 10.83) * mm, "mid": v(-35.76, 10.5) * mm, "end": v(-36.02, 10.22) * mm});
            skArc(sketch, "E1996", {"start": v(-36.02, 10.22) * mm, "mid": v(-36.3, 10) * mm, "end": v(-36.62, 9.82) * mm});
            skArc(sketch, "E1997", {"start": v(-36.62, 9.82) * mm, "mid": v(-36.98, 9.7) * mm, "end": v(-37.36, 9.63) * mm});
            skArc(sketch, "E1998", {"start": v(-37.36, 9.63) * mm, "mid": v(-37.46, 9.62) * mm, "end": v(-37.55, 9.6) * mm});
            skArc(sketch, "E1999", {"start": v(-37.55, 9.6) * mm, "mid": v(-37.64, 9.59) * mm, "end": v(-37.72, 9.57) * mm});
            skArc(sketch, "E2000", {"start": v(-37.72, 9.57) * mm, "mid": v(-37.8, 9.56) * mm, "end": v(-37.86, 9.54) * mm});
            skArc(sketch, "E2001", {"start": v(-37.86, 9.54) * mm, "mid": v(-37.89, 9.53) * mm, "end": v(-37.91, 9.5) * mm});
            skArc(sketch, "E2002", {"start": v(-37.91, 9.5) * mm, "mid": v(-37.93, 9.49) * mm, "end": v(-37.94, 9.46) * mm});
            skArc(sketch, "E2003", {"start": v(-37.94, 9.46) * mm, "mid": v(-37.94, 9.4) * mm, "end": v(-37.94, 9.33) * mm});
            skArc(sketch, "E2004", {"start": v(-37.94, 9.33) * mm, "mid": v(-37.94, 9.25) * mm, "end": v(-37.93, 9.16) * mm});
            skArc(sketch, "E2005", {"start": v(-37.93, 9.16) * mm, "mid": v(-37.92, 9.06) * mm, "end": v(-37.91, 8.95) * mm});
            skArc(sketch, "E2006", {"start": v(-37.91, 8.95) * mm, "mid": v(-37.9, 8.8) * mm, "end": v(-37.88, 8.63) * mm});
            skArc(sketch, "E2007", {"start": v(-37.88, 8.63) * mm, "mid": v(-37.87, 8.16) * mm, "end": v(-37.85, 7.69) * mm});
            skArc(sketch, "E2008", {"start": v(-37.85, 7.69) * mm, "mid": v(-37.84, 7.13) * mm, "end": v(-37.82, 6.57) * mm});
            skArc(sketch, "E2009", {"start": v(-37.82, 6.57) * mm, "mid": v(-37.81, 5.95) * mm, "end": v(-37.8, 5.33) * mm});
            skLineSegment(sketch, "E2010", {"start": v(-37.8, 5.33) * mm, "end": v(-37.75, 2.2) * mm});
            skLineSegment(sketch, "E2011", {"start": v(-37.75, 2.2) * mm, "end": v(-37.36, 2.13) * mm});
            skArc(sketch, "E2012", {"start": v(-37.36, 2.13) * mm, "mid": v(-37, 2.06) * mm, "end": v(-36.64, 1.97) * mm});
            skArc(sketch, "E2013", {"start": v(-36.64, 1.97) * mm, "mid": v(-36.41, 1.9) * mm, "end": v(-36.19, 1.82) * mm});
            skArc(sketch, "E2014", {"start": v(-36.19, 1.82) * mm, "mid": v(-36.02, 1.73) * mm, "end": v(-35.86, 1.63) * mm});
            skArc(sketch, "E2015", {"start": v(-35.86, 1.63) * mm, "mid": v(-35.7, 1.5) * mm, "end": v(-35.54, 1.34) * mm});
            skArc(sketch, "E2016", {"start": v(-35.54, 1.34) * mm, "mid": v(-35.48, 1.27) * mm, "end": v(-35.42, 1.2) * mm});
            skArc(sketch, "E2017", {"start": v(-35.42, 1.2) * mm, "mid": v(-35.35, 1.13) * mm, "end": v(-35.28, 1.05) * mm});
            skArc(sketch, "E2018", {"start": v(-35.28, 1.05) * mm, "mid": v(-35.2, 0.97) * mm, "end": v(-35.14, 0.9) * mm});
            skArc(sketch, "E2019", {"start": v(-35.14, 0.9) * mm, "mid": v(-35.08, 0.83) * mm, "end": v(-35.02, 0.76) * mm});
            skLineSegment(sketch, "E2020", {"start": v(-35.02, 0.76) * mm, "end": v(-34.76, 0.48) * mm});
            skLineSegment(sketch, "E2021", {"start": v(-34.76, 0.48) * mm, "end": v(-34.62, 0.66) * mm});
            skArc(sketch, "E2022", {"start": v(-34.62, 0.66) * mm, "mid": v(-34.46, 0.86) * mm, "end": v(-34.33, 1.07) * mm});
            skArc(sketch, "E2023", {"start": v(-34.33, 1.07) * mm, "mid": v(-33.66, 2.2) * mm, "end": v(-33, 3.35) * mm});
            skArc(sketch, "E2024", {"start": v(-33, 3.35) * mm, "mid": v(-32.3, 4.55) * mm, "end": v(-31.6, 5.75) * mm});
            skArc(sketch, "E2025", {"start": v(-31.6, 5.75) * mm, "mid": v(-31.56, 5.84) * mm, "end": v(-31.54, 5.93) * mm});
            skArc(sketch, "E2026", {"start": v(-31.54, 5.93) * mm, "mid": v(-31.55, 5.96) * mm, "end": v(-31.56, 6) * mm});
            skArc(sketch, "E2027", {"start": v(-31.56, 6) * mm, "mid": v(-32.42, 7.51) * mm, "end": v(-33.27, 9.04) * mm});
            skArc(sketch, "E2028", {"start": v(-33.27, 9.04) * mm, "mid": v(-34.12, 10.55) * mm, "end": v(-34.96, 12.06) * mm});
            skArc(sketch, "E2029", {"start": v(-34.96, 12.06) * mm, "mid": v(-35, 12.11) * mm, "end": v(-35.04, 12.16) * mm});
            skArc(sketch, "E2030", {"start": v(-35.04, 12.16) * mm, "mid": v(-35.05, 12.16) * mm, "end": v(-35.07, 12.15) * mm});
            skArc(sketch, "E2031", {"start": v(-35.07, 12.15) * mm, "mid": v(-35.1, 12.1) * mm, "end": v(-35.12, 12.03) * mm});
            skArc(sketch, "E2032", {"start": v(-35.12, 12.03) * mm, "mid": v(-35.15, 11.95) * mm, "end": v(-35.18, 11.86) * mm});
            skArc(sketch, "E2033", {"start": v(-35.18, 11.86) * mm, "mid": v(-35.21, 11.75) * mm, "end": v(-35.24, 11.65) * mm});
            skSolve(sketch);
        }
        {
            var Q0;
            Q0=qCreatedBy(makeId("Top.planeOp"),FACE);
            var sketch = newSketch(context, id + "F1", { "sketchPlane" : qUnion([Q0])});
            skLineSegment(sketch, "E2034.bottom", {"start": v(85, 25) * mm, "end": v(-85, 25) * mm});
            skLineSegment(sketch, "E2034.top", {"start": v(85, -25) * mm, "end": v(-85, -25) * mm});
            skLineSegment(sketch, "E2034.left", {"start": v(85, 25) * mm, "end": v(85, -25) * mm});
            skLineSegment(sketch, "E2034.right", {"start": v(-85, 25) * mm, "end": v(-85, -25) * mm});
            skPoint(sketch, "E2034.middle", {"position": v(0, 0) * mm});
            skSolve(sketch);
        }
        {
            var Q0;
            Q0=qSketchRegion(id+"F1",true);
            extrude(context, id + "F2", {"entities" : qUnion([Q0]), "oppositeDirection" : true, "depth" : 0.5 * mm, "offsetDistance" : 25 * mm});
        }
        {
            var Q0;
            Q0=qSketchRegion(id+"F0",true);
            var Q1;
            Q1=makeQuery(id+"F0.imprint","IMPRINT",FACE,{"disambiguationData":[TD([[makeQuery(id+"F0.imprint","IMPRINT",EDGE,{"derivedFrom":sQuery(id+"F0.wireOp",EDGE,"E1210")}),-1.0]])]});
            var Q2;
            Q2=makeQuery(id+"F0.imprint","IMPRINT",FACE,{"disambiguationData":[TD([[makeQuery(id+"F0.imprint","IMPRINT",EDGE,{"derivedFrom":sQuery(id+"F0.wireOp",EDGE,"E1304")}),-1.0]])]});
            var Q3;
            Q3=makeQuery(id+"F0.imprint","IMPRINT",FACE,{"disambiguationData":[TD([[makeQuery(id+"F0.imprint","IMPRINT",EDGE,{"derivedFrom":sQuery(id+"F0.wireOp",EDGE,"E1704")}),-1.0]])]});
            extrude(context, id + "F3", {"entities" : qUnion([Q0, Q1, Q2, Q3]), "operationType" : NewBodyOperationType.ADD, "depth" : 0.5 * mm, "offsetDistance" : 25 * mm});
        }
        {
            var Q0;
            {var subQ0=sQuery(id+"F1.wireOp",EDGE,"E2034.bottom");var subQ1=sQuery(id+"F1.wireOp",EDGE,"E2034.top");var subQ2=sQuery(id+"F1.wireOp",EDGE,"E2034.left");var subQ3=sQuery(id+"F1.wireOp",EDGE,"E2034.right");Q0=makeQuery(id+"F3.boolean.opBoolean","SPLIT",FACE,{"disambiguationData":[TD([makeQuery(id+"F2.opExtrude","SWEPT_FACE",FACE,{"disambiguationData":[OSD([subQ0])]})])],"derivedFrom":makeQuery(id+"F2.opExtrude","CAP_FACE",FACE,{"disambiguationData":[OSD([subQ0,subQ1,subQ2,subQ3])],"isStart":true})});}
            extrude(context, id + "F4", {"entities" : qUnion([Q0]), "operationType" : NewBodyOperationType.ADD, "depth" : 1.5 * mm, "offsetDistance" : 25 * mm});
        }
        {
            var Q0;
            Q0=makeQuery(id+"F2.opExtrude","CAP_FACE",FACE,{"disambiguationData":[OSD([sQuery(id+"F1.wireOp",EDGE,"E2034.bottom"),sQuery(id+"F1.wireOp",EDGE,"E2034.top"),sQuery(id+"F1.wireOp",EDGE,"E2034.left"),sQuery(id+"F1.wireOp",EDGE,"E2034.right")])],"isStart":false});
            extrude(context, id + "F5", {"entities" : qUnion([Q0]), "operationType" : NewBodyOperationType.REMOVE, "oppositeDirection" : true, "depth" : 0.3 * mm, "offsetDistance" : 25 * mm});
        }
        {
            var Q0;
            Q0=makeQuery(id+"F4.opExtrude","CAP_FACE",FACE,{"disambiguationData":[OSD([sQuery(id+"F1.wireOp",EDGE,"E2034.bottom"),sQuery(id+"F1.wireOp",EDGE,"E2034.top"),sQuery(id+"F1.wireOp",EDGE,"E2034.left"),sQuery(id+"F1.wireOp",EDGE,"E2034.right")])],"isStart":false});
            extrude(context, id + "F6", {"entities" : qUnion([Q0]), "operationType" : NewBodyOperationType.REMOVE, "oppositeDirection" : true, "depth" : 0.2 * mm, "offsetDistance" : 25 * mm});
        }
        {
            var Q0;
            Q0=makeQuery(id+"F5.boolean.opBoolean","COPY",FACE,{"derivedFrom":makeQuery(id+"F5.opExtrude","CAP_FACE",FACE,{"disambiguationData":[OSD([sQuery(id+"F1.wireOp",EDGE,"E2034.bottom"),sQuery(id+"F1.wireOp",EDGE,"E2034.top"),sQuery(id+"F1.wireOp",EDGE,"E2034.left"),sQuery(id+"F1.wireOp",EDGE,"E2034.right")])],"isStart":false})});
            extrude(context, id + "F7", {"entities" : qUnion([Q0]), "operationType" : NewBodyOperationType.REMOVE, "oppositeDirection" : true, "depth" : 0.2 * mm, "offsetDistance" : 25 * mm});
        }
        {
            var Q0;
            Q0=makeQuery(id+"F3.opExtrude","CAP_FACE",FACE,{"disambiguationData":[OSD([sQuery(id+"F0.wireOp",EDGE,"E1210"),sQuery(id+"F0.wireOp",EDGE,"E1211"),sQuery(id+"F0.wireOp",EDGE,"E1212"),sQuery(id+"F0.wireOp",EDGE,"E1213"),sQuery(id+"F0.wireOp",EDGE,"E1214"),sQuery(id+"F0.wireOp",EDGE,"E1215"),sQuery(id+"F0.wireOp",EDGE,"E1216"),sQuery(id+"F0.wireOp",EDGE,"E1217"),sQuery(id+"F0.wireOp",EDGE,"E1218"),sQuery(id+"F0.wireOp",EDGE,"E1219"),sQuery(id+"F0.wireOp",EDGE,"E1220"),sQuery(id+"F0.wireOp",EDGE,"E1221"),sQuery(id+"F0.wireOp",EDGE,"E1222"),sQuery(id+"F0.wireOp",EDGE,"E1223"),sQuery(id+"F0.wireOp",EDGE,"E1224"),sQuery(id+"F0.wireOp",EDGE,"E1225"),sQuery(id+"F0.wireOp",EDGE,"E1226"),sQuery(id+"F0.wireOp",EDGE,"E1227"),sQuery(id+"F0.wireOp",EDGE,"E1228"),sQuery(id+"F0.wireOp",EDGE,"E1229"),sQuery(id+"F0.wireOp",EDGE,"E1230"),sQuery(id+"F0.wireOp",EDGE,"E1231"),sQuery(id+"F0.wireOp",EDGE,"E1232"),sQuery(id+"F0.wireOp",EDGE,"E1233"),sQuery(id+"F0.wireOp",EDGE,"E1234"),sQuery(id+"F0.wireOp",EDGE,"E1235"),sQuery(id+"F0.wireOp",EDGE,"E1236"),sQuery(id+"F0.wireOp",EDGE,"E1237"),sQuery(id+"F0.wireOp",EDGE,"E1238"),sQuery(id+"F0.wireOp",EDGE,"E1239"),sQuery(id+"F0.wireOp",EDGE,"E1240"),sQuery(id+"F0.wireOp",EDGE,"E1241"),sQuery(id+"F0.wireOp",EDGE,"E1242"),sQuery(id+"F0.wireOp",EDGE,"E1243"),sQuery(id+"F0.wireOp",EDGE,"E1244"),sQuery(id+"F0.wireOp",EDGE,"E1245"),sQuery(id+"F0.wireOp",EDGE,"E1246"),sQuery(id+"F0.wireOp",EDGE,"E1247"),sQuery(id+"F0.wireOp",EDGE,"E1248"),sQuery(id+"F0.wireOp",EDGE,"E1249"),sQuery(id+"F0.wireOp",EDGE,"E1250"),sQuery(id+"F0.wireOp",EDGE,"E1251"),sQuery(id+"F0.wireOp",EDGE,"E1252"),sQuery(id+"F0.wireOp",EDGE,"E1253"),sQuery(id+"F0.wireOp",EDGE,"E1254"),sQuery(id+"F0.wireOp",EDGE,"E1255"),sQuery(id+"F0.wireOp",EDGE,"E1256"),sQuery(id+"F0.wireOp",EDGE,"E1257"),sQuery(id+"F0.wireOp",EDGE,"E1258"),sQuery(id+"F0.wireOp",EDGE,"E1259"),sQuery(id+"F0.wireOp",EDGE,"E1260"),sQuery(id+"F0.wireOp",EDGE,"E1261"),sQuery(id+"F0.wireOp",EDGE,"E1262"),sQuery(id+"F0.wireOp",EDGE,"E1263"),sQuery(id+"F0.wireOp",EDGE,"E1264"),sQuery(id+"F0.wireOp",EDGE,"E1265"),sQuery(id+"F0.wireOp",EDGE,"E1266"),sQuery(id+"F0.wireOp",EDGE,"E1267"),sQuery(id+"F0.wireOp",EDGE,"E1268"),sQuery(id+"F0.wireOp",EDGE,"E1269"),sQuery(id+"F0.wireOp",EDGE,"E1270"),sQuery(id+"F0.wireOp",EDGE,"E1271"),sQuery(id+"F0.wireOp",EDGE,"E1272"),sQuery(id+"F0.wireOp",EDGE,"E1273"),sQuery(id+"F0.wireOp",EDGE,"E1274"),sQuery(id+"F0.wireOp",EDGE,"E1275"),sQuery(id+"F0.wireOp",EDGE,"E1276"),sQuery(id+"F0.wireOp",EDGE,"E1277"),sQuery(id+"F0.wireOp",EDGE,"E1278"),sQuery(id+"F0.wireOp",EDGE,"E1279"),sQuery(id+"F0.wireOp",EDGE,"E1280"),sQuery(id+"F0.wireOp",EDGE,"E1281"),sQuery(id+"F0.wireOp",EDGE,"E1282"),sQuery(id+"F0.wireOp",EDGE,"E1283"),sQuery(id+"F0.wireOp",EDGE,"E1284"),sQuery(id+"F0.wireOp",EDGE,"E1285"),sQuery(id+"F0.wireOp",EDGE,"E1286"),sQuery(id+"F0.wireOp",EDGE,"E1287"),sQuery(id+"F0.wireOp",EDGE,"E1288"),sQuery(id+"F0.wireOp",EDGE,"E1289"),sQuery(id+"F0.wireOp",EDGE,"E1290"),sQuery(id+"F0.wireOp",EDGE,"E1291"),sQuery(id+"F0.wireOp",EDGE,"E1292"),sQuery(id+"F0.wireOp",EDGE,"E1293"),sQuery(id+"F0.wireOp",EDGE,"E1294"),sQuery(id+"F0.wireOp",EDGE,"E1295"),sQuery(id+"F0.wireOp",EDGE,"E1296"),sQuery(id+"F0.wireOp",EDGE,"E1297"),sQuery(id+"F0.wireOp",EDGE,"E1298"),sQuery(id+"F0.wireOp",EDGE,"E1299"),sQuery(id+"F0.wireOp",EDGE,"E1300"),sQuery(id+"F0.wireOp",EDGE,"E1301"),sQuery(id+"F0.wireOp",EDGE,"E1302"),sQuery(id+"F0.wireOp",EDGE,"E1303"),sQuery(id+"F0.wireOp",EDGE,"E1994"),sQuery(id+"F0.wireOp",EDGE,"E1995"),sQuery(id+"F0.wireOp",EDGE,"E1996"),sQuery(id+"F0.wireOp",EDGE,"E1997"),sQuery(id+"F0.wireOp",EDGE,"E1998"),sQuery(id+"F0.wireOp",EDGE,"E1999"),sQuery(id+"F0.wireOp",EDGE,"E2000"),sQuery(id+"F0.wireOp",EDGE,"E2001"),sQuery(id+"F0.wireOp",EDGE,"E2002"),sQuery(id+"F0.wireOp",EDGE,"E2003"),sQuery(id+"F0.wireOp",EDGE,"E2004"),sQuery(id+"F0.wireOp",EDGE,"E2005"),sQuery(id+"F0.wireOp",EDGE,"E2006"),sQuery(id+"F0.wireOp",EDGE,"E2007"),sQuery(id+"F0.wireOp",EDGE,"E2008"),sQuery(id+"F0.wireOp",EDGE,"E2009"),sQuery(id+"F0.wireOp",EDGE,"E2010"),sQuery(id+"F0.wireOp",EDGE,"E2011"),sQuery(id+"F0.wireOp",EDGE,"E2012"),sQuery(id+"F0.wireOp",EDGE,"E2013"),sQuery(id+"F0.wireOp",EDGE,"E2014"),sQuery(id+"F0.wireOp",EDGE,"E2015"),sQuery(id+"F0.wireOp",EDGE,"E2016"),sQuery(id+"F0.wireOp",EDGE,"E2017"),sQuery(id+"F0.wireOp",EDGE,"E2018"),sQuery(id+"F0.wireOp",EDGE,"E2019"),sQuery(id+"F0.wireOp",EDGE,"E2020"),sQuery(id+"F0.wireOp",EDGE,"E2021"),sQuery(id+"F0.wireOp",EDGE,"E2022"),sQuery(id+"F0.wireOp",EDGE,"E2023"),sQuery(id+"F0.wireOp",EDGE,"E2024"),sQuery(id+"F0.wireOp",EDGE,"E2025"),sQuery(id+"F0.wireOp",EDGE,"E2026"),sQuery(id+"F0.wireOp",EDGE,"E2027"),sQuery(id+"F0.wireOp",EDGE,"E2028"),sQuery(id+"F0.wireOp",EDGE,"E2029"),sQuery(id+"F0.wireOp",EDGE,"E2030"),sQuery(id+"F0.wireOp",EDGE,"E2031"),sQuery(id+"F0.wireOp",EDGE,"E2032"),sQuery(id+"F0.wireOp",EDGE,"E2033")])],"isStart":false});
            var Q1;
            Q1=makeQuery(id+"F3.opExtrude","CAP_FACE",FACE,{"disambiguationData":[OSD([sQuery(id+"F0.wireOp",EDGE,"E1304"),sQuery(id+"F0.wireOp",EDGE,"E1305"),sQuery(id+"F0.wireOp",EDGE,"E1306"),sQuery(id+"F0.wireOp",EDGE,"E1307"),sQuery(id+"F0.wireOp",EDGE,"E1308"),sQuery(id+"F0.wireOp",EDGE,"E1309"),sQuery(id+"F0.wireOp",EDGE,"E1310"),sQuery(id+"F0.wireOp",EDGE,"E1311"),sQuery(id+"F0.wireOp",EDGE,"E1312"),sQuery(id+"F0.wireOp",EDGE,"E1313"),sQuery(id+"F0.wireOp",EDGE,"E1314"),sQuery(id+"F0.wireOp",EDGE,"E1315"),sQuery(id+"F0.wireOp",EDGE,"E1316"),sQuery(id+"F0.wireOp",EDGE,"E1317"),sQuery(id+"F0.wireOp",EDGE,"E1318"),sQuery(id+"F0.wireOp",EDGE,"E1319")])],"isStart":false});
            extrude(context, id + "F8", {"entities" : qUnion([Q0, Q1]), "operationType" : NewBodyOperationType.REMOVE, "oppositeDirection" : true, "depth" : 25 * mm, "offsetDistance" : 25 * mm});
        }
    });
